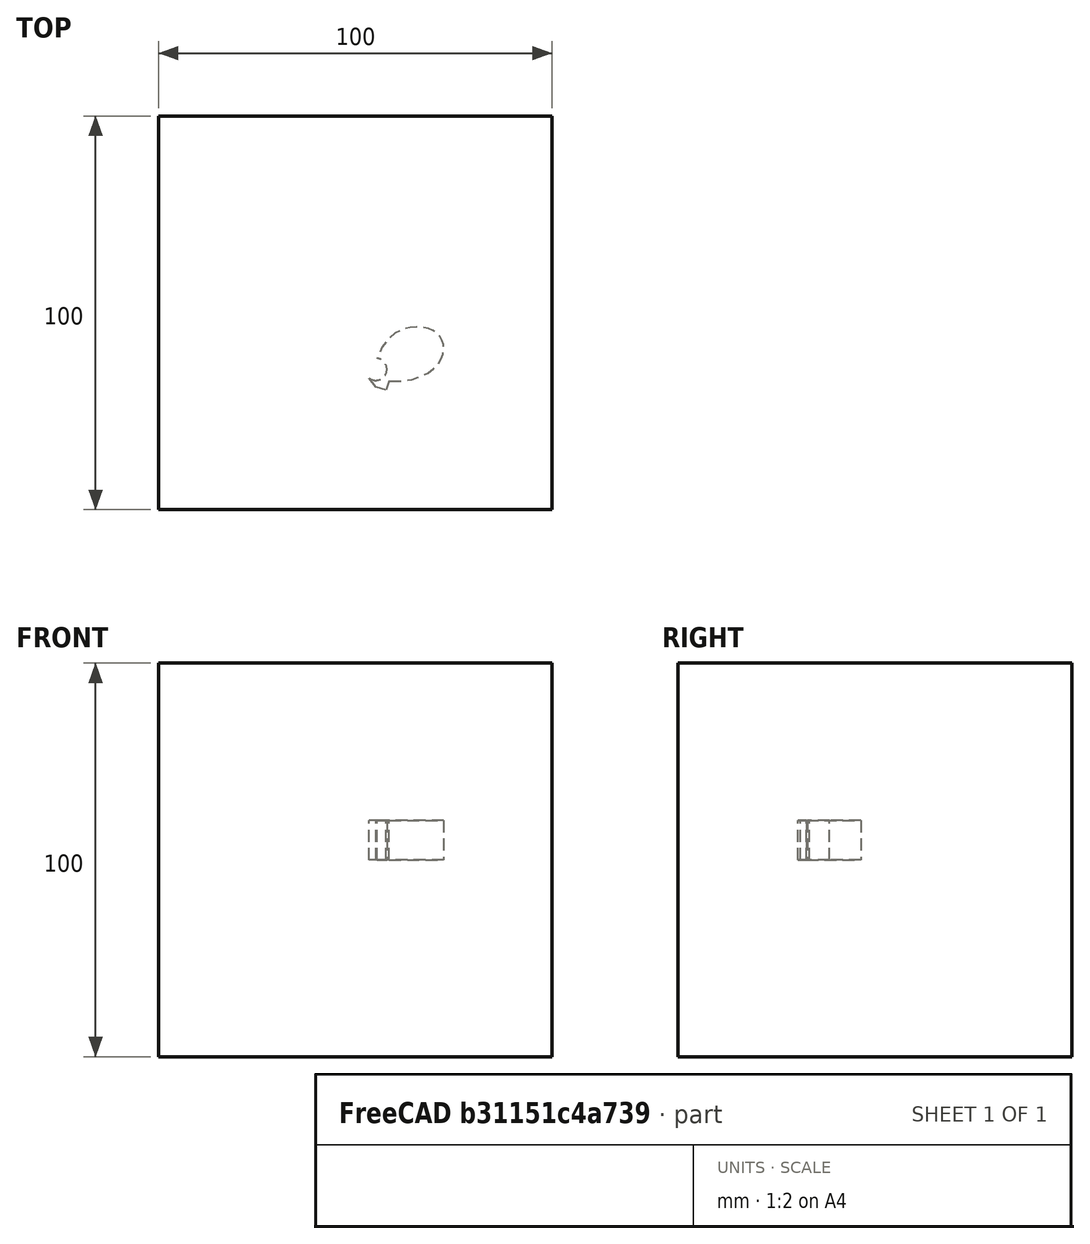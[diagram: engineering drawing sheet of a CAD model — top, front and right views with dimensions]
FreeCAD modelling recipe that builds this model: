
FCSTD DOCUMENT  (FreeCAD 1.0R39109 (Git))
Label: mirrorTest-1b
License: All rights reserved
LicenseURL: http://en.wikipedia.org/wiki/All_rights_reserved
objects: App::DocumentObjectGroupPython×1248, App::Part×2, Part::FeaturePython×1, Sketcher::SketchObject×1, Part::Extrusion×1, Part::Mirroring×1
note: 5 computed .brp shape members not serialized (recipe doc carries the construction recipe); baked Part::Feature solids carry a one-line shape summary decoded from their .brp

FEATURE [App::DocumentObjectGroupPython] HALFPI  # scripted group (container) (typed FeaturePython)
  name = HALFPI
  value = pi/2.
FEATURE [App::DocumentObjectGroupPython] PI  # scripted group (container) (typed FeaturePython)
  name = PI
  value = 1.*pi
FEATURE [App::DocumentObjectGroupPython] TWOPI  # scripted group (container) (typed FeaturePython)
  name = TWOPI
  value = 2.*pi
FEATURE [App::DocumentObjectGroupPython] Constants  # scripted group (container) (typed FeaturePython)
  Group = -> [HALFPI,PI,TWOPI]
FEATURE [App::DocumentObjectGroupPython] Variables  # scripted group (container) (typed FeaturePython)
FEATURE [App::DocumentObjectGroupPython] Quantities  # scripted group (container) (typed FeaturePython)
FEATURE [App::DocumentObjectGroupPython] Isotopes  # scripted group (container) (typed FeaturePython)
FEATURE [App::DocumentObjectGroupPython] Elements  # scripted group (container) (typed FeaturePython)
FEATURE [App::DocumentObjectGroupPython] G4Isotopes  # scripted group (container) (typed FeaturePython)
FEATURE [App::DocumentObjectGroupPython] H_element  # scripted group (container) (typed FeaturePython)
  Z = 1
  atom_value = 1.008
  formula = H
  name = H_element
FEATURE [App::DocumentObjectGroupPython] He_element  # scripted group (container) (typed FeaturePython)
  Z = 2
  atom_value = 4.0026
  formula = He
  name = He_element
FEATURE [App::DocumentObjectGroupPython] Li_element  # scripted group (container) (typed FeaturePython)
  Z = 3
  atom_value = 6.94
  formula = Li
  name = Li_element
FEATURE [App::DocumentObjectGroupPython] Be_element  # scripted group (container) (typed FeaturePython)
  Z = 4
  atom_value = 9.01218
  formula = Be
  name = Be_element
FEATURE [App::DocumentObjectGroupPython] B_element  # scripted group (container) (typed FeaturePython)
  Z = 5
  atom_value = 10.81
  formula = B
  name = B_element
FEATURE [App::DocumentObjectGroupPython] C_element  # scripted group (container) (typed FeaturePython)
  Z = 6
  atom_value = 12.011
  formula = C
  name = C_element
FEATURE [App::DocumentObjectGroupPython] N_element  # scripted group (container) (typed FeaturePython)
  Z = 7
  atom_value = 14.007
  formula = N
  name = N_element
FEATURE [App::DocumentObjectGroupPython] O_element  # scripted group (container) (typed FeaturePython)
  Z = 8
  atom_value = 15.999
  formula = O
  name = O_element
FEATURE [App::DocumentObjectGroupPython] F_element  # scripted group (container) (typed FeaturePython)
  Z = 9
  atom_value = 18.9984
  formula = F
  name = F_element
FEATURE [App::DocumentObjectGroupPython] Ne_element  # scripted group (container) (typed FeaturePython)
  Z = 10
  atom_value = 20.1797
  formula = Ne
  name = Ne_element
FEATURE [App::DocumentObjectGroupPython] Na_element  # scripted group (container) (typed FeaturePython)
  Z = 11
  atom_value = 22.9898
  formula = Na
  name = Na_element
FEATURE [App::DocumentObjectGroupPython] Mg_element  # scripted group (container) (typed FeaturePython)
  Z = 12
  atom_value = 24.305
  formula = Mg
  name = Mg_element
FEATURE [App::DocumentObjectGroupPython] Al_element  # scripted group (container) (typed FeaturePython)
  Z = 13
  atom_value = 26.9815
  formula = Al
  name = Al_element
FEATURE [App::DocumentObjectGroupPython] Si_element  # scripted group (container) (typed FeaturePython)
  Z = 14
  atom_value = 28.085
  formula = Si
  name = Si_element
FEATURE [App::DocumentObjectGroupPython] P_element  # scripted group (container) (typed FeaturePython)
  Z = 15
  atom_value = 30.9738
  formula = P
  name = P_element
FEATURE [App::DocumentObjectGroupPython] S_element  # scripted group (container) (typed FeaturePython)
  Z = 16
  atom_value = 32.06
  formula = S
  name = S_element
FEATURE [App::DocumentObjectGroupPython] Cl_element  # scripted group (container) (typed FeaturePython)
  Z = 17
  atom_value = 35.45
  formula = Cl
  name = Cl_element
FEATURE [App::DocumentObjectGroupPython] Ar_element  # scripted group (container) (typed FeaturePython)
  Z = 18
  atom_value = 39.95
  formula = Ar
  name = Ar_element
FEATURE [App::DocumentObjectGroupPython] K_element  # scripted group (container) (typed FeaturePython)
  Z = 19
  atom_value = 39.0983
  formula = K
  name = K_element
FEATURE [App::DocumentObjectGroupPython] Ca_element  # scripted group (container) (typed FeaturePython)
  Z = 20
  atom_value = 40.078
  formula = Ca
  name = Ca_element
FEATURE [App::DocumentObjectGroupPython] Sc_element  # scripted group (container) (typed FeaturePython)
  Z = 21
  atom_value = 44.9559
  formula = Sc
  name = Sc_element
FEATURE [App::DocumentObjectGroupPython] Ti_element  # scripted group (container) (typed FeaturePython)
  Z = 22
  atom_value = 47.867
  formula = Ti
  name = Ti_element
FEATURE [App::DocumentObjectGroupPython] V_element  # scripted group (container) (typed FeaturePython)
  Z = 23
  atom_value = 50.9415
  formula = V
  name = V_element
FEATURE [App::DocumentObjectGroupPython] Cr_element  # scripted group (container) (typed FeaturePython)
  Z = 24
  atom_value = 51.9961
  formula = Cr
  name = Cr_element
FEATURE [App::DocumentObjectGroupPython] Mn_element  # scripted group (container) (typed FeaturePython)
  Z = 25
  atom_value = 54.938
  formula = Mn
  name = Mn_element
FEATURE [App::DocumentObjectGroupPython] Fe_element  # scripted group (container) (typed FeaturePython)
  Z = 26
  atom_value = 55.845
  formula = Fe
  name = Fe_element
FEATURE [App::DocumentObjectGroupPython] Co_element  # scripted group (container) (typed FeaturePython)
  Z = 27
  atom_value = 58.9332
  formula = Co
  name = Co_element
FEATURE [App::DocumentObjectGroupPython] Ni_element  # scripted group (container) (typed FeaturePython)
  Z = 28
  atom_value = 58.6934
  formula = Ni
  name = Ni_element
FEATURE [App::DocumentObjectGroupPython] Cu_element  # scripted group (container) (typed FeaturePython)
  Z = 29
  atom_value = 63.546
  formula = Cu
  name = Cu_element
FEATURE [App::DocumentObjectGroupPython] Zn_element  # scripted group (container) (typed FeaturePython)
  Z = 30
  atom_value = 65.38
  formula = Zn
  name = Zn_element
FEATURE [App::DocumentObjectGroupPython] Ga_element  # scripted group (container) (typed FeaturePython)
  Z = 31
  atom_value = 69.723
  formula = Ga
  name = Ga_element
FEATURE [App::DocumentObjectGroupPython] Ge_element  # scripted group (container) (typed FeaturePython)
  Z = 32
  atom_value = 72.63
  formula = Ge
  name = Ge_element
FEATURE [App::DocumentObjectGroupPython] As_element  # scripted group (container) (typed FeaturePython)
  Z = 33
  atom_value = 74.9216
  formula = As
  name = As_element
FEATURE [App::DocumentObjectGroupPython] Se_element  # scripted group (container) (typed FeaturePython)
  Z = 34
  atom_value = 78.971
  formula = Se
  name = Se_element
FEATURE [App::DocumentObjectGroupPython] Br_element  # scripted group (container) (typed FeaturePython)
  Z = 35
  atom_value = 79.904
  formula = Br
  name = Br_element
FEATURE [App::DocumentObjectGroupPython] Kr_element  # scripted group (container) (typed FeaturePython)
  Z = 36
  atom_value = 83.798
  formula = Kr
  name = Kr_element
FEATURE [App::DocumentObjectGroupPython] Rb_element  # scripted group (container) (typed FeaturePython)
  Z = 37
  atom_value = 85.4678
  formula = Rb
  name = Rb_element
FEATURE [App::DocumentObjectGroupPython] Sr_element  # scripted group (container) (typed FeaturePython)
  Z = 38
  atom_value = 87.62
  formula = Sr
  name = Sr_element
FEATURE [App::DocumentObjectGroupPython] Y_element  # scripted group (container) (typed FeaturePython)
  Z = 39
  atom_value = 88.9058
  formula = Y
  name = Y_element
FEATURE [App::DocumentObjectGroupPython] Zr_element  # scripted group (container) (typed FeaturePython)
  Z = 40
  atom_value = 91.224
  formula = Zr
  name = Zr_element
FEATURE [App::DocumentObjectGroupPython] Nb_element  # scripted group (container) (typed FeaturePython)
  Z = 41
  atom_value = 92.9064
  formula = Nb
  name = Nb_element
FEATURE [App::DocumentObjectGroupPython] Mo_element  # scripted group (container) (typed FeaturePython)
  Z = 42
  atom_value = 95.95
  formula = Mo
  name = Mo_element
FEATURE [App::DocumentObjectGroupPython] Tc_element  # scripted group (container) (typed FeaturePython)
  Z = 43
  atom_value = 97
  formula = Tc
  name = Tc_element
FEATURE [App::DocumentObjectGroupPython] Ru_element  # scripted group (container) (typed FeaturePython)
  Z = 44
  atom_value = 101.07
  formula = Ru
  name = Ru_element
FEATURE [App::DocumentObjectGroupPython] Rh_element  # scripted group (container) (typed FeaturePython)
  Z = 45
  atom_value = 102.905
  formula = Rh
  name = Rh_element
FEATURE [App::DocumentObjectGroupPython] Pd_element  # scripted group (container) (typed FeaturePython)
  Z = 46
  atom_value = 106.42
  formula = Pd
  name = Pd_element
FEATURE [App::DocumentObjectGroupPython] Ag_element  # scripted group (container) (typed FeaturePython)
  Z = 47
  atom_value = 107.868
  formula = Ag
  name = Ag_element
FEATURE [App::DocumentObjectGroupPython] Cd_element  # scripted group (container) (typed FeaturePython)
  Z = 48
  atom_value = 112.414
  formula = Cd
  name = Cd_element
FEATURE [App::DocumentObjectGroupPython] In_element  # scripted group (container) (typed FeaturePython)
  Z = 49
  atom_value = 114.818
  formula = In
  name = In_element
FEATURE [App::DocumentObjectGroupPython] Sn_element  # scripted group (container) (typed FeaturePython)
  Z = 50
  atom_value = 118.71
  formula = Sn
  name = Sn_element
FEATURE [App::DocumentObjectGroupPython] Sb_element  # scripted group (container) (typed FeaturePython)
  Z = 51
  atom_value = 121.76
  formula = Sb
  name = Sb_element
FEATURE [App::DocumentObjectGroupPython] Te_element  # scripted group (container) (typed FeaturePython)
  Z = 52
  atom_value = 127.6
  formula = Te
  name = Te_element
FEATURE [App::DocumentObjectGroupPython] I_element  # scripted group (container) (typed FeaturePython)
  Z = 53
  atom_value = 126.904
  formula = I
  name = I_element
FEATURE [App::DocumentObjectGroupPython] Xe_element  # scripted group (container) (typed FeaturePython)
  Z = 54
  atom_value = 131.293
  formula = Xe
  name = Xe_element
FEATURE [App::DocumentObjectGroupPython] Cs_element  # scripted group (container) (typed FeaturePython)
  Z = 55
  atom_value = 132.905
  formula = Cs
  name = Cs_element
FEATURE [App::DocumentObjectGroupPython] Ba_element  # scripted group (container) (typed FeaturePython)
  Z = 56
  atom_value = 137.327
  formula = Ba
  name = Ba_element
FEATURE [App::DocumentObjectGroupPython] La_element  # scripted group (container) (typed FeaturePython)
  Z = 57
  atom_value = 138.905
  formula = La
  name = La_element
FEATURE [App::DocumentObjectGroupPython] Ce_element  # scripted group (container) (typed FeaturePython)
  Z = 58
  atom_value = 140.116
  formula = Ce
  name = Ce_element
FEATURE [App::DocumentObjectGroupPython] Pr_element  # scripted group (container) (typed FeaturePython)
  Z = 59
  atom_value = 140.908
  formula = Pr
  name = Pr_element
FEATURE [App::DocumentObjectGroupPython] Nd_element  # scripted group (container) (typed FeaturePython)
  Z = 60
  atom_value = 144.242
  formula = Nd
  name = Nd_element
FEATURE [App::DocumentObjectGroupPython] Pm_element  # scripted group (container) (typed FeaturePython)
  Z = 61
  atom_value = 145
  formula = Pm
  name = Pm_element
FEATURE [App::DocumentObjectGroupPython] Sm_element  # scripted group (container) (typed FeaturePython)
  Z = 62
  atom_value = 150.36
  formula = Sm
  name = Sm_element
FEATURE [App::DocumentObjectGroupPython] Eu_element  # scripted group (container) (typed FeaturePython)
  Z = 63
  atom_value = 151.964
  formula = Eu
  name = Eu_element
FEATURE [App::DocumentObjectGroupPython] Gd_element  # scripted group (container) (typed FeaturePython)
  Z = 64
  atom_value = 157.25
  formula = Gd
  name = Gd_element
FEATURE [App::DocumentObjectGroupPython] Tb_element  # scripted group (container) (typed FeaturePython)
  Z = 65
  atom_value = 158.925
  formula = Tb
  name = Tb_element
FEATURE [App::DocumentObjectGroupPython] Dy_element  # scripted group (container) (typed FeaturePython)
  Z = 66
  atom_value = 162.5
  formula = Dy
  name = Dy_element
FEATURE [App::DocumentObjectGroupPython] Ho_element  # scripted group (container) (typed FeaturePython)
  Z = 67
  atom_value = 164.93
  formula = Ho
  name = Ho_element
FEATURE [App::DocumentObjectGroupPython] Er_element  # scripted group (container) (typed FeaturePython)
  Z = 68
  atom_value = 167.259
  formula = Er
  name = Er_element
FEATURE [App::DocumentObjectGroupPython] Tm_element  # scripted group (container) (typed FeaturePython)
  Z = 69
  atom_value = 168.934
  formula = Tm
  name = Tm_element
FEATURE [App::DocumentObjectGroupPython] Yb_element  # scripted group (container) (typed FeaturePython)
  Z = 70
  atom_value = 173.045
  formula = Yb
  name = Yb_element
FEATURE [App::DocumentObjectGroupPython] Lu_element  # scripted group (container) (typed FeaturePython)
  Z = 71
  atom_value = 174.967
  formula = Lu
  name = Lu_element
FEATURE [App::DocumentObjectGroupPython] Hf_element  # scripted group (container) (typed FeaturePython)
  Z = 72
  atom_value = 178.49
  formula = Hf
  name = Hf_element
FEATURE [App::DocumentObjectGroupPython] Ta_element  # scripted group (container) (typed FeaturePython)
  Z = 73
  atom_value = 180.948
  formula = Ta
  name = Ta_element
FEATURE [App::DocumentObjectGroupPython] W_element  # scripted group (container) (typed FeaturePython)
  Z = 74
  atom_value = 183.84
  formula = W
  name = W_element
FEATURE [App::DocumentObjectGroupPython] Re_element  # scripted group (container) (typed FeaturePython)
  Z = 75
  atom_value = 186.207
  formula = Re
  name = Re_element
FEATURE [App::DocumentObjectGroupPython] Os_element  # scripted group (container) (typed FeaturePython)
  Z = 76
  atom_value = 190.23
  formula = Os
  name = Os_element
FEATURE [App::DocumentObjectGroupPython] Ir_element  # scripted group (container) (typed FeaturePython)
  Z = 77
  atom_value = 192.217
  formula = Ir
  name = Ir_element
FEATURE [App::DocumentObjectGroupPython] Pt_element  # scripted group (container) (typed FeaturePython)
  Z = 78
  atom_value = 195.084
  formula = Pt
  name = Pt_element
FEATURE [App::DocumentObjectGroupPython] Au_element  # scripted group (container) (typed FeaturePython)
  Z = 79
  atom_value = 196.967
  formula = Au
  name = Au_element
FEATURE [App::DocumentObjectGroupPython] Hg_element  # scripted group (container) (typed FeaturePython)
  Z = 80
  atom_value = 200.592
  formula = Hg
  name = Hg_element
FEATURE [App::DocumentObjectGroupPython] Tl_element  # scripted group (container) (typed FeaturePython)
  Z = 81
  atom_value = 204.38
  formula = Tl
  name = Tl_element
FEATURE [App::DocumentObjectGroupPython] Pb_element  # scripted group (container) (typed FeaturePython)
  Z = 82
  atom_value = 207.2
  formula = Pb
  name = Pb_element
FEATURE [App::DocumentObjectGroupPython] Bi_element  # scripted group (container) (typed FeaturePython)
  Z = 83
  atom_value = 208.98
  formula = Bi
  name = Bi_element
FEATURE [App::DocumentObjectGroupPython] Po_element  # scripted group (container) (typed FeaturePython)
  Z = 84
  atom_value = 209
  formula = Po
  name = Po_element
FEATURE [App::DocumentObjectGroupPython] At_element  # scripted group (container) (typed FeaturePython)
  Z = 85
  atom_value = 210
  formula = At
  name = At_element
FEATURE [App::DocumentObjectGroupPython] Rn_element  # scripted group (container) (typed FeaturePython)
  Z = 86
  atom_value = 222
  formula = Rn
  name = Rn_element
FEATURE [App::DocumentObjectGroupPython] Fr_element  # scripted group (container) (typed FeaturePython)
  Z = 87
  atom_value = 223
  formula = Fr
  name = Fr_element
FEATURE [App::DocumentObjectGroupPython] Ra_element  # scripted group (container) (typed FeaturePython)
  Z = 88
  atom_value = 226
  formula = Ra
  name = Ra_element
FEATURE [App::DocumentObjectGroupPython] Ac_element  # scripted group (container) (typed FeaturePython)
  Z = 89
  atom_value = 227
  formula = Ac
  name = Ac_element
FEATURE [App::DocumentObjectGroupPython] Th_element  # scripted group (container) (typed FeaturePython)
  Z = 90
  atom_value = 232.038
  formula = Th
  name = Th_element
FEATURE [App::DocumentObjectGroupPython] Pa_element  # scripted group (container) (typed FeaturePython)
  Z = 91
  atom_value = 231.036
  formula = Pa
  name = Pa_element
FEATURE [App::DocumentObjectGroupPython] U_element  # scripted group (container) (typed FeaturePython)
  Z = 92
  atom_value = 238.029
  formula = U
  name = U_element
FEATURE [App::DocumentObjectGroupPython] Np_element  # scripted group (container) (typed FeaturePython)
  Z = 93
  atom_value = 237
  formula = Np
  name = Np_element
FEATURE [App::DocumentObjectGroupPython] Pu_element  # scripted group (container) (typed FeaturePython)
  Z = 94
  atom_value = 244
  formula = Pu
  name = Pu_element
FEATURE [App::DocumentObjectGroupPython] Am_element  # scripted group (container) (typed FeaturePython)
  Z = 95
  atom_value = 243
  formula = Am
  name = Am_element
FEATURE [App::DocumentObjectGroupPython] Cm_element  # scripted group (container) (typed FeaturePython)
  Z = 96
  atom_value = 247
  formula = Cm
  name = Cm_element
FEATURE [App::DocumentObjectGroupPython] Bk_element  # scripted group (container) (typed FeaturePython)
  Z = 97
  atom_value = 247
  formula = Bk
  name = Bk_element
FEATURE [App::DocumentObjectGroupPython] Cf_element  # scripted group (container) (typed FeaturePython)
  Z = 98
  atom_value = 251
  formula = Cf
  name = Cf_element
FEATURE [App::DocumentObjectGroupPython] G4Elements  # scripted group (container) (typed FeaturePython)
  Group = -> [H_element,He_element,Li_element,Be_element,B_element,C_element,N_element,O_element,F_element,Ne_element,Na_element,Mg_element,Al_element,Si_element,P_element,S_element,Cl_element,Ar_element,K_element,Ca_element,Sc_element,Ti_element,V_element,Cr_element,Mn_element,Fe_element,Co_element,Ni_element,Cu_element,Zn_element,Ga_element,Ge_element,As_element,Se_element,Br_element,Kr_element,Rb_element,+61 more]
FEATURE [App::DocumentObjectGroupPython] H_element001  label="H_element : 0.101"  # scripted group (container) (typed FeaturePython)
  n = 0.101327
FEATURE [App::DocumentObjectGroupPython] C_element001  label="C_element : 0.775"  # scripted group (container) (typed FeaturePython)
  n = 0.7755
FEATURE [App::DocumentObjectGroupPython] N_element001  label="N_element : 0.035"  # scripted group (container) (typed FeaturePython)
  n = 0.035057
FEATURE [App::DocumentObjectGroupPython] O_element001  label="O_element : 0.052"  # scripted group (container) (typed FeaturePython)
  n = 0.0523159
FEATURE [App::DocumentObjectGroupPython] F_element001  label="F_element : 0.017"  # scripted group (container) (typed FeaturePython)
  n = 0.017422
FEATURE [App::DocumentObjectGroupPython] Ca_element001  label="Ca_element : 0.018"  # scripted group (container) (typed FeaturePython)
  n = 0.018378
FEATURE [App::DocumentObjectGroupPython] G4_A_150_TISSUE  label="G4_A-150_TISSUE"  # scripted group (container) (typed FeaturePython)
  Dunit = g/cm3
  Dvalue = 1.127
  Group = -> [H_element001,C_element001,N_element001,O_element001,F_element001,Ca_element001]
  conduct = 2
  density = 1
  expand = 3
  formula = G4_A-150_TISSUE
  name = G4_A-150_TISSUE
  specific = 4
FEATURE [App::DocumentObjectGroupPython] C_element002  label="C_element : 3"  # scripted group (container) (typed FeaturePython)
  n = 3
  ref = C_element
FEATURE [App::DocumentObjectGroupPython] H_element002  label="H_element : 6"  # scripted group (container) (typed FeaturePython)
  n = 6
  ref = H_element
FEATURE [App::DocumentObjectGroupPython] O_element002  label="O_element : 1"  # scripted group (container) (typed FeaturePython)
  n = 1
  ref = O_element
FEATURE [App::DocumentObjectGroupPython] G4_ACETONE  # scripted group (container) (typed FeaturePython)
  Dunit = g/cm3
  Dvalue = 0.7899
  Group = -> [C_element002,H_element002,O_element002]
  conduct = 2
  density = 1
  expand = 3
  formula = G4_ACETONE
  name = G4_ACETONE
  specific = 4
FEATURE [App::DocumentObjectGroupPython] C_element003  label="C_element : 2"  # scripted group (container) (typed FeaturePython)
  n = 2
  ref = C_element
FEATURE [App::DocumentObjectGroupPython] H_element003  label="H_element : 2"  # scripted group (container) (typed FeaturePython)
  n = 2
  ref = H_element
FEATURE [App::DocumentObjectGroupPython] G4_ACETYLENE  # scripted group (container) (typed FeaturePython)
  Dunit = g/cm3
  Dvalue = 0.0010967
  Group = -> [C_element003,H_element003]
  conduct = 2
  density = 1
  expand = 3
  formula = G4_ACETYLENE
  name = G4_ACETYLENE
  specific = 4
FEATURE [App::DocumentObjectGroupPython] C_element004  label="C_element : 5"  # scripted group (container) (typed FeaturePython)
  n = 5
  ref = C_element
FEATURE [App::DocumentObjectGroupPython] H_element004  label="H_element : 5"  # scripted group (container) (typed FeaturePython)
  n = 5
  ref = H_element
FEATURE [App::DocumentObjectGroupPython] N_element002  label="N_element : 5"  # scripted group (container) (typed FeaturePython)
  n = 5
  ref = N_element
FEATURE [App::DocumentObjectGroupPython] G4_ADENINE  # scripted group (container) (typed FeaturePython)
  Dunit = g/cm3
  Dvalue = 1.6
  Group = -> [C_element004,H_element004,N_element002]
  conduct = 2
  density = 1
  expand = 3
  formula = G4_ADENINE
  name = G4_ADENINE
  specific = 4
FEATURE [App::DocumentObjectGroupPython] H_element005  label="H_element : 0.114"  # scripted group (container) (typed FeaturePython)
  n = 0.114
FEATURE [App::DocumentObjectGroupPython] C_element005  label="C_element : 0.598"  # scripted group (container) (typed FeaturePython)
  n = 0.598
FEATURE [App::DocumentObjectGroupPython] N_element003  label="N_element : 0.007"  # scripted group (container) (typed FeaturePython)
  n = 0.007
FEATURE [App::DocumentObjectGroupPython] O_element003  label="O_element : 0.278"  # scripted group (container) (typed FeaturePython)
  n = 0.278
FEATURE [App::DocumentObjectGroupPython] Na_element001  label="Na_element : 0.001"  # scripted group (container) (typed FeaturePython)
  n = 0.001
FEATURE [App::DocumentObjectGroupPython] S_element001  label="S_element : 0.001"  # scripted group (container) (typed FeaturePython)
  n = 0.001
FEATURE [App::DocumentObjectGroupPython] Cl_element001  label="Cl_element : 0.001"  # scripted group (container) (typed FeaturePython)
  n = 0.001
FEATURE [App::DocumentObjectGroupPython] G4_ADIPOSE_TISSUE_ICRP  # scripted group (container) (typed FeaturePython)
  Dunit = g/cm3
  Dvalue = 0.95
  Group = -> [H_element005,C_element005,N_element003,O_element003,Na_element001,S_element001,Cl_element001]
  conduct = 2
  density = 1
  expand = 3
  formula = G4_ADIPOSE_TISSUE_ICRP
  name = G4_ADIPOSE_TISSUE_ICRP
  specific = 4
FEATURE [App::DocumentObjectGroupPython] C_element006  label="C_element : 0.000"  # scripted group (container) (typed FeaturePython)
  n = 0.000124
FEATURE [App::DocumentObjectGroupPython] N_element004  label="N_element : 0.755"  # scripted group (container) (typed FeaturePython)
  n = 0.755268
FEATURE [App::DocumentObjectGroupPython] O_element004  label="O_element : 0.232"  # scripted group (container) (typed FeaturePython)
  n = 0.231781
FEATURE [App::DocumentObjectGroupPython] Ar_element001  label="Ar_element : 0.013"  # scripted group (container) (typed FeaturePython)
  n = 0.012827
FEATURE [App::DocumentObjectGroupPython] G4_AIR  # scripted group (container) (typed FeaturePython)
  Dunit = g/cm3
  Dvalue = 0.00120479
  Group = -> [C_element006,N_element004,O_element004,Ar_element001]
  conduct = 2
  density = 1
  expand = 3
  formula = G4_AIR
  name = G4_AIR
  specific = 4
FEATURE [App::DocumentObjectGroupPython] C_element007  label="C_element : 006"  # scripted group (container) (typed FeaturePython)
  n = 3
  ref = C_element
FEATURE [App::DocumentObjectGroupPython] H_element006  label="H_element : 7"  # scripted group (container) (typed FeaturePython)
  n = 7
  ref = H_element
FEATURE [App::DocumentObjectGroupPython] N_element005  label="N_element : 1"  # scripted group (container) (typed FeaturePython)
  n = 1
  ref = N_element
FEATURE [App::DocumentObjectGroupPython] O_element005  label="O_element : 2"  # scripted group (container) (typed FeaturePython)
  n = 2
  ref = O_element
FEATURE [App::DocumentObjectGroupPython] G4_ALANINE  # scripted group (container) (typed FeaturePython)
  Dunit = g/cm3
  Dvalue = 1.42
  Group = -> [C_element007,H_element006,N_element005,O_element005]
  conduct = 2
  density = 1
  expand = 3
  formula = G4_ALANINE
  name = G4_ALANINE
  specific = 4
FEATURE [App::DocumentObjectGroupPython] Al_element001  label="Al_element : 2"  # scripted group (container) (typed FeaturePython)
  n = 2
  ref = Al_element
FEATURE [App::DocumentObjectGroupPython] O_element006  label="O_element : 3"  # scripted group (container) (typed FeaturePython)
  n = 3
  ref = O_element
FEATURE [App::DocumentObjectGroupPython] G4_ALUMINUM_OXIDE  # scripted group (container) (typed FeaturePython)
  Dunit = g/cm3
  Dvalue = 3.97
  Group = -> [Al_element001,O_element006]
  conduct = 2
  density = 1
  expand = 3
  formula = G4_ALUMINUM_OXIDE
  name = G4_ALUMINUM_OXIDE
  specific = 4
FEATURE [App::DocumentObjectGroupPython] H_element007  label="H_element : 0.106"  # scripted group (container) (typed FeaturePython)
  n = 0.10593
FEATURE [App::DocumentObjectGroupPython] C_element008  label="C_element : 0.789"  # scripted group (container) (typed FeaturePython)
  n = 0.788974
FEATURE [App::DocumentObjectGroupPython] O_element007  label="O_element : 0.105"  # scripted group (container) (typed FeaturePython)
  n = 0.105096
FEATURE [App::DocumentObjectGroupPython] G4_AMBER  # scripted group (container) (typed FeaturePython)
  Dunit = g/cm3
  Dvalue = 1.1
  Group = -> [H_element007,C_element008,O_element007]
  conduct = 2
  density = 1
  expand = 3
  formula = G4_AMBER
  name = G4_AMBER
  specific = 4
FEATURE [App::DocumentObjectGroupPython] N_element006  label="N_element : 006"  # scripted group (container) (typed FeaturePython)
  n = 1
  ref = N_element
FEATURE [App::DocumentObjectGroupPython] H_element008  label="H_element : 3"  # scripted group (container) (typed FeaturePython)
  n = 3
  ref = H_element
FEATURE [App::DocumentObjectGroupPython] G4_AMMONIA  # scripted group (container) (typed FeaturePython)
  Dunit = g/cm3
  Dvalue = 0.000826019
  Group = -> [N_element006,H_element008]
  conduct = 2
  density = 1
  expand = 3
  formula = G4_AMMONIA
  name = G4_AMMONIA
  specific = 4
FEATURE [App::DocumentObjectGroupPython] C_element009  label="C_element : 6"  # scripted group (container) (typed FeaturePython)
  n = 6
  ref = C_element
FEATURE [App::DocumentObjectGroupPython] H_element009  label="H_element : 008"  # scripted group (container) (typed FeaturePython)
  n = 7
  ref = H_element
FEATURE [App::DocumentObjectGroupPython] N_element007  label="N_element : 007"  # scripted group (container) (typed FeaturePython)
  n = 1
  ref = N_element
FEATURE [App::DocumentObjectGroupPython] G4_ANILINE  # scripted group (container) (typed FeaturePython)
  Dunit = g/cm3
  Dvalue = 1.0235
  Group = -> [C_element009,H_element009,N_element007]
  conduct = 2
  density = 1
  expand = 3
  formula = G4_ANILINE
  name = G4_ANILINE
  specific = 4
FEATURE [App::DocumentObjectGroupPython] C_element010  label="C_element : 14"  # scripted group (container) (typed FeaturePython)
  n = 14
  ref = C_element
FEATURE [App::DocumentObjectGroupPython] H_element010  label="H_element : 10"  # scripted group (container) (typed FeaturePython)
  n = 10
  ref = H_element
FEATURE [App::DocumentObjectGroupPython] G4_ANTHRACENE  # scripted group (container) (typed FeaturePython)
  Dunit = g/cm3
  Dvalue = 1.283
  Group = -> [C_element010,H_element010]
  conduct = 2
  density = 1
  expand = 3
  formula = G4_ANTHRACENE
  name = G4_ANTHRACENE
  specific = 4
FEATURE [App::DocumentObjectGroupPython] H_element011  label="H_element : 0.065"  # scripted group (container) (typed FeaturePython)
  n = 0.0654709
FEATURE [App::DocumentObjectGroupPython] C_element011  label="C_element : 0.537"  # scripted group (container) (typed FeaturePython)
  n = 0.536944
FEATURE [App::DocumentObjectGroupPython] N_element008  label="N_element : 0.021"  # scripted group (container) (typed FeaturePython)
  n = 0.0215
FEATURE [App::DocumentObjectGroupPython] O_element008  label="O_element : 0.032"  # scripted group (container) (typed FeaturePython)
  n = 0.032085
FEATURE [App::DocumentObjectGroupPython] F_element002  label="F_element : 0.167"  # scripted group (container) (typed FeaturePython)
  n = 0.167411
FEATURE [App::DocumentObjectGroupPython] Ca_element002  label="Ca_element : 0.177"  # scripted group (container) (typed FeaturePython)
  n = 0.176589
FEATURE [App::DocumentObjectGroupPython] G4_B_100_BONE  label="G4_B-100_BONE"  # scripted group (container) (typed FeaturePython)
  Dunit = g/cm3
  Dvalue = 1.45
  Group = -> [H_element011,C_element011,N_element008,O_element008,F_element002,Ca_element002]
  conduct = 2
  density = 1
  expand = 3
  formula = G4_B-100_BONE
  name = G4_B-100_BONE
  specific = 4
FEATURE [App::DocumentObjectGroupPython] H_element012  label="H_element : 0.057"  # scripted group (container) (typed FeaturePython)
  n = 0.057441
FEATURE [App::DocumentObjectGroupPython] C_element012  label="C_element : 0.790"  # scripted group (container) (typed FeaturePython)
  n = 0.774591
FEATURE [App::DocumentObjectGroupPython] O_element009  label="O_element : 0.168"  # scripted group (container) (typed FeaturePython)
  n = 0.167968
FEATURE [App::DocumentObjectGroupPython] G4_BAKELITE  # scripted group (container) (typed FeaturePython)
  Dunit = g/cm3
  Dvalue = 1.25
  Group = -> [H_element012,C_element012,O_element009]
  conduct = 2
  density = 1
  expand = 3
  formula = G4_BAKELITE
  name = G4_BAKELITE
  specific = 4
FEATURE [App::DocumentObjectGroupPython] Ba_element001  label="Ba_element : 1"  # scripted group (container) (typed FeaturePython)
  n = 1
  ref = Ba_element
FEATURE [App::DocumentObjectGroupPython] F_element003  label="F_element : 2"  # scripted group (container) (typed FeaturePython)
  n = 2
  ref = F_element
FEATURE [App::DocumentObjectGroupPython] G4_BARIUM_FLUORIDE  # scripted group (container) (typed FeaturePython)
  Dunit = g/cm3
  Dvalue = 4.89
  Group = -> [Ba_element001,F_element003]
  conduct = 2
  density = 1
  expand = 3
  formula = G4_BARIUM_FLUORIDE
  name = G4_BARIUM_FLUORIDE
  specific = 4
FEATURE [App::DocumentObjectGroupPython] Ba_element002  label="Ba_element : 002"  # scripted group (container) (typed FeaturePython)
  n = 1
  ref = Ba_element
FEATURE [App::DocumentObjectGroupPython] S_element002  label="S_element : 1"  # scripted group (container) (typed FeaturePython)
  n = 1
  ref = S_element
FEATURE [App::DocumentObjectGroupPython] O_element010  label="O_element : 4"  # scripted group (container) (typed FeaturePython)
  n = 4
  ref = O_element
FEATURE [App::DocumentObjectGroupPython] G4_BARIUM_SULFATE  # scripted group (container) (typed FeaturePython)
  Dunit = g/cm3
  Dvalue = 4.5
  Group = -> [Ba_element002,S_element002,O_element010]
  conduct = 2
  density = 1
  expand = 3
  formula = G4_BARIUM_SULFATE
  name = G4_BARIUM_SULFATE
  specific = 4
FEATURE [App::DocumentObjectGroupPython] C_element013  label="C_element : 007"  # scripted group (container) (typed FeaturePython)
  n = 6
  ref = C_element
FEATURE [App::DocumentObjectGroupPython] H_element013  label="H_element : 009"  # scripted group (container) (typed FeaturePython)
  n = 6
  ref = H_element
FEATURE [App::DocumentObjectGroupPython] G4_BENZENE  # scripted group (container) (typed FeaturePython)
  Dunit = g/cm3
  Dvalue = 0.87865
  Group = -> [C_element013,H_element013]
  conduct = 2
  density = 1
  expand = 3
  formula = G4_BENZENE
  name = G4_BENZENE
  specific = 4
FEATURE [App::DocumentObjectGroupPython] Be_element001  label="Be_element : 1"  # scripted group (container) (typed FeaturePython)
  n = 1
  ref = Be_element
FEATURE [App::DocumentObjectGroupPython] O_element011  label="O_element : 005"  # scripted group (container) (typed FeaturePython)
  n = 1
  ref = O_element
FEATURE [App::DocumentObjectGroupPython] G4_BERYLLIUM_OXIDE  # scripted group (container) (typed FeaturePython)
  Dunit = g/cm3
  Dvalue = 3.01
  Group = -> [Be_element001,O_element011]
  conduct = 2
  density = 1
  expand = 3
  formula = G4_BERYLLIUM_OXIDE
  name = G4_BERYLLIUM_OXIDE
  specific = 4
FEATURE [App::DocumentObjectGroupPython] Bi_element001  label="Bi_element : 4"  # scripted group (container) (typed FeaturePython)
  n = 4
  ref = Bi_element
FEATURE [App::DocumentObjectGroupPython] Ge_element001  label="Ge_element : 3"  # scripted group (container) (typed FeaturePython)
  n = 3
  ref = Ge_element
FEATURE [App::DocumentObjectGroupPython] O_element012  label="O_element : 12"  # scripted group (container) (typed FeaturePython)
  n = 12
  ref = O_element
FEATURE [App::DocumentObjectGroupPython] G4_BGO  # scripted group (container) (typed FeaturePython)
  Dunit = g/cm3
  Dvalue = 7.13
  Group = -> [Bi_element001,Ge_element001,O_element012]
  conduct = 2
  density = 1
  expand = 3
  formula = G4_BGO
  name = G4_BGO
  specific = 4
FEATURE [App::DocumentObjectGroupPython] H_element014  label="H_element : 0.102"  # scripted group (container) (typed FeaturePython)
  n = 0.102
FEATURE [App::DocumentObjectGroupPython] C_element014  label="C_element : 0.110"  # scripted group (container) (typed FeaturePython)
  n = 0.11
FEATURE [App::DocumentObjectGroupPython] N_element009  label="N_element : 0.033"  # scripted group (container) (typed FeaturePython)
  n = 0.033
FEATURE [App::DocumentObjectGroupPython] O_element013  label="O_element : 0.745"  # scripted group (container) (typed FeaturePython)
  n = 0.745
FEATURE [App::DocumentObjectGroupPython] Na_element002  label="Na_element : 0.002"  # scripted group (container) (typed FeaturePython)
  n = 0.001
FEATURE [App::DocumentObjectGroupPython] P_element001  label="P_element : 0.001"  # scripted group (container) (typed FeaturePython)
  n = 0.001
FEATURE [App::DocumentObjectGroupPython] S_element003  label="S_element : 0.002"  # scripted group (container) (typed FeaturePython)
  n = 0.002
FEATURE [App::DocumentObjectGroupPython] Cl_element002  label="Cl_element : 0.003"  # scripted group (container) (typed FeaturePython)
  n = 0.003
FEATURE [App::DocumentObjectGroupPython] K_element001  label="K_element : 0.002"  # scripted group (container) (typed FeaturePython)
  n = 0.002
FEATURE [App::DocumentObjectGroupPython] Fe_element001  label="Fe_element : 0.001"  # scripted group (container) (typed FeaturePython)
  n = 0.001
FEATURE [App::DocumentObjectGroupPython] G4_BLOOD_ICRP  # scripted group (container) (typed FeaturePython)
  Dunit = g/cm3
  Dvalue = 1.06
  Group = -> [H_element014,C_element014,N_element009,O_element013,Na_element002,P_element001,S_element003,Cl_element002,K_element001,Fe_element001]
  conduct = 2
  density = 1
  expand = 3
  formula = G4_BLOOD_ICRP
  name = G4_BLOOD_ICRP
  specific = 4
FEATURE [App::DocumentObjectGroupPython] H_element015  label="H_element : 0.064"  # scripted group (container) (typed FeaturePython)
  n = 0.064
FEATURE [App::DocumentObjectGroupPython] C_element015  label="C_element : 0.278"  # scripted group (container) (typed FeaturePython)
  n = 0.278
FEATURE [App::DocumentObjectGroupPython] N_element010  label="N_element : 0.027"  # scripted group (container) (typed FeaturePython)
  n = 0.027
FEATURE [App::DocumentObjectGroupPython] O_element014  label="O_element : 0.410"  # scripted group (container) (typed FeaturePython)
  n = 0.41
FEATURE [App::DocumentObjectGroupPython] Mg_element001  label="Mg_element : 0.002"  # scripted group (container) (typed FeaturePython)
  n = 0.002
FEATURE [App::DocumentObjectGroupPython] P_element002  label="P_element : 0.070"  # scripted group (container) (typed FeaturePython)
  n = 0.07
FEATURE [App::DocumentObjectGroupPython] S_element004  label="S_element : 0.003"  # scripted group (container) (typed FeaturePython)
  n = 0.002
FEATURE [App::DocumentObjectGroupPython] Ca_element003  label="Ca_element : 0.147"  # scripted group (container) (typed FeaturePython)
  n = 0.147
FEATURE [App::DocumentObjectGroupPython] G4_BONE_COMPACT_ICRU  # scripted group (container) (typed FeaturePython)
  Dunit = g/cm3
  Dvalue = 1.85
  Group = -> [H_element015,C_element015,N_element010,O_element014,Mg_element001,P_element002,S_element004,Ca_element003]
  conduct = 2
  density = 1
  expand = 3
  formula = G4_BONE_COMPACT_ICRU
  name = G4_BONE_COMPACT_ICRU
  specific = 4
FEATURE [App::DocumentObjectGroupPython] H_element016  label="H_element : 0.034"  # scripted group (container) (typed FeaturePython)
  n = 0.034
FEATURE [App::DocumentObjectGroupPython] C_element016  label="C_element : 0.155"  # scripted group (container) (typed FeaturePython)
  n = 0.155
FEATURE [App::DocumentObjectGroupPython] N_element011  label="N_element : 0.042"  # scripted group (container) (typed FeaturePython)
  n = 0.042
FEATURE [App::DocumentObjectGroupPython] O_element015  label="O_element : 0.435"  # scripted group (container) (typed FeaturePython)
  n = 0.435
FEATURE [App::DocumentObjectGroupPython] Na_element003  label="Na_element : 0.003"  # scripted group (container) (typed FeaturePython)
  n = 0.001
FEATURE [App::DocumentObjectGroupPython] Mg_element002  label="Mg_element : 0.003"  # scripted group (container) (typed FeaturePython)
  n = 0.002
FEATURE [App::DocumentObjectGroupPython] P_element003  label="P_element : 0.103"  # scripted group (container) (typed FeaturePython)
  n = 0.103
FEATURE [App::DocumentObjectGroupPython] S_element005  label="S_element : 0.004"  # scripted group (container) (typed FeaturePython)
  n = 0.003
FEATURE [App::DocumentObjectGroupPython] Ca_element004  label="Ca_element : 0.225"  # scripted group (container) (typed FeaturePython)
  n = 0.225
FEATURE [App::DocumentObjectGroupPython] G4_BONE_CORTICAL_ICRP  # scripted group (container) (typed FeaturePython)
  Dunit = g/cm3
  Dvalue = 1.92
  Group = -> [H_element016,C_element016,N_element011,O_element015,Na_element003,Mg_element002,P_element003,S_element005,Ca_element004]
  conduct = 2
  density = 1
  expand = 3
  formula = G4_BONE_CORTICAL_ICRP
  name = G4_BONE_CORTICAL_ICRP
  specific = 4
FEATURE [App::DocumentObjectGroupPython] B_element001  label="B_element : 4"  # scripted group (container) (typed FeaturePython)
  n = 4
  ref = B_element
FEATURE [App::DocumentObjectGroupPython] C_element017  label="C_element : 1"  # scripted group (container) (typed FeaturePython)
  n = 1
  ref = C_element
FEATURE [App::DocumentObjectGroupPython] G4_BORON_CARBIDE  # scripted group (container) (typed FeaturePython)
  Dunit = g/cm3
  Dvalue = 2.52
  Group = -> [B_element001,C_element017]
  conduct = 2
  density = 1
  expand = 3
  formula = G4_BORON_CARBIDE
  name = G4_BORON_CARBIDE
  specific = 4
FEATURE [App::DocumentObjectGroupPython] B_element002  label="B_element : 2"  # scripted group (container) (typed FeaturePython)
  n = 2
  ref = B_element
FEATURE [App::DocumentObjectGroupPython] O_element016  label="O_element : 006"  # scripted group (container) (typed FeaturePython)
  n = 3
  ref = O_element
FEATURE [App::DocumentObjectGroupPython] G4_BORON_OXIDE  # scripted group (container) (typed FeaturePython)
  Dunit = g/cm3
  Dvalue = 1.812
  Group = -> [B_element002,O_element016]
  conduct = 2
  density = 1
  expand = 3
  formula = G4_BORON_OXIDE
  name = G4_BORON_OXIDE
  specific = 4
FEATURE [App::DocumentObjectGroupPython] H_element017  label="H_element : 0.107"  # scripted group (container) (typed FeaturePython)
  n = 0.107
FEATURE [App::DocumentObjectGroupPython] C_element018  label="C_element : 0.145"  # scripted group (container) (typed FeaturePython)
  n = 0.145
FEATURE [App::DocumentObjectGroupPython] N_element012  label="N_element : 0.022"  # scripted group (container) (typed FeaturePython)
  n = 0.022
FEATURE [App::DocumentObjectGroupPython] O_element017  label="O_element : 0.712"  # scripted group (container) (typed FeaturePython)
  n = 0.712
FEATURE [App::DocumentObjectGroupPython] Na_element004  label="Na_element : 0.004"  # scripted group (container) (typed FeaturePython)
  n = 0.002
FEATURE [App::DocumentObjectGroupPython] P_element004  label="P_element : 0.004"  # scripted group (container) (typed FeaturePython)
  n = 0.004
FEATURE [App::DocumentObjectGroupPython] S_element006  label="S_element : 0.005"  # scripted group (container) (typed FeaturePython)
  n = 0.002
FEATURE [App::DocumentObjectGroupPython] Cl_element003  label="Cl_element : 0.004"  # scripted group (container) (typed FeaturePython)
  n = 0.003
FEATURE [App::DocumentObjectGroupPython] K_element002  label="K_element : 0.003"  # scripted group (container) (typed FeaturePython)
  n = 0.003
FEATURE [App::DocumentObjectGroupPython] G4_BRAIN_ICRP  # scripted group (container) (typed FeaturePython)
  Dunit = g/cm3
  Dvalue = 1.04
  Group = -> [H_element017,C_element018,N_element012,O_element017,Na_element004,P_element004,S_element006,Cl_element003,K_element002]
  conduct = 2
  density = 1
  expand = 3
  formula = G4_BRAIN_ICRP
  name = G4_BRAIN_ICRP
  specific = 4
FEATURE [App::DocumentObjectGroupPython] C_element019  label="C_element : 4"  # scripted group (container) (typed FeaturePython)
  n = 4
  ref = C_element
FEATURE [App::DocumentObjectGroupPython] H_element018  label="H_element : 010"  # scripted group (container) (typed FeaturePython)
  n = 10
  ref = H_element
FEATURE [App::DocumentObjectGroupPython] G4_BUTANE  # scripted group (container) (typed FeaturePython)
  Dunit = g/cm3
  Dvalue = 0.00249343
  Group = -> [C_element019,H_element018]
  conduct = 2
  density = 1
  expand = 3
  formula = G4_BUTANE
  name = G4_BUTANE
  specific = 4
FEATURE [App::DocumentObjectGroupPython] C_element020  label="C_element : 008"  # scripted group (container) (typed FeaturePython)
  n = 4
  ref = C_element
FEATURE [App::DocumentObjectGroupPython] H_element019  label="H_element : 011"  # scripted group (container) (typed FeaturePython)
  n = 10
  ref = H_element
FEATURE [App::DocumentObjectGroupPython] O_element018  label="O_element : 007"  # scripted group (container) (typed FeaturePython)
  n = 1
  ref = O_element
FEATURE [App::DocumentObjectGroupPython] G4_N_BUTYL_ALCOHOL  label="G4_N-BUTYL_ALCOHOL"  # scripted group (container) (typed FeaturePython)
  Dunit = g/cm3
  Dvalue = 0.8098
  Group = -> [C_element020,H_element019,O_element018]
  conduct = 2
  density = 1
  expand = 3
  formula = G4_N-BUTYL_ALCOHOL
  name = G4_N-BUTYL_ALCOHOL
  specific = 4
FEATURE [App::DocumentObjectGroupPython] H_element020  label="H_element : 0.025"  # scripted group (container) (typed FeaturePython)
  n = 0.02468
FEATURE [App::DocumentObjectGroupPython] C_element021  label="C_element : 0.502"  # scripted group (container) (typed FeaturePython)
  n = 0.501611
FEATURE [App::DocumentObjectGroupPython] O_element019  label="O_element : 0.005"  # scripted group (container) (typed FeaturePython)
  n = 0.004527
FEATURE [App::DocumentObjectGroupPython] F_element004  label="F_element : 0.465"  # scripted group (container) (typed FeaturePython)
  n = 0.465209
FEATURE [App::DocumentObjectGroupPython] Si_element001  label="Si_element : 0.004"  # scripted group (container) (typed FeaturePython)
  n = 0.003973
FEATURE [App::DocumentObjectGroupPython] G4_C_552  label="G4_C-552"  # scripted group (container) (typed FeaturePython)
  Dunit = g/cm3
  Dvalue = 1.76
  Group = -> [H_element020,C_element021,O_element019,F_element004,Si_element001]
  conduct = 2
  density = 1
  expand = 3
  formula = G4_C-552
  name = G4_C-552
  specific = 4
FEATURE [App::DocumentObjectGroupPython] Cd_element001  label="Cd_element : 1"  # scripted group (container) (typed FeaturePython)
  n = 1
  ref = Cd_element
FEATURE [App::DocumentObjectGroupPython] Te_element001  label="Te_element : 1"  # scripted group (container) (typed FeaturePython)
  n = 1
  ref = Te_element
FEATURE [App::DocumentObjectGroupPython] G4_CADMIUM_TELLURIDE  # scripted group (container) (typed FeaturePython)
  Dunit = g/cm3
  Dvalue = 6.2
  Group = -> [Cd_element001,Te_element001]
  conduct = 2
  density = 1
  expand = 3
  formula = G4_CADMIUM_TELLURIDE
  name = G4_CADMIUM_TELLURIDE
  specific = 4
FEATURE [App::DocumentObjectGroupPython] Cd_element002  label="Cd_element : 002"  # scripted group (container) (typed FeaturePython)
  n = 1
  ref = Cd_element
FEATURE [App::DocumentObjectGroupPython] W_element001  label="W_element : 1"  # scripted group (container) (typed FeaturePython)
  n = 1
  ref = W_element
FEATURE [App::DocumentObjectGroupPython] O_element020  label="O_element : 008"  # scripted group (container) (typed FeaturePython)
  n = 4
  ref = O_element
FEATURE [App::DocumentObjectGroupPython] G4_CADMIUM_TUNGSTATE  # scripted group (container) (typed FeaturePython)
  Dunit = g/cm3
  Dvalue = 7.9
  Group = -> [Cd_element002,W_element001,O_element020]
  conduct = 2
  density = 1
  expand = 3
  formula = G4_CADMIUM_TUNGSTATE
  name = G4_CADMIUM_TUNGSTATE
  specific = 4
FEATURE [App::DocumentObjectGroupPython] Ca_element005  label="Ca_element : 1"  # scripted group (container) (typed FeaturePython)
  n = 1
  ref = Ca_element
FEATURE [App::DocumentObjectGroupPython] C_element022  label="C_element : 009"  # scripted group (container) (typed FeaturePython)
  n = 1
  ref = C_element
FEATURE [App::DocumentObjectGroupPython] O_element021  label="O_element : 009"  # scripted group (container) (typed FeaturePython)
  n = 3
  ref = O_element
FEATURE [App::DocumentObjectGroupPython] G4_CALCIUM_CARBONATE  # scripted group (container) (typed FeaturePython)
  Dunit = g/cm3
  Dvalue = 2.8
  Group = -> [Ca_element005,C_element022,O_element021]
  conduct = 2
  density = 1
  expand = 3
  formula = G4_CALCIUM_CARBONATE
  name = G4_CALCIUM_CARBONATE
  specific = 4
FEATURE [App::DocumentObjectGroupPython] Ca_element006  label="Ca_element : 002"  # scripted group (container) (typed FeaturePython)
  n = 1
  ref = Ca_element
FEATURE [App::DocumentObjectGroupPython] F_element005  label="F_element : 003"  # scripted group (container) (typed FeaturePython)
  n = 2
  ref = F_element
FEATURE [App::DocumentObjectGroupPython] G4_CALCIUM_FLUORIDE  # scripted group (container) (typed FeaturePython)
  Dunit = g/cm3
  Dvalue = 3.18
  Group = -> [Ca_element006,F_element005]
  conduct = 2
  density = 1
  expand = 3
  formula = G4_CALCIUM_FLUORIDE
  name = G4_CALCIUM_FLUORIDE
  specific = 4
FEATURE [App::DocumentObjectGroupPython] Ca_element007  label="Ca_element : 003"  # scripted group (container) (typed FeaturePython)
  n = 1
  ref = Ca_element
FEATURE [App::DocumentObjectGroupPython] O_element022  label="O_element : 010"  # scripted group (container) (typed FeaturePython)
  n = 1
  ref = O_element
FEATURE [App::DocumentObjectGroupPython] G4_CALCIUM_OXIDE  # scripted group (container) (typed FeaturePython)
  Dunit = g/cm3
  Dvalue = 3.3
  Group = -> [Ca_element007,O_element022]
  conduct = 2
  density = 1
  expand = 3
  formula = G4_CALCIUM_OXIDE
  name = G4_CALCIUM_OXIDE
  specific = 4
FEATURE [App::DocumentObjectGroupPython] Ca_element008  label="Ca_element : 004"  # scripted group (container) (typed FeaturePython)
  n = 1
  ref = Ca_element
FEATURE [App::DocumentObjectGroupPython] S_element007  label="S_element : 002"  # scripted group (container) (typed FeaturePython)
  n = 1
  ref = S_element
FEATURE [App::DocumentObjectGroupPython] O_element023  label="O_element : 011"  # scripted group (container) (typed FeaturePython)
  n = 4
  ref = O_element
FEATURE [App::DocumentObjectGroupPython] G4_CALCIUM_SULFATE  # scripted group (container) (typed FeaturePython)
  Dunit = g/cm3
  Dvalue = 2.96
  Group = -> [Ca_element008,S_element007,O_element023]
  conduct = 2
  density = 1
  expand = 3
  formula = G4_CALCIUM_SULFATE
  name = G4_CALCIUM_SULFATE
  specific = 4
FEATURE [App::DocumentObjectGroupPython] Ca_element009  label="Ca_element : 005"  # scripted group (container) (typed FeaturePython)
  n = 1
  ref = Ca_element
FEATURE [App::DocumentObjectGroupPython] W_element002  label="W_element : 002"  # scripted group (container) (typed FeaturePython)
  n = 1
  ref = W_element
FEATURE [App::DocumentObjectGroupPython] O_element024  label="O_element : 012"  # scripted group (container) (typed FeaturePython)
  n = 4
  ref = O_element
FEATURE [App::DocumentObjectGroupPython] G4_CALCIUM_TUNGSTATE  # scripted group (container) (typed FeaturePython)
  Dunit = g/cm3
  Dvalue = 6.062
  Group = -> [Ca_element009,W_element002,O_element024]
  conduct = 2
  density = 1
  expand = 3
  formula = G4_CALCIUM_TUNGSTATE
  name = G4_CALCIUM_TUNGSTATE
  specific = 4
FEATURE [App::DocumentObjectGroupPython] C_element023  label="C_element : 010"  # scripted group (container) (typed FeaturePython)
  n = 1
  ref = C_element
FEATURE [App::DocumentObjectGroupPython] O_element025  label="O_element : 013"  # scripted group (container) (typed FeaturePython)
  n = 2
  ref = O_element
FEATURE [App::DocumentObjectGroupPython] G4_CARBON_DIOXIDE  # scripted group (container) (typed FeaturePython)
  Dunit = g/cm3
  Dvalue = 0.00184212
  Group = -> [C_element023,O_element025]
  conduct = 2
  density = 1
  expand = 3
  formula = G4_CARBON_DIOXIDE
  name = G4_CARBON_DIOXIDE
  specific = 4
FEATURE [App::DocumentObjectGroupPython] C_element024  label="C_element : 011"  # scripted group (container) (typed FeaturePython)
  n = 1
  ref = C_element
FEATURE [App::DocumentObjectGroupPython] Cl_element004  label="Cl_element : 4"  # scripted group (container) (typed FeaturePython)
  n = 4
  ref = Cl_element
FEATURE [App::DocumentObjectGroupPython] G4_CARBON_TETRACHLORIDE  # scripted group (container) (typed FeaturePython)
  Dunit = g/cm3
  Dvalue = 1.594
  Group = -> [C_element024,Cl_element004]
  conduct = 2
  density = 1
  expand = 3
  formula = G4_CARBON_TETRACHLORIDE
  name = G4_CARBON_TETRACHLORIDE
  specific = 4
FEATURE [App::DocumentObjectGroupPython] C_element025  label="C_element : 012"  # scripted group (container) (typed FeaturePython)
  n = 6
  ref = C_element
FEATURE [App::DocumentObjectGroupPython] H_element021  label="H_element : 012"  # scripted group (container) (typed FeaturePython)
  n = 10
  ref = H_element
FEATURE [App::DocumentObjectGroupPython] O_element026  label="O_element : 5"  # scripted group (container) (typed FeaturePython)
  n = 5
  ref = O_element
FEATURE [App::DocumentObjectGroupPython] G4_CELLULOSE_CELLOPHANE  # scripted group (container) (typed FeaturePython)
  Dunit = g/cm3
  Dvalue = 1.42
  Group = -> [C_element025,H_element021,O_element026]
  conduct = 2
  density = 1
  expand = 3
  formula = G4_CELLULOSE_CELLOPHANE
  name = G4_CELLULOSE_CELLOPHANE
  specific = 4
FEATURE [App::DocumentObjectGroupPython] H_element022  label="H_element : 0.067"  # scripted group (container) (typed FeaturePython)
  n = 0.067125
FEATURE [App::DocumentObjectGroupPython] C_element026  label="C_element : 0.545"  # scripted group (container) (typed FeaturePython)
  n = 0.545403
FEATURE [App::DocumentObjectGroupPython] O_element027  label="O_element : 0.387"  # scripted group (container) (typed FeaturePython)
  n = 0.387472
FEATURE [App::DocumentObjectGroupPython] G4_CELLULOSE_BUTYRATE  # scripted group (container) (typed FeaturePython)
  Dunit = g/cm3
  Dvalue = 1.2
  Group = -> [H_element022,C_element026,O_element027]
  conduct = 2
  density = 1
  expand = 3
  formula = G4_CELLULOSE_BUTYRATE
  name = G4_CELLULOSE_BUTYRATE
  specific = 4
FEATURE [App::DocumentObjectGroupPython] H_element023  label="H_element : 0.029"  # scripted group (container) (typed FeaturePython)
  n = 0.029216
FEATURE [App::DocumentObjectGroupPython] C_element027  label="C_element : 0.271"  # scripted group (container) (typed FeaturePython)
  n = 0.271296
FEATURE [App::DocumentObjectGroupPython] N_element013  label="N_element : 0.121"  # scripted group (container) (typed FeaturePython)
  n = 0.121276
FEATURE [App::DocumentObjectGroupPython] O_element028  label="O_element : 0.578"  # scripted group (container) (typed FeaturePython)
  n = 0.578212
FEATURE [App::DocumentObjectGroupPython] G4_CELLULOSE_NITRATE  # scripted group (container) (typed FeaturePython)
  Dunit = g/cm3
  Dvalue = 1.49
  Group = -> [H_element023,C_element027,N_element013,O_element028]
  conduct = 2
  density = 1
  expand = 3
  formula = G4_CELLULOSE_NITRATE
  name = G4_CELLULOSE_NITRATE
  specific = 4
FEATURE [App::DocumentObjectGroupPython] H_element024  label="H_element : 0.108"  # scripted group (container) (typed FeaturePython)
  n = 0.107596
FEATURE [App::DocumentObjectGroupPython] N_element014  label="N_element : 0.001"  # scripted group (container) (typed FeaturePython)
  n = 0.0008
FEATURE [App::DocumentObjectGroupPython] O_element029  label="O_element : 0.875"  # scripted group (container) (typed FeaturePython)
  n = 0.874976
FEATURE [App::DocumentObjectGroupPython] S_element008  label="S_element : 0.015"  # scripted group (container) (typed FeaturePython)
  n = 0.014627
FEATURE [App::DocumentObjectGroupPython] Ce_element001  label="Ce_element : 0.002"  # scripted group (container) (typed FeaturePython)
  n = 0.002001
FEATURE [App::DocumentObjectGroupPython] G4_CERIC_SULFATE  # scripted group (container) (typed FeaturePython)
  Dunit = g/cm3
  Dvalue = 1.03
  Group = -> [H_element024,N_element014,O_element029,S_element008,Ce_element001]
  conduct = 2
  density = 1
  expand = 3
  formula = G4_CERIC_SULFATE
  name = G4_CERIC_SULFATE
  specific = 4
FEATURE [App::DocumentObjectGroupPython] Cs_element001  label="Cs_element : 1"  # scripted group (container) (typed FeaturePython)
  n = 1
  ref = Cs_element
FEATURE [App::DocumentObjectGroupPython] F_element006  label="F_element : 1"  # scripted group (container) (typed FeaturePython)
  n = 1
  ref = F_element
FEATURE [App::DocumentObjectGroupPython] G4_CESIUM_FLUORIDE  # scripted group (container) (typed FeaturePython)
  Dunit = g/cm3
  Dvalue = 4.115
  Group = -> [Cs_element001,F_element006]
  conduct = 2
  density = 1
  expand = 3
  formula = G4_CESIUM_FLUORIDE
  name = G4_CESIUM_FLUORIDE
  specific = 4
FEATURE [App::DocumentObjectGroupPython] Cs_element002  label="Cs_element : 002"  # scripted group (container) (typed FeaturePython)
  n = 1
  ref = Cs_element
FEATURE [App::DocumentObjectGroupPython] I_element001  label="I_element : 1"  # scripted group (container) (typed FeaturePython)
  n = 1
  ref = I_element
FEATURE [App::DocumentObjectGroupPython] G4_CESIUM_IODIDE  # scripted group (container) (typed FeaturePython)
  Dunit = g/cm3
  Dvalue = 4.51
  Group = -> [Cs_element002,I_element001]
  conduct = 2
  density = 1
  expand = 3
  formula = G4_CESIUM_IODIDE
  name = G4_CESIUM_IODIDE
  specific = 4
FEATURE [App::DocumentObjectGroupPython] C_element028  label="C_element : 013"  # scripted group (container) (typed FeaturePython)
  n = 6
  ref = C_element
FEATURE [App::DocumentObjectGroupPython] H_element025  label="H_element : 013"  # scripted group (container) (typed FeaturePython)
  n = 5
  ref = H_element
FEATURE [App::DocumentObjectGroupPython] Cl_element005  label="Cl_element : 1"  # scripted group (container) (typed FeaturePython)
  n = 1
  ref = Cl_element
FEATURE [App::DocumentObjectGroupPython] G4_CHLOROBENZENE  # scripted group (container) (typed FeaturePython)
  Dunit = g/cm3
  Dvalue = 1.1058
  Group = -> [C_element028,H_element025,Cl_element005]
  conduct = 2
  density = 1
  expand = 3
  formula = G4_CHLOROBENZENE
  name = G4_CHLOROBENZENE
  specific = 4
FEATURE [App::DocumentObjectGroupPython] C_element029  label="C_element : 014"  # scripted group (container) (typed FeaturePython)
  n = 1
  ref = C_element
FEATURE [App::DocumentObjectGroupPython] H_element026  label="H_element : 1"  # scripted group (container) (typed FeaturePython)
  n = 1
  ref = H_element
FEATURE [App::DocumentObjectGroupPython] Cl_element006  label="Cl_element : 3"  # scripted group (container) (typed FeaturePython)
  n = 3
  ref = Cl_element
FEATURE [App::DocumentObjectGroupPython] G4_CHLOROFORM  # scripted group (container) (typed FeaturePython)
  Dunit = g/cm3
  Dvalue = 1.4832
  Group = -> [C_element029,H_element026,Cl_element006]
  conduct = 2
  density = 1
  expand = 3
  formula = G4_CHLOROFORM
  name = G4_CHLOROFORM
  specific = 4
FEATURE [App::DocumentObjectGroupPython] H_element027  label="H_element : 0.010"  # scripted group (container) (typed FeaturePython)
  n = 0.01
FEATURE [App::DocumentObjectGroupPython] C_element030  label="C_element : 0.001"  # scripted group (container) (typed FeaturePython)
  n = 0.001
FEATURE [App::DocumentObjectGroupPython] O_element030  label="O_element : 0.529"  # scripted group (container) (typed FeaturePython)
  n = 0.529107
FEATURE [App::DocumentObjectGroupPython] Na_element005  label="Na_element : 0.016"  # scripted group (container) (typed FeaturePython)
  n = 0.016
FEATURE [App::DocumentObjectGroupPython] Mg_element003  label="Mg_element : 0.004"  # scripted group (container) (typed FeaturePython)
  n = 0.002
FEATURE [App::DocumentObjectGroupPython] Al_element002  label="Al_element : 0.034"  # scripted group (container) (typed FeaturePython)
  n = 0.033872
FEATURE [App::DocumentObjectGroupPython] Si_element002  label="Si_element : 0.337"  # scripted group (container) (typed FeaturePython)
  n = 0.337021
FEATURE [App::DocumentObjectGroupPython] K_element003  label="K_element : 0.013"  # scripted group (container) (typed FeaturePython)
  n = 0.013
FEATURE [App::DocumentObjectGroupPython] Ca_element010  label="Ca_element : 0.044"  # scripted group (container) (typed FeaturePython)
  n = 0.044
FEATURE [App::DocumentObjectGroupPython] Fe_element002  label="Fe_element : 0.014"  # scripted group (container) (typed FeaturePython)
  n = 0.014
FEATURE [App::DocumentObjectGroupPython] G4_CONCRETE  # scripted group (container) (typed FeaturePython)
  Dunit = g/cm3
  Dvalue = 2.3
  Group = -> [H_element027,C_element030,O_element030,Na_element005,Mg_element003,Al_element002,Si_element002,K_element003,Ca_element010,Fe_element002]
  conduct = 2
  density = 1
  expand = 3
  formula = G4_CONCRETE
  name = G4_CONCRETE
  specific = 4
FEATURE [App::DocumentObjectGroupPython] C_element031  label="C_element : 015"  # scripted group (container) (typed FeaturePython)
  n = 6
  ref = C_element
FEATURE [App::DocumentObjectGroupPython] H_element028  label="H_element : 12"  # scripted group (container) (typed FeaturePython)
  n = 12
  ref = H_element
FEATURE [App::DocumentObjectGroupPython] G4_CYCLOHEXANE  # scripted group (container) (typed FeaturePython)
  Dunit = g/cm3
  Dvalue = 0.779
  Group = -> [C_element031,H_element028]
  conduct = 2
  density = 1
  expand = 3
  formula = G4_CYCLOHEXANE
  name = G4_CYCLOHEXANE
  specific = 4
FEATURE [App::DocumentObjectGroupPython] C_element032  label="C_element : 016"  # scripted group (container) (typed FeaturePython)
  n = 6
  ref = C_element
FEATURE [App::DocumentObjectGroupPython] H_element029  label="H_element : 4"  # scripted group (container) (typed FeaturePython)
  n = 4
  ref = H_element
FEATURE [App::DocumentObjectGroupPython] Cl_element007  label="Cl_element : 2"  # scripted group (container) (typed FeaturePython)
  n = 2
  ref = Cl_element
FEATURE [App::DocumentObjectGroupPython] G4_1_2_DICHLOROBENZENE  label="G4_1.2-DICHLOROBENZENE"  # scripted group (container) (typed FeaturePython)
  Dunit = g/cm3
  Dvalue = 1.3048
  Group = -> [C_element032,H_element029,Cl_element007]
  conduct = 2
  density = 1
  expand = 3
  formula = G4_1.2-DICHLOROBENZENE
  name = G4_1.2-DICHLOROBENZENE
  specific = 4
FEATURE [App::DocumentObjectGroupPython] C_element033  label="C_element : 017"  # scripted group (container) (typed FeaturePython)
  n = 4
  ref = C_element
FEATURE [App::DocumentObjectGroupPython] H_element030  label="H_element : 8"  # scripted group (container) (typed FeaturePython)
  n = 8
  ref = H_element
FEATURE [App::DocumentObjectGroupPython] O_element031  label="O_element : 014"  # scripted group (container) (typed FeaturePython)
  n = 1
  ref = O_element
FEATURE [App::DocumentObjectGroupPython] Cl_element008  label="Cl_element : 005"  # scripted group (container) (typed FeaturePython)
  n = 2
  ref = Cl_element
FEATURE [App::DocumentObjectGroupPython] G4_DICHLORODIETHYL_ETHER  # scripted group (container) (typed FeaturePython)
  Dunit = g/cm3
  Dvalue = 1.2199
  Group = -> [C_element033,H_element030,O_element031,Cl_element008]
  conduct = 2
  density = 1
  expand = 3
  formula = G4_DICHLORODIETHYL_ETHER
  name = G4_DICHLORODIETHYL_ETHER
  specific = 4
FEATURE [App::DocumentObjectGroupPython] C_element034  label="C_element : 018"  # scripted group (container) (typed FeaturePython)
  n = 2
  ref = C_element
FEATURE [App::DocumentObjectGroupPython] H_element031  label="H_element : 014"  # scripted group (container) (typed FeaturePython)
  n = 4
  ref = H_element
FEATURE [App::DocumentObjectGroupPython] Cl_element009  label="Cl_element : 006"  # scripted group (container) (typed FeaturePython)
  n = 2
  ref = Cl_element
FEATURE [App::DocumentObjectGroupPython] G4_1_2_DICHLOROETHANE  label="G4_1.2-DICHLOROETHANE"  # scripted group (container) (typed FeaturePython)
  Dunit = g/cm3
  Dvalue = 1.2351
  Group = -> [C_element034,H_element031,Cl_element009]
  conduct = 2
  density = 1
  expand = 3
  formula = G4_1.2-DICHLOROETHANE
  name = G4_1.2-DICHLOROETHANE
  specific = 4
FEATURE [App::DocumentObjectGroupPython] C_element035  label="C_element : 019"  # scripted group (container) (typed FeaturePython)
  n = 4
  ref = C_element
FEATURE [App::DocumentObjectGroupPython] H_element032  label="H_element : 015"  # scripted group (container) (typed FeaturePython)
  n = 10
  ref = H_element
FEATURE [App::DocumentObjectGroupPython] O_element032  label="O_element : 015"  # scripted group (container) (typed FeaturePython)
  n = 1
  ref = O_element
FEATURE [App::DocumentObjectGroupPython] G4_DIETHYL_ETHER  # scripted group (container) (typed FeaturePython)
  Dunit = g/cm3
  Dvalue = 0.71378
  Group = -> [C_element035,H_element032,O_element032]
  conduct = 2
  density = 1
  expand = 3
  formula = G4_DIETHYL_ETHER
  name = G4_DIETHYL_ETHER
  specific = 4
FEATURE [App::DocumentObjectGroupPython] C_element036  label="C_element : 020"  # scripted group (container) (typed FeaturePython)
  n = 3
  ref = C_element
FEATURE [App::DocumentObjectGroupPython] H_element033  label="H_element : 016"  # scripted group (container) (typed FeaturePython)
  n = 7
  ref = H_element
FEATURE [App::DocumentObjectGroupPython] N_element015  label="N_element : 008"  # scripted group (container) (typed FeaturePython)
  n = 1
  ref = N_element
FEATURE [App::DocumentObjectGroupPython] O_element033  label="O_element : 016"  # scripted group (container) (typed FeaturePython)
  n = 1
  ref = O_element
FEATURE [App::DocumentObjectGroupPython] G4_N_N_DIMETHYL_FORMAMIDE  label="G4_N.N-DIMETHYL_FORMAMIDE"  # scripted group (container) (typed FeaturePython)
  Dunit = g/cm3
  Dvalue = 0.9487
  Group = -> [C_element036,H_element033,N_element015,O_element033]
  conduct = 2
  density = 1
  expand = 3
  formula = G4_N.N-DIMETHYL_FORMAMIDE
  name = G4_N.N-DIMETHYL_FORMAMIDE
  specific = 4
FEATURE [App::DocumentObjectGroupPython] C_element037  label="C_element : 021"  # scripted group (container) (typed FeaturePython)
  n = 2
  ref = C_element
FEATURE [App::DocumentObjectGroupPython] H_element034  label="H_element : 017"  # scripted group (container) (typed FeaturePython)
  n = 6
  ref = H_element
FEATURE [App::DocumentObjectGroupPython] O_element034  label="O_element : 017"  # scripted group (container) (typed FeaturePython)
  n = 1
  ref = O_element
FEATURE [App::DocumentObjectGroupPython] S_element009  label="S_element : 003"  # scripted group (container) (typed FeaturePython)
  n = 1
  ref = S_element
FEATURE [App::DocumentObjectGroupPython] G4_DIMETHYL_SULFOXIDE  # scripted group (container) (typed FeaturePython)
  Dunit = g/cm3
  Dvalue = 1.1014
  Group = -> [C_element037,H_element034,O_element034,S_element009]
  conduct = 2
  density = 1
  expand = 3
  formula = G4_DIMETHYL_SULFOXIDE
  name = G4_DIMETHYL_SULFOXIDE
  specific = 4
FEATURE [App::DocumentObjectGroupPython] C_element038  label="C_element : 022"  # scripted group (container) (typed FeaturePython)
  n = 2
  ref = C_element
FEATURE [App::DocumentObjectGroupPython] H_element035  label="H_element : 018"  # scripted group (container) (typed FeaturePython)
  n = 6
  ref = H_element
FEATURE [App::DocumentObjectGroupPython] G4_ETHANE  # scripted group (container) (typed FeaturePython)
  Dunit = g/cm3
  Dvalue = 0.00125324
  Group = -> [C_element038,H_element035]
  conduct = 2
  density = 1
  expand = 3
  formula = G4_ETHANE
  name = G4_ETHANE
  specific = 4
FEATURE [App::DocumentObjectGroupPython] C_element039  label="C_element : 023"  # scripted group (container) (typed FeaturePython)
  n = 2
  ref = C_element
FEATURE [App::DocumentObjectGroupPython] H_element036  label="H_element : 019"  # scripted group (container) (typed FeaturePython)
  n = 6
  ref = H_element
FEATURE [App::DocumentObjectGroupPython] O_element035  label="O_element : 018"  # scripted group (container) (typed FeaturePython)
  n = 1
  ref = O_element
FEATURE [App::DocumentObjectGroupPython] G4_ETHYL_ALCOHOL  # scripted group (container) (typed FeaturePython)
  Dunit = g/cm3
  Dvalue = 0.7893
  Group = -> [C_element039,H_element036,O_element035]
  conduct = 2
  density = 1
  expand = 3
  formula = G4_ETHYL_ALCOHOL
  name = G4_ETHYL_ALCOHOL
  specific = 4
FEATURE [App::DocumentObjectGroupPython] H_element037  label="H_element : 0.090"  # scripted group (container) (typed FeaturePython)
  n = 0.090027
FEATURE [App::DocumentObjectGroupPython] C_element040  label="C_element : 0.585"  # scripted group (container) (typed FeaturePython)
  n = 0.585182
FEATURE [App::DocumentObjectGroupPython] O_element036  label="O_element : 0.325"  # scripted group (container) (typed FeaturePython)
  n = 0.324791
FEATURE [App::DocumentObjectGroupPython] G4_ETHYL_CELLULOSE  # scripted group (container) (typed FeaturePython)
  Dunit = g/cm3
  Dvalue = 1.13
  Group = -> [H_element037,C_element040,O_element036]
  conduct = 2
  density = 1
  expand = 3
  formula = G4_ETHYL_CELLULOSE
  name = G4_ETHYL_CELLULOSE
  specific = 4
FEATURE [App::DocumentObjectGroupPython] C_element041  label="C_element : 024"  # scripted group (container) (typed FeaturePython)
  n = 2
  ref = C_element
FEATURE [App::DocumentObjectGroupPython] H_element038  label="H_element : 020"  # scripted group (container) (typed FeaturePython)
  n = 4
  ref = H_element
FEATURE [App::DocumentObjectGroupPython] G4_ETHYLENE  # scripted group (container) (typed FeaturePython)
  Dunit = g/cm3
  Dvalue = 0.00117497
  Group = -> [C_element041,H_element038]
  conduct = 2
  density = 1
  expand = 3
  formula = G4_ETHYLENE
  name = G4_ETHYLENE
  specific = 4
FEATURE [App::DocumentObjectGroupPython] H_element039  label="H_element : 0.096"  # scripted group (container) (typed FeaturePython)
  n = 0.096
FEATURE [App::DocumentObjectGroupPython] C_element042  label="C_element : 0.195"  # scripted group (container) (typed FeaturePython)
  n = 0.195
FEATURE [App::DocumentObjectGroupPython] N_element016  label="N_element : 0.057"  # scripted group (container) (typed FeaturePython)
  n = 0.057
FEATURE [App::DocumentObjectGroupPython] O_element037  label="O_element : 0.646"  # scripted group (container) (typed FeaturePython)
  n = 0.646
FEATURE [App::DocumentObjectGroupPython] Na_element006  label="Na_element : 0.017"  # scripted group (container) (typed FeaturePython)
  n = 0.001
FEATURE [App::DocumentObjectGroupPython] P_element005  label="P_element : 0.104"  # scripted group (container) (typed FeaturePython)
  n = 0.001
FEATURE [App::DocumentObjectGroupPython] S_element010  label="S_element : 0.016"  # scripted group (container) (typed FeaturePython)
  n = 0.003
FEATURE [App::DocumentObjectGroupPython] Cl_element010  label="Cl_element : 0.005"  # scripted group (container) (typed FeaturePython)
  n = 0.001
FEATURE [App::DocumentObjectGroupPython] G4_EYE_LENS_ICRP  # scripted group (container) (typed FeaturePython)
  Dunit = g/cm3
  Dvalue = 1.07
  Group = -> [H_element039,C_element042,N_element016,O_element037,Na_element006,P_element005,S_element010,Cl_element010]
  conduct = 2
  density = 1
  expand = 3
  formula = G4_EYE_LENS_ICRP
  name = G4_EYE_LENS_ICRP
  specific = 4
FEATURE [App::DocumentObjectGroupPython] Fe_element003  label="Fe_element : 2"  # scripted group (container) (typed FeaturePython)
  n = 2
  ref = Fe_element
FEATURE [App::DocumentObjectGroupPython] O_element038  label="O_element : 019"  # scripted group (container) (typed FeaturePython)
  n = 3
  ref = O_element
FEATURE [App::DocumentObjectGroupPython] G4_FERRIC_OXIDE  # scripted group (container) (typed FeaturePython)
  Dunit = g/cm3
  Dvalue = 5.2
  Group = -> [Fe_element003,O_element038]
  conduct = 2
  density = 1
  expand = 3
  formula = G4_FERRIC_OXIDE
  name = G4_FERRIC_OXIDE
  specific = 4
FEATURE [App::DocumentObjectGroupPython] Fe_element004  label="Fe_element : 1"  # scripted group (container) (typed FeaturePython)
  n = 1
  ref = Fe_element
FEATURE [App::DocumentObjectGroupPython] B_element003  label="B_element : 1"  # scripted group (container) (typed FeaturePython)
  n = 1
  ref = B_element
FEATURE [App::DocumentObjectGroupPython] G4_FERROBORIDE  # scripted group (container) (typed FeaturePython)
  Dunit = g/cm3
  Dvalue = 7.15
  Group = -> [Fe_element004,B_element003]
  conduct = 2
  density = 1
  expand = 3
  formula = G4_FERROBORIDE
  name = G4_FERROBORIDE
  specific = 4
FEATURE [App::DocumentObjectGroupPython] Fe_element005  label="Fe_element : 003"  # scripted group (container) (typed FeaturePython)
  n = 1
  ref = Fe_element
FEATURE [App::DocumentObjectGroupPython] O_element039  label="O_element : 020"  # scripted group (container) (typed FeaturePython)
  n = 1
  ref = O_element
FEATURE [App::DocumentObjectGroupPython] G4_FERROUS_OXIDE  # scripted group (container) (typed FeaturePython)
  Dunit = g/cm3
  Dvalue = 5.7
  Group = -> [Fe_element005,O_element039]
  conduct = 2
  density = 1
  expand = 3
  formula = G4_FERROUS_OXIDE
  name = G4_FERROUS_OXIDE
  specific = 4
FEATURE [App::DocumentObjectGroupPython] H_element040  label="H_element : 0.115"  # scripted group (container) (typed FeaturePython)
  n = 0.108259
FEATURE [App::DocumentObjectGroupPython] N_element017  label="N_element : 0.000"  # scripted group (container) (typed FeaturePython)
  n = 2.7e-05
FEATURE [App::DocumentObjectGroupPython] O_element040  label="O_element : 0.879"  # scripted group (container) (typed FeaturePython)
  n = 0.878636
FEATURE [App::DocumentObjectGroupPython] Na_element007  label="Na_element : 0.000"  # scripted group (container) (typed FeaturePython)
  n = 2.2e-05
FEATURE [App::DocumentObjectGroupPython] S_element011  label="S_element : 0.013"  # scripted group (container) (typed FeaturePython)
  n = 0.012968
FEATURE [App::DocumentObjectGroupPython] Cl_element011  label="Cl_element : 0.000"  # scripted group (container) (typed FeaturePython)
  n = 3.4e-05
FEATURE [App::DocumentObjectGroupPython] Fe_element006  label="Fe_element : 0.000"  # scripted group (container) (typed FeaturePython)
  n = 5.4e-05
FEATURE [App::DocumentObjectGroupPython] G4_FERROUS_SULFATE  # scripted group (container) (typed FeaturePython)
  Dunit = g/cm3
  Dvalue = 1.024
  Group = -> [H_element040,N_element017,O_element040,Na_element007,S_element011,Cl_element011,Fe_element006]
  conduct = 2
  density = 1
  expand = 3
  formula = G4_FERROUS_SULFATE
  name = G4_FERROUS_SULFATE
  specific = 4
FEATURE [App::DocumentObjectGroupPython] C_element043  label="C_element : 0.099"  # scripted group (container) (typed FeaturePython)
  n = 0.099335
FEATURE [App::DocumentObjectGroupPython] F_element007  label="F_element : 0.314"  # scripted group (container) (typed FeaturePython)
  n = 0.314247
FEATURE [App::DocumentObjectGroupPython] Cl_element012  label="Cl_element : 0.586"  # scripted group (container) (typed FeaturePython)
  n = 0.586418
FEATURE [App::DocumentObjectGroupPython] G4_FREON_12  label="G4_FREON-12"  # scripted group (container) (typed FeaturePython)
  Dunit = g/cm3
  Dvalue = 1.12
  Group = -> [C_element043,F_element007,Cl_element012]
  conduct = 2
  density = 1
  expand = 3
  formula = G4_FREON-12
  name = G4_FREON-12
  specific = 4
FEATURE [App::DocumentObjectGroupPython] C_element044  label="C_element : 0.057"  # scripted group (container) (typed FeaturePython)
  n = 0.057245
FEATURE [App::DocumentObjectGroupPython] F_element008  label="F_element : 0.181"  # scripted group (container) (typed FeaturePython)
  n = 0.181096
FEATURE [App::DocumentObjectGroupPython] Br_element001  label="Br_element : 0.762"  # scripted group (container) (typed FeaturePython)
  n = 0.761659
FEATURE [App::DocumentObjectGroupPython] G4_FREON_12B2  label="G4_FREON-12B2"  # scripted group (container) (typed FeaturePython)
  Dunit = g/cm3
  Dvalue = 1.8
  Group = -> [C_element044,F_element008,Br_element001]
  conduct = 2
  density = 1
  expand = 3
  formula = G4_FREON-12B2
  name = G4_FREON-12B2
  specific = 4
FEATURE [App::DocumentObjectGroupPython] C_element045  label="C_element : 0.115"  # scripted group (container) (typed FeaturePython)
  n = 0.114983
FEATURE [App::DocumentObjectGroupPython] F_element009  label="F_element : 0.546"  # scripted group (container) (typed FeaturePython)
  n = 0.545621
FEATURE [App::DocumentObjectGroupPython] Cl_element013  label="Cl_element : 0.339"  # scripted group (container) (typed FeaturePython)
  n = 0.339396
FEATURE [App::DocumentObjectGroupPython] G4_FREON_13  label="G4_FREON-13"  # scripted group (container) (typed FeaturePython)
  Dunit = g/cm3
  Dvalue = 0.95
  Group = -> [C_element045,F_element009,Cl_element013]
  conduct = 2
  density = 1
  expand = 3
  formula = G4_FREON-13
  name = G4_FREON-13
  specific = 4
FEATURE [App::DocumentObjectGroupPython] C_element046  label="C_element : 025"  # scripted group (container) (typed FeaturePython)
  n = 1
  ref = C_element
FEATURE [App::DocumentObjectGroupPython] F_element010  label="F_element : 3"  # scripted group (container) (typed FeaturePython)
  n = 3
  ref = F_element
FEATURE [App::DocumentObjectGroupPython] Br_element002  label="Br_element : 1"  # scripted group (container) (typed FeaturePython)
  n = 1
  ref = Br_element
FEATURE [App::DocumentObjectGroupPython] G4_FREON_13B1  label="G4_FREON-13B1"  # scripted group (container) (typed FeaturePython)
  Dunit = g/cm3
  Dvalue = 1.5
  Group = -> [C_element046,F_element010,Br_element002]
  conduct = 2
  density = 1
  expand = 3
  formula = G4_FREON-13B1
  name = G4_FREON-13B1
  specific = 4
FEATURE [App::DocumentObjectGroupPython] C_element047  label="C_element : 0.061"  # scripted group (container) (typed FeaturePython)
  n = 0.061309
FEATURE [App::DocumentObjectGroupPython] F_element011  label="F_element : 0.291"  # scripted group (container) (typed FeaturePython)
  n = 0.290924
FEATURE [App::DocumentObjectGroupPython] I_element002  label="I_element : 0.648"  # scripted group (container) (typed FeaturePython)
  n = 0.647767
FEATURE [App::DocumentObjectGroupPython] G4_FREON_13I1  label="G4_FREON-13I1"  # scripted group (container) (typed FeaturePython)
  Dunit = g/cm3
  Dvalue = 1.8
  Group = -> [C_element047,F_element011,I_element002]
  conduct = 2
  density = 1
  expand = 3
  formula = G4_FREON-13I1
  name = G4_FREON-13I1
  specific = 4
FEATURE [App::DocumentObjectGroupPython] Gd_element001  label="Gd_element : 2"  # scripted group (container) (typed FeaturePython)
  n = 2
  ref = Gd_element
FEATURE [App::DocumentObjectGroupPython] O_element041  label="O_element : 021"  # scripted group (container) (typed FeaturePython)
  n = 2
  ref = O_element
FEATURE [App::DocumentObjectGroupPython] S_element012  label="S_element : 004"  # scripted group (container) (typed FeaturePython)
  n = 1
  ref = S_element
FEATURE [App::DocumentObjectGroupPython] G4_GADOLINIUM_OXYSULFIDE  # scripted group (container) (typed FeaturePython)
  Dunit = g/cm3
  Dvalue = 7.44
  Group = -> [Gd_element001,O_element041,S_element012]
  conduct = 2
  density = 1
  expand = 3
  formula = G4_GADOLINIUM_OXYSULFIDE
  name = G4_GADOLINIUM_OXYSULFIDE
  specific = 4
FEATURE [App::DocumentObjectGroupPython] Ga_element001  label="Ga_element : 1"  # scripted group (container) (typed FeaturePython)
  n = 1
  ref = Ga_element
FEATURE [App::DocumentObjectGroupPython] As_element001  label="As_element : 1"  # scripted group (container) (typed FeaturePython)
  n = 1
  ref = As_element
FEATURE [App::DocumentObjectGroupPython] G4_GALLIUM_ARSENIDE  # scripted group (container) (typed FeaturePython)
  Dunit = g/cm3
  Dvalue = 5.31
  Group = -> [Ga_element001,As_element001]
  conduct = 2
  density = 1
  expand = 3
  formula = G4_GALLIUM_ARSENIDE
  name = G4_GALLIUM_ARSENIDE
  specific = 4
FEATURE [App::DocumentObjectGroupPython] H_element041  label="H_element : 0.081"  # scripted group (container) (typed FeaturePython)
  n = 0.08118
FEATURE [App::DocumentObjectGroupPython] C_element048  label="C_element : 0.416"  # scripted group (container) (typed FeaturePython)
  n = 0.41606
FEATURE [App::DocumentObjectGroupPython] N_element018  label="N_element : 0.111"  # scripted group (container) (typed FeaturePython)
  n = 0.11124
FEATURE [App::DocumentObjectGroupPython] O_element042  label="O_element : 0.381"  # scripted group (container) (typed FeaturePython)
  n = 0.38064
FEATURE [App::DocumentObjectGroupPython] S_element013  label="S_element : 0.011"  # scripted group (container) (typed FeaturePython)
  n = 0.01088
FEATURE [App::DocumentObjectGroupPython] G4_GEL_PHOTO_EMULSION  # scripted group (container) (typed FeaturePython)
  Dunit = g/cm3
  Dvalue = 1.2914
  Group = -> [H_element041,C_element048,N_element018,O_element042,S_element013]
  conduct = 2
  density = 1
  expand = 3
  formula = G4_GEL_PHOTO_EMULSION
  name = G4_GEL_PHOTO_EMULSION
  specific = 4
FEATURE [App::DocumentObjectGroupPython] B_element004  label="B_element : 0.040"  # scripted group (container) (typed FeaturePython)
  n = 0.0400639
FEATURE [App::DocumentObjectGroupPython] O_element043  label="O_element : 0.540"  # scripted group (container) (typed FeaturePython)
  n = 0.539561
FEATURE [App::DocumentObjectGroupPython] Na_element008  label="Na_element : 0.028"  # scripted group (container) (typed FeaturePython)
  n = 0.0281909
FEATURE [App::DocumentObjectGroupPython] Al_element003  label="Al_element : 0.012"  # scripted group (container) (typed FeaturePython)
  n = 0.011644
FEATURE [App::DocumentObjectGroupPython] Si_element003  label="Si_element : 0.377"  # scripted group (container) (typed FeaturePython)
  n = 0.377219
FEATURE [App::DocumentObjectGroupPython] K_element004  label="K_element : 0.014"  # scripted group (container) (typed FeaturePython)
  n = 0.00332099
FEATURE [App::DocumentObjectGroupPython] G4_Pyrex_Glass  # scripted group (container) (typed FeaturePython)
  Dunit = g/cm3
  Dvalue = 2.23
  Group = -> [B_element004,O_element043,Na_element008,Al_element003,Si_element003,K_element004]
  conduct = 2
  density = 1
  expand = 3
  formula = G4_Pyrex_Glass
  name = G4_Pyrex_Glass
  specific = 4
FEATURE [App::DocumentObjectGroupPython] O_element044  label="O_element : 0.156"  # scripted group (container) (typed FeaturePython)
  n = 0.156453
FEATURE [App::DocumentObjectGroupPython] Si_element004  label="Si_element : 0.081"  # scripted group (container) (typed FeaturePython)
  n = 0.080866
FEATURE [App::DocumentObjectGroupPython] Ti_element001  label="Ti_element : 0.008"  # scripted group (container) (typed FeaturePython)
  n = 0.008092
FEATURE [App::DocumentObjectGroupPython] As_element002  label="As_element : 0.003"  # scripted group (container) (typed FeaturePython)
  n = 0.002651
FEATURE [App::DocumentObjectGroupPython] Pb_element001  label="Pb_element : 0.752"  # scripted group (container) (typed FeaturePython)
  n = 0.751938
FEATURE [App::DocumentObjectGroupPython] G4_GLASS_LEAD  # scripted group (container) (typed FeaturePython)
  Dunit = g/cm3
  Dvalue = 6.22
  Group = -> [O_element044,Si_element004,Ti_element001,As_element002,Pb_element001]
  conduct = 2
  density = 1
  expand = 3
  formula = G4_GLASS_LEAD
  name = G4_GLASS_LEAD
  specific = 4
FEATURE [App::DocumentObjectGroupPython] O_element045  label="O_element : 0.460"  # scripted group (container) (typed FeaturePython)
  n = 0.4598
FEATURE [App::DocumentObjectGroupPython] Na_element009  label="Na_element : 0.096"  # scripted group (container) (typed FeaturePython)
  n = 0.0964411
FEATURE [App::DocumentObjectGroupPython] Si_element005  label="Si_element : 0.378"  # scripted group (container) (typed FeaturePython)
  n = 0.336553
FEATURE [App::DocumentObjectGroupPython] Ca_element011  label="Ca_element : 0.107"  # scripted group (container) (typed FeaturePython)
  n = 0.107205
FEATURE [App::DocumentObjectGroupPython] G4_GLASS_PLATE  # scripted group (container) (typed FeaturePython)
  Dunit = g/cm3
  Dvalue = 2.4
  Group = -> [O_element045,Na_element009,Si_element005,Ca_element011]
  conduct = 2
  density = 1
  expand = 3
  formula = G4_GLASS_PLATE
  name = G4_GLASS_PLATE
  specific = 4
FEATURE [App::DocumentObjectGroupPython] C_element049  label="C_element : 026"  # scripted group (container) (typed FeaturePython)
  n = 5
  ref = C_element
FEATURE [App::DocumentObjectGroupPython] H_element042  label="H_element : 021"  # scripted group (container) (typed FeaturePython)
  n = 10
  ref = H_element
FEATURE [App::DocumentObjectGroupPython] N_element019  label="N_element : 2"  # scripted group (container) (typed FeaturePython)
  n = 2
  ref = N_element
FEATURE [App::DocumentObjectGroupPython] O_element046  label="O_element : 022"  # scripted group (container) (typed FeaturePython)
  n = 3
  ref = O_element
FEATURE [App::DocumentObjectGroupPython] G4_GLUTAMINE  # scripted group (container) (typed FeaturePython)
  Dunit = g/cm3
  Dvalue = 1.46
  Group = -> [C_element049,H_element042,N_element019,O_element046]
  conduct = 2
  density = 1
  expand = 3
  formula = G4_GLUTAMINE
  name = G4_GLUTAMINE
  specific = 4
FEATURE [App::DocumentObjectGroupPython] C_element050  label="C_element : 027"  # scripted group (container) (typed FeaturePython)
  n = 3
  ref = C_element
FEATURE [App::DocumentObjectGroupPython] H_element043  label="H_element : 022"  # scripted group (container) (typed FeaturePython)
  n = 8
  ref = H_element
FEATURE [App::DocumentObjectGroupPython] O_element047  label="O_element : 023"  # scripted group (container) (typed FeaturePython)
  n = 3
  ref = O_element
FEATURE [App::DocumentObjectGroupPython] G4_GLYCEROL  # scripted group (container) (typed FeaturePython)
  Dunit = g/cm3
  Dvalue = 1.2613
  Group = -> [C_element050,H_element043,O_element047]
  conduct = 2
  density = 1
  expand = 3
  formula = G4_GLYCEROL
  name = G4_GLYCEROL
  specific = 4
FEATURE [App::DocumentObjectGroupPython] C_element051  label="C_element : 028"  # scripted group (container) (typed FeaturePython)
  n = 5
  ref = C_element
FEATURE [App::DocumentObjectGroupPython] H_element044  label="H_element : 023"  # scripted group (container) (typed FeaturePython)
  n = 5
  ref = H_element
FEATURE [App::DocumentObjectGroupPython] N_element020  label="N_element : 009"  # scripted group (container) (typed FeaturePython)
  n = 5
  ref = N_element
FEATURE [App::DocumentObjectGroupPython] O_element048  label="O_element : 024"  # scripted group (container) (typed FeaturePython)
  n = 1
  ref = O_element
FEATURE [App::DocumentObjectGroupPython] G4_GUANINE  # scripted group (container) (typed FeaturePython)
  Dunit = g/cm3
  Dvalue = 2.2
  Group = -> [C_element051,H_element044,N_element020,O_element048]
  conduct = 2
  density = 1
  expand = 3
  formula = G4_GUANINE
  name = G4_GUANINE
  specific = 4
FEATURE [App::DocumentObjectGroupPython] Ca_element012  label="Ca_element : 006"  # scripted group (container) (typed FeaturePython)
  n = 1
  ref = Ca_element
FEATURE [App::DocumentObjectGroupPython] S_element014  label="S_element : 005"  # scripted group (container) (typed FeaturePython)
  n = 1
  ref = S_element
FEATURE [App::DocumentObjectGroupPython] O_element049  label="O_element : 6"  # scripted group (container) (typed FeaturePython)
  n = 6
  ref = O_element
FEATURE [App::DocumentObjectGroupPython] H_element045  label="H_element : 024"  # scripted group (container) (typed FeaturePython)
  n = 4
  ref = H_element
FEATURE [App::DocumentObjectGroupPython] G4_GYPSUM  # scripted group (container) (typed FeaturePython)
  Dunit = g/cm3
  Dvalue = 2.32
  Group = -> [Ca_element012,S_element014,O_element049,H_element045]
  conduct = 2
  density = 1
  expand = 3
  formula = G4_GYPSUM
  name = G4_GYPSUM
  specific = 4
FEATURE [App::DocumentObjectGroupPython] C_element052  label="C_element : 7"  # scripted group (container) (typed FeaturePython)
  n = 7
  ref = C_element
FEATURE [App::DocumentObjectGroupPython] H_element046  label="H_element : 16"  # scripted group (container) (typed FeaturePython)
  n = 16
  ref = H_element
FEATURE [App::DocumentObjectGroupPython] G4_N_HEPTANE  label="G4_N-HEPTANE"  # scripted group (container) (typed FeaturePython)
  Dunit = g/cm3
  Dvalue = 0.68376
  Group = -> [C_element052,H_element046]
  conduct = 2
  density = 1
  expand = 3
  formula = G4_N-HEPTANE
  name = G4_N-HEPTANE
  specific = 4
FEATURE [App::DocumentObjectGroupPython] C_element053  label="C_element : 029"  # scripted group (container) (typed FeaturePython)
  n = 6
  ref = C_element
FEATURE [App::DocumentObjectGroupPython] H_element047  label="H_element : 14"  # scripted group (container) (typed FeaturePython)
  n = 14
  ref = H_element
FEATURE [App::DocumentObjectGroupPython] G4_N_HEXANE  label="G4_N-HEXANE"  # scripted group (container) (typed FeaturePython)
  Dunit = g/cm3
  Dvalue = 0.6603
  Group = -> [C_element053,H_element047]
  conduct = 2
  density = 1
  expand = 3
  formula = G4_N-HEXANE
  name = G4_N-HEXANE
  specific = 4
FEATURE [App::DocumentObjectGroupPython] C_element054  label="C_element : 22"  # scripted group (container) (typed FeaturePython)
  n = 22
  ref = C_element
FEATURE [App::DocumentObjectGroupPython] H_element048  label="H_element : 025"  # scripted group (container) (typed FeaturePython)
  n = 10
  ref = H_element
FEATURE [App::DocumentObjectGroupPython] N_element021  label="N_element : 010"  # scripted group (container) (typed FeaturePython)
  n = 2
  ref = N_element
FEATURE [App::DocumentObjectGroupPython] O_element050  label="O_element : 025"  # scripted group (container) (typed FeaturePython)
  n = 5
  ref = O_element
FEATURE [App::DocumentObjectGroupPython] G4_KAPTON  # scripted group (container) (typed FeaturePython)
  Dunit = g/cm3
  Dvalue = 1.42
  Group = -> [C_element054,H_element048,N_element021,O_element050]
  conduct = 2
  density = 1
  expand = 3
  formula = G4_KAPTON
  name = G4_KAPTON
  specific = 4
FEATURE [App::DocumentObjectGroupPython] La_element001  label="La_element : 1"  # scripted group (container) (typed FeaturePython)
  n = 1
  ref = La_element
FEATURE [App::DocumentObjectGroupPython] Br_element003  label="Br_element : 002"  # scripted group (container) (typed FeaturePython)
  n = 1
  ref = Br_element
FEATURE [App::DocumentObjectGroupPython] O_element051  label="O_element : 026"  # scripted group (container) (typed FeaturePython)
  n = 1
  ref = O_element
FEATURE [App::DocumentObjectGroupPython] G4_LANTHANUM_OXYBROMIDE  # scripted group (container) (typed FeaturePython)
  Dunit = g/cm3
  Dvalue = 6.28
  Group = -> [La_element001,Br_element003,O_element051]
  conduct = 2
  density = 1
  expand = 3
  formula = G4_LANTHANUM_OXYBROMIDE
  name = G4_LANTHANUM_OXYBROMIDE
  specific = 4
FEATURE [App::DocumentObjectGroupPython] La_element002  label="La_element : 2"  # scripted group (container) (typed FeaturePython)
  n = 2
  ref = La_element
FEATURE [App::DocumentObjectGroupPython] O_element052  label="O_element : 027"  # scripted group (container) (typed FeaturePython)
  n = 2
  ref = O_element
FEATURE [App::DocumentObjectGroupPython] S_element015  label="S_element : 006"  # scripted group (container) (typed FeaturePython)
  n = 1
  ref = S_element
FEATURE [App::DocumentObjectGroupPython] G4_LANTHANUM_OXYSULFIDE  # scripted group (container) (typed FeaturePython)
  Dunit = g/cm3
  Dvalue = 5.86
  Group = -> [La_element002,O_element052,S_element015]
  conduct = 2
  density = 1
  expand = 3
  formula = G4_LANTHANUM_OXYSULFIDE
  name = G4_LANTHANUM_OXYSULFIDE
  specific = 4
FEATURE [App::DocumentObjectGroupPython] O_element053  label="O_element : 0.072"  # scripted group (container) (typed FeaturePython)
  n = 0.071682
FEATURE [App::DocumentObjectGroupPython] Pb_element002  label="Pb_element : 0.928"  # scripted group (container) (typed FeaturePython)
  n = 0.928318
FEATURE [App::DocumentObjectGroupPython] G4_LEAD_OXIDE  # scripted group (container) (typed FeaturePython)
  Dunit = g/cm3
  Dvalue = 9.53
  Group = -> [O_element053,Pb_element002]
  conduct = 2
  density = 1
  expand = 3
  formula = G4_LEAD_OXIDE
  name = G4_LEAD_OXIDE
  specific = 4
FEATURE [App::DocumentObjectGroupPython] Li_element001  label="Li_element : 1"  # scripted group (container) (typed FeaturePython)
  n = 1
  ref = Li_element
FEATURE [App::DocumentObjectGroupPython] N_element022  label="N_element : 011"  # scripted group (container) (typed FeaturePython)
  n = 1
  ref = N_element
FEATURE [App::DocumentObjectGroupPython] H_element049  label="H_element : 026"  # scripted group (container) (typed FeaturePython)
  n = 2
  ref = H_element
FEATURE [App::DocumentObjectGroupPython] G4_LITHIUM_AMIDE  # scripted group (container) (typed FeaturePython)
  Dunit = g/cm3
  Dvalue = 1.178
  Group = -> [Li_element001,N_element022,H_element049]
  conduct = 2
  density = 1
  expand = 3
  formula = G4_LITHIUM_AMIDE
  name = G4_LITHIUM_AMIDE
  specific = 4
FEATURE [App::DocumentObjectGroupPython] Li_element002  label="Li_element : 2"  # scripted group (container) (typed FeaturePython)
  n = 2
  ref = Li_element
FEATURE [App::DocumentObjectGroupPython] C_element055  label="C_element : 030"  # scripted group (container) (typed FeaturePython)
  n = 1
  ref = C_element
FEATURE [App::DocumentObjectGroupPython] O_element054  label="O_element : 028"  # scripted group (container) (typed FeaturePython)
  n = 3
  ref = O_element
FEATURE [App::DocumentObjectGroupPython] G4_LITHIUM_CARBONATE  # scripted group (container) (typed FeaturePython)
  Dunit = g/cm3
  Dvalue = 2.11
  Group = -> [Li_element002,C_element055,O_element054]
  conduct = 2
  density = 1
  expand = 3
  formula = G4_LITHIUM_CARBONATE
  name = G4_LITHIUM_CARBONATE
  specific = 4
FEATURE [App::DocumentObjectGroupPython] Li_element003  label="Li_element : 003"  # scripted group (container) (typed FeaturePython)
  n = 1
  ref = Li_element
FEATURE [App::DocumentObjectGroupPython] F_element012  label="F_element : 004"  # scripted group (container) (typed FeaturePython)
  n = 1
  ref = F_element
FEATURE [App::DocumentObjectGroupPython] G4_LITHIUM_FLUORIDE  # scripted group (container) (typed FeaturePython)
  Dunit = g/cm3
  Dvalue = 2.635
  Group = -> [Li_element003,F_element012]
  conduct = 2
  density = 1
  expand = 3
  formula = G4_LITHIUM_FLUORIDE
  name = G4_LITHIUM_FLUORIDE
  specific = 4
FEATURE [App::DocumentObjectGroupPython] Li_element004  label="Li_element : 004"  # scripted group (container) (typed FeaturePython)
  n = 1
  ref = Li_element
FEATURE [App::DocumentObjectGroupPython] H_element050  label="H_element : 027"  # scripted group (container) (typed FeaturePython)
  n = 1
  ref = H_element
FEATURE [App::DocumentObjectGroupPython] G4_LITHIUM_HYDRIDE  # scripted group (container) (typed FeaturePython)
  Dunit = g/cm3
  Dvalue = 0.82
  Group = -> [Li_element004,H_element050]
  conduct = 2
  density = 1
  expand = 3
  formula = G4_LITHIUM_HYDRIDE
  name = G4_LITHIUM_HYDRIDE
  specific = 4
FEATURE [App::DocumentObjectGroupPython] Li_element005  label="Li_element : 005"  # scripted group (container) (typed FeaturePython)
  n = 1
  ref = Li_element
FEATURE [App::DocumentObjectGroupPython] I_element003  label="I_element : 002"  # scripted group (container) (typed FeaturePython)
  n = 1
  ref = I_element
FEATURE [App::DocumentObjectGroupPython] G4_LITHIUM_IODIDE  # scripted group (container) (typed FeaturePython)
  Dunit = g/cm3
  Dvalue = 3.494
  Group = -> [Li_element005,I_element003]
  conduct = 2
  density = 1
  expand = 3
  formula = G4_LITHIUM_IODIDE
  name = G4_LITHIUM_IODIDE
  specific = 4
FEATURE [App::DocumentObjectGroupPython] Li_element006  label="Li_element : 006"  # scripted group (container) (typed FeaturePython)
  n = 2
  ref = Li_element
FEATURE [App::DocumentObjectGroupPython] O_element055  label="O_element : 029"  # scripted group (container) (typed FeaturePython)
  n = 1
  ref = O_element
FEATURE [App::DocumentObjectGroupPython] G4_LITHIUM_OXIDE  # scripted group (container) (typed FeaturePython)
  Dunit = g/cm3
  Dvalue = 2.013
  Group = -> [Li_element006,O_element055]
  conduct = 2
  density = 1
  expand = 3
  formula = G4_LITHIUM_OXIDE
  name = G4_LITHIUM_OXIDE
  specific = 4
FEATURE [App::DocumentObjectGroupPython] Li_element007  label="Li_element : 007"  # scripted group (container) (typed FeaturePython)
  n = 2
  ref = Li_element
FEATURE [App::DocumentObjectGroupPython] B_element005  label="B_element : 005"  # scripted group (container) (typed FeaturePython)
  n = 4
  ref = B_element
FEATURE [App::DocumentObjectGroupPython] O_element056  label="O_element : 7"  # scripted group (container) (typed FeaturePython)
  n = 7
  ref = O_element
FEATURE [App::DocumentObjectGroupPython] G4_LITHIUM_TETRABORATE  # scripted group (container) (typed FeaturePython)
  Dunit = g/cm3
  Dvalue = 2.44
  Group = -> [Li_element007,B_element005,O_element056]
  conduct = 2
  density = 1
  expand = 3
  formula = G4_LITHIUM_TETRABORATE
  name = G4_LITHIUM_TETRABORATE
  specific = 4
FEATURE [App::DocumentObjectGroupPython] H_element051  label="H_element : 0.105"  # scripted group (container) (typed FeaturePython)
  n = 0.105
FEATURE [App::DocumentObjectGroupPython] C_element056  label="C_element : 0.083"  # scripted group (container) (typed FeaturePython)
  n = 0.083
FEATURE [App::DocumentObjectGroupPython] N_element023  label="N_element : 0.023"  # scripted group (container) (typed FeaturePython)
  n = 0.023
FEATURE [App::DocumentObjectGroupPython] O_element057  label="O_element : 0.779"  # scripted group (container) (typed FeaturePython)
  n = 0.779
FEATURE [App::DocumentObjectGroupPython] Na_element010  label="Na_element : 0.097"  # scripted group (container) (typed FeaturePython)
  n = 0.002
FEATURE [App::DocumentObjectGroupPython] P_element006  label="P_element : 0.105"  # scripted group (container) (typed FeaturePython)
  n = 0.001
FEATURE [App::DocumentObjectGroupPython] S_element016  label="S_element : 0.017"  # scripted group (container) (typed FeaturePython)
  n = 0.002
FEATURE [App::DocumentObjectGroupPython] Cl_element014  label="Cl_element : 0.587"  # scripted group (container) (typed FeaturePython)
  n = 0.003
FEATURE [App::DocumentObjectGroupPython] K_element005  label="K_element : 0.015"  # scripted group (container) (typed FeaturePython)
  n = 0.002
FEATURE [App::DocumentObjectGroupPython] G4_LUNG_ICRP  # scripted group (container) (typed FeaturePython)
  Dunit = g/cm3
  Dvalue = 1.04
  Group = -> [H_element051,C_element056,N_element023,O_element057,Na_element010,P_element006,S_element016,Cl_element014,K_element005]
  conduct = 2
  density = 1
  expand = 3
  formula = G4_LUNG_ICRP
  name = G4_LUNG_ICRP
  specific = 4
FEATURE [App::DocumentObjectGroupPython] H_element052  label="H_element : 0.116"  # scripted group (container) (typed FeaturePython)
  n = 0.114318
FEATURE [App::DocumentObjectGroupPython] C_element057  label="C_element : 0.656"  # scripted group (container) (typed FeaturePython)
  n = 0.655824
FEATURE [App::DocumentObjectGroupPython] O_element058  label="O_element : 0.092"  # scripted group (container) (typed FeaturePython)
  n = 0.0921831
FEATURE [App::DocumentObjectGroupPython] Mg_element004  label="Mg_element : 0.135"  # scripted group (container) (typed FeaturePython)
  n = 0.134792
FEATURE [App::DocumentObjectGroupPython] Ca_element013  label="Ca_element : 0.003"  # scripted group (container) (typed FeaturePython)
  n = 0.002883
FEATURE [App::DocumentObjectGroupPython] G4_M3_WAX  # scripted group (container) (typed FeaturePython)
  Dunit = g/cm3
  Dvalue = 1.05
  Group = -> [H_element052,C_element057,O_element058,Mg_element004,Ca_element013]
  conduct = 2
  density = 1
  expand = 3
  formula = G4_M3_WAX
  name = G4_M3_WAX
  specific = 4
FEATURE [App::DocumentObjectGroupPython] Mg_element005  label="Mg_element : 1"  # scripted group (container) (typed FeaturePython)
  n = 1
  ref = Mg_element
FEATURE [App::DocumentObjectGroupPython] C_element058  label="C_element : 031"  # scripted group (container) (typed FeaturePython)
  n = 1
  ref = C_element
FEATURE [App::DocumentObjectGroupPython] O_element059  label="O_element : 030"  # scripted group (container) (typed FeaturePython)
  n = 3
  ref = O_element
FEATURE [App::DocumentObjectGroupPython] G4_MAGNESIUM_CARBONATE  # scripted group (container) (typed FeaturePython)
  Dunit = g/cm3
  Dvalue = 2.958
  Group = -> [Mg_element005,C_element058,O_element059]
  conduct = 2
  density = 1
  expand = 3
  formula = G4_MAGNESIUM_CARBONATE
  name = G4_MAGNESIUM_CARBONATE
  specific = 4
FEATURE [App::DocumentObjectGroupPython] Mg_element006  label="Mg_element : 002"  # scripted group (container) (typed FeaturePython)
  n = 1
  ref = Mg_element
FEATURE [App::DocumentObjectGroupPython] F_element013  label="F_element : 005"  # scripted group (container) (typed FeaturePython)
  n = 2
  ref = F_element
FEATURE [App::DocumentObjectGroupPython] G4_MAGNESIUM_FLUORIDE  # scripted group (container) (typed FeaturePython)
  Dunit = g/cm3
  Dvalue = 3
  Group = -> [Mg_element006,F_element013]
  conduct = 2
  density = 1
  expand = 3
  formula = G4_MAGNESIUM_FLUORIDE
  name = G4_MAGNESIUM_FLUORIDE
  specific = 4
FEATURE [App::DocumentObjectGroupPython] Mg_element007  label="Mg_element : 003"  # scripted group (container) (typed FeaturePython)
  n = 1
  ref = Mg_element
FEATURE [App::DocumentObjectGroupPython] O_element060  label="O_element : 031"  # scripted group (container) (typed FeaturePython)
  n = 1
  ref = O_element
FEATURE [App::DocumentObjectGroupPython] G4_MAGNESIUM_OXIDE  # scripted group (container) (typed FeaturePython)
  Dunit = g/cm3
  Dvalue = 3.58
  Group = -> [Mg_element007,O_element060]
  conduct = 2
  density = 1
  expand = 3
  formula = G4_MAGNESIUM_OXIDE
  name = G4_MAGNESIUM_OXIDE
  specific = 4
FEATURE [App::DocumentObjectGroupPython] Mg_element008  label="Mg_element : 004"  # scripted group (container) (typed FeaturePython)
  n = 1
  ref = Mg_element
FEATURE [App::DocumentObjectGroupPython] B_element006  label="B_element : 006"  # scripted group (container) (typed FeaturePython)
  n = 4
  ref = B_element
FEATURE [App::DocumentObjectGroupPython] O_element061  label="O_element : 032"  # scripted group (container) (typed FeaturePython)
  n = 7
  ref = O_element
FEATURE [App::DocumentObjectGroupPython] G4_MAGNESIUM_TETRABORATE  # scripted group (container) (typed FeaturePython)
  Dunit = g/cm3
  Dvalue = 2.53
  Group = -> [Mg_element008,B_element006,O_element061]
  conduct = 2
  density = 1
  expand = 3
  formula = G4_MAGNESIUM_TETRABORATE
  name = G4_MAGNESIUM_TETRABORATE
  specific = 4
FEATURE [App::DocumentObjectGroupPython] Hg_element001  label="Hg_element : 1"  # scripted group (container) (typed FeaturePython)
  n = 1
  ref = Hg_element
FEATURE [App::DocumentObjectGroupPython] I_element004  label="I_element : 2"  # scripted group (container) (typed FeaturePython)
  n = 2
  ref = I_element
FEATURE [App::DocumentObjectGroupPython] G4_MERCURIC_IODIDE  # scripted group (container) (typed FeaturePython)
  Dunit = g/cm3
  Dvalue = 6.36
  Group = -> [Hg_element001,I_element004]
  conduct = 2
  density = 1
  expand = 3
  formula = G4_MERCURIC_IODIDE
  name = G4_MERCURIC_IODIDE
  specific = 4
FEATURE [App::DocumentObjectGroupPython] C_element059  label="C_element : 032"  # scripted group (container) (typed FeaturePython)
  n = 1
  ref = C_element
FEATURE [App::DocumentObjectGroupPython] H_element053  label="H_element : 028"  # scripted group (container) (typed FeaturePython)
  n = 4
  ref = H_element
FEATURE [App::DocumentObjectGroupPython] G4_METHANE  # scripted group (container) (typed FeaturePython)
  Dunit = g/cm3
  Dvalue = 0.000667151
  Group = -> [C_element059,H_element053]
  conduct = 2
  density = 1
  expand = 3
  formula = G4_METHANE
  name = G4_METHANE
  specific = 4
FEATURE [App::DocumentObjectGroupPython] C_element060  label="C_element : 033"  # scripted group (container) (typed FeaturePython)
  n = 1
  ref = C_element
FEATURE [App::DocumentObjectGroupPython] H_element054  label="H_element : 029"  # scripted group (container) (typed FeaturePython)
  n = 4
  ref = H_element
FEATURE [App::DocumentObjectGroupPython] O_element062  label="O_element : 033"  # scripted group (container) (typed FeaturePython)
  n = 1
  ref = O_element
FEATURE [App::DocumentObjectGroupPython] G4_METHANOL  # scripted group (container) (typed FeaturePython)
  Dunit = g/cm3
  Dvalue = 0.7914
  Group = -> [C_element060,H_element054,O_element062]
  conduct = 2
  density = 1
  expand = 3
  formula = G4_METHANOL
  name = G4_METHANOL
  specific = 4
FEATURE [App::DocumentObjectGroupPython] H_element055  label="H_element : 0.134"  # scripted group (container) (typed FeaturePython)
  n = 0.13404
FEATURE [App::DocumentObjectGroupPython] C_element061  label="C_element : 0.778"  # scripted group (container) (typed FeaturePython)
  n = 0.77796
FEATURE [App::DocumentObjectGroupPython] O_element063  label="O_element : 0.035"  # scripted group (container) (typed FeaturePython)
  n = 0.03502
FEATURE [App::DocumentObjectGroupPython] Mg_element009  label="Mg_element : 0.039"  # scripted group (container) (typed FeaturePython)
  n = 0.038594
FEATURE [App::DocumentObjectGroupPython] Ti_element002  label="Ti_element : 0.014"  # scripted group (container) (typed FeaturePython)
  n = 0.014386
FEATURE [App::DocumentObjectGroupPython] G4_MIX_D_WAX  # scripted group (container) (typed FeaturePython)
  Dunit = g/cm3
  Dvalue = 0.99
  Group = -> [H_element055,C_element061,O_element063,Mg_element009,Ti_element002]
  conduct = 2
  density = 1
  expand = 3
  formula = G4_MIX_D_WAX
  name = G4_MIX_D_WAX
  specific = 4
FEATURE [App::DocumentObjectGroupPython] H_element056  label="H_element : 0.135"  # scripted group (container) (typed FeaturePython)
  n = 0.081192
FEATURE [App::DocumentObjectGroupPython] C_element062  label="C_element : 0.583"  # scripted group (container) (typed FeaturePython)
  n = 0.583442
FEATURE [App::DocumentObjectGroupPython] N_element024  label="N_element : 0.018"  # scripted group (container) (typed FeaturePython)
  n = 0.017798
FEATURE [App::DocumentObjectGroupPython] O_element064  label="O_element : 0.186"  # scripted group (container) (typed FeaturePython)
  n = 0.186381
FEATURE [App::DocumentObjectGroupPython] Mg_element010  label="Mg_element : 0.130"  # scripted group (container) (typed FeaturePython)
  n = 0.130287
FEATURE [App::DocumentObjectGroupPython] Cl_element015  label="Cl_element : 0.588"  # scripted group (container) (typed FeaturePython)
  n = 0.0009
FEATURE [App::DocumentObjectGroupPython] G4_MS20_TISSUE  # scripted group (container) (typed FeaturePython)
  Dunit = g/cm3
  Dvalue = 1
  Group = -> [H_element056,C_element062,N_element024,O_element064,Mg_element010,Cl_element015]
  conduct = 2
  density = 1
  expand = 3
  formula = G4_MS20_TISSUE
  name = G4_MS20_TISSUE
  specific = 4
FEATURE [App::DocumentObjectGroupPython] H_element057  label="H_element : 0.136"  # scripted group (container) (typed FeaturePython)
  n = 0.102
FEATURE [App::DocumentObjectGroupPython] C_element063  label="C_element : 0.143"  # scripted group (container) (typed FeaturePython)
  n = 0.143
FEATURE [App::DocumentObjectGroupPython] N_element025  label="N_element : 0.034"  # scripted group (container) (typed FeaturePython)
  n = 0.034
FEATURE [App::DocumentObjectGroupPython] O_element065  label="O_element : 0.710"  # scripted group (container) (typed FeaturePython)
  n = 0.71
FEATURE [App::DocumentObjectGroupPython] Na_element011  label="Na_element : 0.098"  # scripted group (container) (typed FeaturePython)
  n = 0.001
FEATURE [App::DocumentObjectGroupPython] P_element007  label="P_element : 0.002"  # scripted group (container) (typed FeaturePython)
  n = 0.002
FEATURE [App::DocumentObjectGroupPython] S_element017  label="S_element : 0.018"  # scripted group (container) (typed FeaturePython)
  n = 0.003
FEATURE [App::DocumentObjectGroupPython] Cl_element016  label="Cl_element : 0.589"  # scripted group (container) (typed FeaturePython)
  n = 0.001
FEATURE [App::DocumentObjectGroupPython] K_element006  label="K_element : 0.004"  # scripted group (container) (typed FeaturePython)
  n = 0.004
FEATURE [App::DocumentObjectGroupPython] G4_MUSCLE_SKELETAL_ICRP  # scripted group (container) (typed FeaturePython)
  Dunit = g/cm3
  Dvalue = 1.05
  Group = -> [H_element057,C_element063,N_element025,O_element065,Na_element011,P_element007,S_element017,Cl_element016,K_element006]
  conduct = 2
  density = 1
  expand = 3
  formula = G4_MUSCLE_SKELETAL_ICRP
  name = G4_MUSCLE_SKELETAL_ICRP
  specific = 4
FEATURE [App::DocumentObjectGroupPython] H_element058  label="H_element : 0.137"  # scripted group (container) (typed FeaturePython)
  n = 0.102102
FEATURE [App::DocumentObjectGroupPython] C_element064  label="C_element : 0.123"  # scripted group (container) (typed FeaturePython)
  n = 0.123123
FEATURE [App::DocumentObjectGroupPython] N_element026  label="N_element : 0.756"  # scripted group (container) (typed FeaturePython)
  n = 0.035035
FEATURE [App::DocumentObjectGroupPython] O_element066  label="O_element : 0.730"  # scripted group (container) (typed FeaturePython)
  n = 0.72973
FEATURE [App::DocumentObjectGroupPython] Na_element012  label="Na_element : 0.099"  # scripted group (container) (typed FeaturePython)
  n = 0.001001
FEATURE [App::DocumentObjectGroupPython] P_element008  label="P_element : 0.106"  # scripted group (container) (typed FeaturePython)
  n = 0.002002
FEATURE [App::DocumentObjectGroupPython] S_element018  label="S_element : 0.019"  # scripted group (container) (typed FeaturePython)
  n = 0.004004
FEATURE [App::DocumentObjectGroupPython] K_element007  label="K_element : 0.016"  # scripted group (container) (typed FeaturePython)
  n = 0.003003
FEATURE [App::DocumentObjectGroupPython] G4_MUSCLE_STRIATED_ICRU  # scripted group (container) (typed FeaturePython)
  Dunit = g/cm3
  Dvalue = 1.04
  Group = -> [H_element058,C_element064,N_element026,O_element066,Na_element012,P_element008,S_element018,K_element007]
  conduct = 2
  density = 1
  expand = 3
  formula = G4_MUSCLE_STRIATED_ICRU
  name = G4_MUSCLE_STRIATED_ICRU
  specific = 4
FEATURE [App::DocumentObjectGroupPython] H_element059  label="H_element : 0.098"  # scripted group (container) (typed FeaturePython)
  n = 0.0982341
FEATURE [App::DocumentObjectGroupPython] C_element065  label="C_element : 0.156"  # scripted group (container) (typed FeaturePython)
  n = 0.156214
FEATURE [App::DocumentObjectGroupPython] N_element027  label="N_element : 0.757"  # scripted group (container) (typed FeaturePython)
  n = 0.035451
FEATURE [App::DocumentObjectGroupPython] O_element067  label="O_element : 0.880"  # scripted group (container) (typed FeaturePython)
  n = 0.710101
FEATURE [App::DocumentObjectGroupPython] G4_MUSCLE_WITH_SUCROSE  # scripted group (container) (typed FeaturePython)
  Dunit = g/cm3
  Dvalue = 1.11
  Group = -> [H_element059,C_element065,N_element027,O_element067]
  conduct = 2
  density = 1
  expand = 3
  formula = G4_MUSCLE_WITH_SUCROSE
  name = G4_MUSCLE_WITH_SUCROSE
  specific = 4
FEATURE [App::DocumentObjectGroupPython] H_element060  label="H_element : 0.138"  # scripted group (container) (typed FeaturePython)
  n = 0.101969
FEATURE [App::DocumentObjectGroupPython] C_element066  label="C_element : 0.120"  # scripted group (container) (typed FeaturePython)
  n = 0.120058
FEATURE [App::DocumentObjectGroupPython] N_element028  label="N_element : 0.758"  # scripted group (container) (typed FeaturePython)
  n = 0.035451
FEATURE [App::DocumentObjectGroupPython] O_element068  label="O_element : 0.743"  # scripted group (container) (typed FeaturePython)
  n = 0.742522
FEATURE [App::DocumentObjectGroupPython] G4_MUSCLE_WITHOUT_SUCROSE  # scripted group (container) (typed FeaturePython)
  Dunit = g/cm3
  Dvalue = 1.07
  Group = -> [H_element060,C_element066,N_element028,O_element068]
  conduct = 2
  density = 1
  expand = 3
  formula = G4_MUSCLE_WITHOUT_SUCROSE
  name = G4_MUSCLE_WITHOUT_SUCROSE
  specific = 4
FEATURE [App::DocumentObjectGroupPython] C_element067  label="C_element : 10"  # scripted group (container) (typed FeaturePython)
  n = 10
  ref = C_element
FEATURE [App::DocumentObjectGroupPython] H_element061  label="H_element : 030"  # scripted group (container) (typed FeaturePython)
  n = 8
  ref = H_element
FEATURE [App::DocumentObjectGroupPython] G4_NAPHTHALENE  # scripted group (container) (typed FeaturePython)
  Dunit = g/cm3
  Dvalue = 1.145
  Group = -> [C_element067,H_element061]
  conduct = 2
  density = 1
  expand = 3
  formula = G4_NAPHTHALENE
  name = G4_NAPHTHALENE
  specific = 4
FEATURE [App::DocumentObjectGroupPython] C_element068  label="C_element : 034"  # scripted group (container) (typed FeaturePython)
  n = 6
  ref = C_element
FEATURE [App::DocumentObjectGroupPython] H_element062  label="H_element : 031"  # scripted group (container) (typed FeaturePython)
  n = 5
  ref = H_element
FEATURE [App::DocumentObjectGroupPython] N_element029  label="N_element : 012"  # scripted group (container) (typed FeaturePython)
  n = 1
  ref = N_element
FEATURE [App::DocumentObjectGroupPython] O_element069  label="O_element : 034"  # scripted group (container) (typed FeaturePython)
  n = 2
  ref = O_element
FEATURE [App::DocumentObjectGroupPython] G4_NITROBENZENE  # scripted group (container) (typed FeaturePython)
  Dunit = g/cm3
  Dvalue = 1.19867
  Group = -> [C_element068,H_element062,N_element029,O_element069]
  conduct = 2
  density = 1
  expand = 3
  formula = G4_NITROBENZENE
  name = G4_NITROBENZENE
  specific = 4
FEATURE [App::DocumentObjectGroupPython] N_element030  label="N_element : 013"  # scripted group (container) (typed FeaturePython)
  n = 2
  ref = N_element
FEATURE [App::DocumentObjectGroupPython] O_element070  label="O_element : 035"  # scripted group (container) (typed FeaturePython)
  n = 1
  ref = O_element
FEATURE [App::DocumentObjectGroupPython] G4_NITROUS_OXIDE  # scripted group (container) (typed FeaturePython)
  Dunit = g/cm3
  Dvalue = 0.00183094
  Group = -> [N_element030,O_element070]
  conduct = 2
  density = 1
  expand = 3
  formula = G4_NITROUS_OXIDE
  name = G4_NITROUS_OXIDE
  specific = 4
FEATURE [App::DocumentObjectGroupPython] H_element063  label="H_element : 0.104"  # scripted group (container) (typed FeaturePython)
  n = 0.103509
FEATURE [App::DocumentObjectGroupPython] C_element069  label="C_element : 0.648"  # scripted group (container) (typed FeaturePython)
  n = 0.648416
FEATURE [App::DocumentObjectGroupPython] N_element031  label="N_element : 0.100"  # scripted group (container) (typed FeaturePython)
  n = 0.0995361
FEATURE [App::DocumentObjectGroupPython] O_element071  label="O_element : 0.149"  # scripted group (container) (typed FeaturePython)
  n = 0.148539
FEATURE [App::DocumentObjectGroupPython] G4_NYLON_8062  label="G4_NYLON-8062"  # scripted group (container) (typed FeaturePython)
  Dunit = g/cm3
  Dvalue = 1.08
  Group = -> [H_element063,C_element069,N_element031,O_element071]
  conduct = 2
  density = 1
  expand = 3
  formula = G4_NYLON-8062
  name = G4_NYLON-8062
  specific = 4
FEATURE [App::DocumentObjectGroupPython] C_element070  label="C_element : 035"  # scripted group (container) (typed FeaturePython)
  n = 6
  ref = C_element
FEATURE [App::DocumentObjectGroupPython] H_element064  label="H_element : 11"  # scripted group (container) (typed FeaturePython)
  n = 11
  ref = H_element
FEATURE [App::DocumentObjectGroupPython] N_element032  label="N_element : 014"  # scripted group (container) (typed FeaturePython)
  n = 1
  ref = N_element
FEATURE [App::DocumentObjectGroupPython] O_element072  label="O_element : 036"  # scripted group (container) (typed FeaturePython)
  n = 1
  ref = O_element
FEATURE [App::DocumentObjectGroupPython] G4_NYLON_6_6  label="G4_NYLON-6-6"  # scripted group (container) (typed FeaturePython)
  Dunit = g/cm3
  Dvalue = 1.14
  Group = -> [C_element070,H_element064,N_element032,O_element072]
  conduct = 2
  density = 1
  expand = 3
  formula = G4_NYLON-6-6
  name = G4_NYLON-6-6
  specific = 4
FEATURE [App::DocumentObjectGroupPython] H_element065  label="H_element : 0.139"  # scripted group (container) (typed FeaturePython)
  n = 0.107062
FEATURE [App::DocumentObjectGroupPython] C_element071  label="C_element : 0.680"  # scripted group (container) (typed FeaturePython)
  n = 0.680449
FEATURE [App::DocumentObjectGroupPython] N_element033  label="N_element : 0.099"  # scripted group (container) (typed FeaturePython)
  n = 0.099189
FEATURE [App::DocumentObjectGroupPython] O_element073  label="O_element : 0.113"  # scripted group (container) (typed FeaturePython)
  n = 0.1133
FEATURE [App::DocumentObjectGroupPython] G4_NYLON_6_10  label="G4_NYLON-6-10"  # scripted group (container) (typed FeaturePython)
  Dunit = g/cm3
  Dvalue = 1.14
  Group = -> [H_element065,C_element071,N_element033,O_element073]
  conduct = 2
  density = 1
  expand = 3
  formula = G4_NYLON-6-10
  name = G4_NYLON-6-10
  specific = 4
FEATURE [App::DocumentObjectGroupPython] H_element066  label="H_element : 0.140"  # scripted group (container) (typed FeaturePython)
  n = 0.115476
FEATURE [App::DocumentObjectGroupPython] C_element072  label="C_element : 0.721"  # scripted group (container) (typed FeaturePython)
  n = 0.720818
FEATURE [App::DocumentObjectGroupPython] N_element034  label="N_element : 0.076"  # scripted group (container) (typed FeaturePython)
  n = 0.0764169
FEATURE [App::DocumentObjectGroupPython] O_element074  label="O_element : 0.087"  # scripted group (container) (typed FeaturePython)
  n = 0.0872889
FEATURE [App::DocumentObjectGroupPython] G4_NYLON_11_RILSAN  label="G4_NYLON-11_RILSAN"  # scripted group (container) (typed FeaturePython)
  Dunit = g/cm3
  Dvalue = 1.425
  Group = -> [H_element066,C_element072,N_element034,O_element074]
  conduct = 2
  density = 1
  expand = 3
  formula = G4_NYLON-11_RILSAN
  name = G4_NYLON-11_RILSAN
  specific = 4
FEATURE [App::DocumentObjectGroupPython] C_element073  label="C_element : 8"  # scripted group (container) (typed FeaturePython)
  n = 8
  ref = C_element
FEATURE [App::DocumentObjectGroupPython] H_element067  label="H_element : 18"  # scripted group (container) (typed FeaturePython)
  n = 18
  ref = H_element
FEATURE [App::DocumentObjectGroupPython] G4_OCTANE  # scripted group (container) (typed FeaturePython)
  Dunit = g/cm3
  Dvalue = 0.7026
  Group = -> [C_element073,H_element067]
  conduct = 2
  density = 1
  expand = 3
  formula = G4_OCTANE
  name = G4_OCTANE
  specific = 4
FEATURE [App::DocumentObjectGroupPython] C_element074  label="C_element : 25"  # scripted group (container) (typed FeaturePython)
  n = 25
  ref = C_element
FEATURE [App::DocumentObjectGroupPython] H_element068  label="H_element : 52"  # scripted group (container) (typed FeaturePython)
  n = 52
  ref = H_element
FEATURE [App::DocumentObjectGroupPython] G4_PARAFFIN  # scripted group (container) (typed FeaturePython)
  Dunit = g/cm3
  Dvalue = 0.93
  Group = -> [C_element074,H_element068]
  conduct = 2
  density = 1
  expand = 3
  formula = G4_PARAFFIN
  name = G4_PARAFFIN
  specific = 4
FEATURE [App::DocumentObjectGroupPython] C_element075  label="C_element : 036"  # scripted group (container) (typed FeaturePython)
  n = 5
  ref = C_element
FEATURE [App::DocumentObjectGroupPython] H_element069  label="H_element : 032"  # scripted group (container) (typed FeaturePython)
  n = 12
  ref = H_element
FEATURE [App::DocumentObjectGroupPython] G4_N_PENTANE  label="G4_N-PENTANE"  # scripted group (container) (typed FeaturePython)
  Dunit = g/cm3
  Dvalue = 0.6262
  Group = -> [C_element075,H_element069]
  conduct = 2
  density = 1
  expand = 3
  formula = G4_N-PENTANE
  name = G4_N-PENTANE
  specific = 4
FEATURE [App::DocumentObjectGroupPython] H_element070  label="H_element : 0.014"  # scripted group (container) (typed FeaturePython)
  n = 0.0141
FEATURE [App::DocumentObjectGroupPython] C_element076  label="C_element : 0.072"  # scripted group (container) (typed FeaturePython)
  n = 0.072261
FEATURE [App::DocumentObjectGroupPython] N_element035  label="N_element : 0.019"  # scripted group (container) (typed FeaturePython)
  n = 0.01932
FEATURE [App::DocumentObjectGroupPython] O_element075  label="O_element : 0.066"  # scripted group (container) (typed FeaturePython)
  n = 0.066101
FEATURE [App::DocumentObjectGroupPython] S_element019  label="S_element : 0.020"  # scripted group (container) (typed FeaturePython)
  n = 0.00189
FEATURE [App::DocumentObjectGroupPython] Br_element004  label="Br_element : 0.349"  # scripted group (container) (typed FeaturePython)
  n = 0.349103
FEATURE [App::DocumentObjectGroupPython] Ag_element001  label="Ag_element : 0.474"  # scripted group (container) (typed FeaturePython)
  n = 0.474105
FEATURE [App::DocumentObjectGroupPython] I_element005  label="I_element : 0.003"  # scripted group (container) (typed FeaturePython)
  n = 0.00312
FEATURE [App::DocumentObjectGroupPython] G4_PHOTO_EMULSION  # scripted group (container) (typed FeaturePython)
  Dunit = g/cm3
  Dvalue = 3.815
  Group = -> [H_element070,C_element076,N_element035,O_element075,S_element019,Br_element004,Ag_element001,I_element005]
  conduct = 2
  density = 1
  expand = 3
  formula = G4_PHOTO_EMULSION
  name = G4_PHOTO_EMULSION
  specific = 4
FEATURE [App::DocumentObjectGroupPython] C_element077  label="C_element : 9"  # scripted group (container) (typed FeaturePython)
  n = 9
  ref = C_element
FEATURE [App::DocumentObjectGroupPython] H_element071  label="H_element : 033"  # scripted group (container) (typed FeaturePython)
  n = 10
  ref = H_element
FEATURE [App::DocumentObjectGroupPython] G4_PLASTIC_SC_VINYLTOLUENE  # scripted group (container) (typed FeaturePython)
  Dunit = g/cm3
  Dvalue = 1.032
  Group = -> [C_element077,H_element071]
  conduct = 2
  density = 1
  expand = 3
  formula = G4_PLASTIC_SC_VINYLTOLUENE
  name = G4_PLASTIC_SC_VINYLTOLUENE
  specific = 4
FEATURE [App::DocumentObjectGroupPython] Pu_element001  label="Pu_element : 1"  # scripted group (container) (typed FeaturePython)
  n = 1
  ref = Pu_element
FEATURE [App::DocumentObjectGroupPython] O_element076  label="O_element : 037"  # scripted group (container) (typed FeaturePython)
  n = 2
  ref = O_element
FEATURE [App::DocumentObjectGroupPython] G4_PLUTONIUM_DIOXIDE  # scripted group (container) (typed FeaturePython)
  Dunit = g/cm3
  Dvalue = 11.46
  Group = -> [Pu_element001,O_element076]
  conduct = 2
  density = 1
  expand = 3
  formula = G4_PLUTONIUM_DIOXIDE
  name = G4_PLUTONIUM_DIOXIDE
  specific = 4
FEATURE [App::DocumentObjectGroupPython] C_element078  label="C_element : 037"  # scripted group (container) (typed FeaturePython)
  n = 3
  ref = C_element
FEATURE [App::DocumentObjectGroupPython] H_element072  label="H_element : 034"  # scripted group (container) (typed FeaturePython)
  n = 3
  ref = H_element
FEATURE [App::DocumentObjectGroupPython] N_element036  label="N_element : 015"  # scripted group (container) (typed FeaturePython)
  n = 1
  ref = N_element
FEATURE [App::DocumentObjectGroupPython] G4_POLYACRYLONITRILE  # scripted group (container) (typed FeaturePython)
  Dunit = g/cm3
  Dvalue = 1.17
  Group = -> [C_element078,H_element072,N_element036]
  conduct = 2
  density = 1
  expand = 3
  formula = G4_POLYACRYLONITRILE
  name = G4_POLYACRYLONITRILE
  specific = 4
FEATURE [App::DocumentObjectGroupPython] C_element079  label="C_element : 16"  # scripted group (container) (typed FeaturePython)
  n = 16
  ref = C_element
FEATURE [App::DocumentObjectGroupPython] H_element073  label="H_element : 035"  # scripted group (container) (typed FeaturePython)
  n = 14
  ref = H_element
FEATURE [App::DocumentObjectGroupPython] O_element077  label="O_element : 038"  # scripted group (container) (typed FeaturePython)
  n = 3
  ref = O_element
FEATURE [App::DocumentObjectGroupPython] G4_POLYCARBONATE  # scripted group (container) (typed FeaturePython)
  Dunit = g/cm3
  Dvalue = 1.2
  Group = -> [C_element079,H_element073,O_element077]
  conduct = 2
  density = 1
  expand = 3
  formula = G4_POLYCARBONATE
  name = G4_POLYCARBONATE
  specific = 4
FEATURE [App::DocumentObjectGroupPython] C_element080  label="C_element : 038"  # scripted group (container) (typed FeaturePython)
  n = 8
  ref = C_element
FEATURE [App::DocumentObjectGroupPython] H_element074  label="H_element : 036"  # scripted group (container) (typed FeaturePython)
  n = 7
  ref = H_element
FEATURE [App::DocumentObjectGroupPython] Cl_element017  label="Cl_element : 007"  # scripted group (container) (typed FeaturePython)
  n = 1
  ref = Cl_element
FEATURE [App::DocumentObjectGroupPython] G4_POLYCHLOROSTYRENE  # scripted group (container) (typed FeaturePython)
  Dunit = g/cm3
  Dvalue = 1.3
  Group = -> [C_element080,H_element074,Cl_element017]
  conduct = 2
  density = 1
  expand = 3
  formula = G4_POLYCHLOROSTYRENE
  name = G4_POLYCHLOROSTYRENE
  specific = 4
FEATURE [App::DocumentObjectGroupPython] C_element081  label="C_element : 039"  # scripted group (container) (typed FeaturePython)
  n = 1
  ref = C_element
FEATURE [App::DocumentObjectGroupPython] H_element075  label="H_element : 037"  # scripted group (container) (typed FeaturePython)
  n = 2
  ref = H_element
FEATURE [App::DocumentObjectGroupPython] G4_POLYETHYLENE  # scripted group (container) (typed FeaturePython)
  Dunit = g/cm3
  Dvalue = 0.94
  Group = -> [C_element081,H_element075]
  conduct = 2
  density = 1
  expand = 3
  formula = G4_POLYETHYLENE
  name = G4_POLYETHYLENE
  specific = 4
FEATURE [App::DocumentObjectGroupPython] C_element082  label="C_element : 040"  # scripted group (container) (typed FeaturePython)
  n = 10
  ref = C_element
FEATURE [App::DocumentObjectGroupPython] H_element076  label="H_element : 038"  # scripted group (container) (typed FeaturePython)
  n = 8
  ref = H_element
FEATURE [App::DocumentObjectGroupPython] O_element078  label="O_element : 039"  # scripted group (container) (typed FeaturePython)
  n = 4
  ref = O_element
FEATURE [App::DocumentObjectGroupPython] G4_MYLAR  # scripted group (container) (typed FeaturePython)
  Dunit = g/cm3
  Dvalue = 1.4
  Group = -> [C_element082,H_element076,O_element078]
  conduct = 2
  density = 1
  expand = 3
  formula = G4_MYLAR
  name = G4_MYLAR
  specific = 4
FEATURE [App::DocumentObjectGroupPython] C_element083  label="C_element : 041"  # scripted group (container) (typed FeaturePython)
  n = 5
  ref = C_element
FEATURE [App::DocumentObjectGroupPython] H_element077  label="H_element : 039"  # scripted group (container) (typed FeaturePython)
  n = 8
  ref = H_element
FEATURE [App::DocumentObjectGroupPython] O_element079  label="O_element : 040"  # scripted group (container) (typed FeaturePython)
  n = 2
  ref = O_element
FEATURE [App::DocumentObjectGroupPython] G4_PLEXIGLASS  # scripted group (container) (typed FeaturePython)
  Dunit = g/cm3
  Dvalue = 1.19
  Group = -> [C_element083,H_element077,O_element079]
  conduct = 2
  density = 1
  expand = 3
  formula = G4_PLEXIGLASS
  name = G4_PLEXIGLASS
  specific = 4
FEATURE [App::DocumentObjectGroupPython] C_element084  label="C_element : 042"  # scripted group (container) (typed FeaturePython)
  n = 1
  ref = C_element
FEATURE [App::DocumentObjectGroupPython] H_element078  label="H_element : 040"  # scripted group (container) (typed FeaturePython)
  n = 2
  ref = H_element
FEATURE [App::DocumentObjectGroupPython] O_element080  label="O_element : 041"  # scripted group (container) (typed FeaturePython)
  n = 1
  ref = O_element
FEATURE [App::DocumentObjectGroupPython] G4_POLYOXYMETHYLENE  # scripted group (container) (typed FeaturePython)
  Dunit = g/cm3
  Dvalue = 1.425
  Group = -> [C_element084,H_element078,O_element080]
  conduct = 2
  density = 1
  expand = 3
  formula = G4_POLYOXYMETHYLENE
  name = G4_POLYOXYMETHYLENE
  specific = 4
FEATURE [App::DocumentObjectGroupPython] C_element085  label="C_element : 043"  # scripted group (container) (typed FeaturePython)
  n = 2
  ref = C_element
FEATURE [App::DocumentObjectGroupPython] H_element079  label="H_element : 041"  # scripted group (container) (typed FeaturePython)
  n = 4
  ref = H_element
FEATURE [App::DocumentObjectGroupPython] G4_POLYPROPYLENE  # scripted group (container) (typed FeaturePython)
  Dunit = g/cm3
  Dvalue = 0.9
  Group = -> [C_element085,H_element079]
  conduct = 2
  density = 1
  expand = 3
  formula = G4_POLYPROPYLENE
  name = G4_POLYPROPYLENE
  specific = 4
FEATURE [App::DocumentObjectGroupPython] C_element086  label="C_element : 044"  # scripted group (container) (typed FeaturePython)
  n = 8
  ref = C_element
FEATURE [App::DocumentObjectGroupPython] H_element080  label="H_element : 042"  # scripted group (container) (typed FeaturePython)
  n = 8
  ref = H_element
FEATURE [App::DocumentObjectGroupPython] G4_POLYSTYRENE  # scripted group (container) (typed FeaturePython)
  Dunit = g/cm3
  Dvalue = 1.06
  Group = -> [C_element086,H_element080]
  conduct = 2
  density = 1
  expand = 3
  formula = G4_POLYSTYRENE
  name = G4_POLYSTYRENE
  specific = 4
FEATURE [App::DocumentObjectGroupPython] C_element087  label="C_element : 045"  # scripted group (container) (typed FeaturePython)
  n = 2
  ref = C_element
FEATURE [App::DocumentObjectGroupPython] F_element014  label="F_element : 4"  # scripted group (container) (typed FeaturePython)
  n = 4
  ref = F_element
FEATURE [App::DocumentObjectGroupPython] G4_TEFLON  # scripted group (container) (typed FeaturePython)
  Dunit = g/cm3
  Dvalue = 2.2
  Group = -> [C_element087,F_element014]
  conduct = 2
  density = 1
  expand = 3
  formula = G4_TEFLON
  name = G4_TEFLON
  specific = 4
FEATURE [App::DocumentObjectGroupPython] C_element088  label="C_element : 046"  # scripted group (container) (typed FeaturePython)
  n = 2
  ref = C_element
FEATURE [App::DocumentObjectGroupPython] F_element015  label="F_element : 006"  # scripted group (container) (typed FeaturePython)
  n = 3
  ref = F_element
FEATURE [App::DocumentObjectGroupPython] Cl_element018  label="Cl_element : 008"  # scripted group (container) (typed FeaturePython)
  n = 1
  ref = Cl_element
FEATURE [App::DocumentObjectGroupPython] G4_POLYTRIFLUOROCHLOROETHYLENE  # scripted group (container) (typed FeaturePython)
  Dunit = g/cm3
  Dvalue = 2.1
  Group = -> [C_element088,F_element015,Cl_element018]
  conduct = 2
  density = 1
  expand = 3
  formula = G4_POLYTRIFLUOROCHLOROETHYLENE
  name = G4_POLYTRIFLUOROCHLOROETHYLENE
  specific = 4
FEATURE [App::DocumentObjectGroupPython] C_element089  label="C_element : 047"  # scripted group (container) (typed FeaturePython)
  n = 4
  ref = C_element
FEATURE [App::DocumentObjectGroupPython] H_element081  label="H_element : 043"  # scripted group (container) (typed FeaturePython)
  n = 6
  ref = H_element
FEATURE [App::DocumentObjectGroupPython] O_element081  label="O_element : 042"  # scripted group (container) (typed FeaturePython)
  n = 2
  ref = O_element
FEATURE [App::DocumentObjectGroupPython] G4_POLYVINYL_ACETATE  # scripted group (container) (typed FeaturePython)
  Dunit = g/cm3
  Dvalue = 1.19
  Group = -> [C_element089,H_element081,O_element081]
  conduct = 2
  density = 1
  expand = 3
  formula = G4_POLYVINYL_ACETATE
  name = G4_POLYVINYL_ACETATE
  specific = 4
FEATURE [App::DocumentObjectGroupPython] C_element090  label="C_element : 048"  # scripted group (container) (typed FeaturePython)
  n = 2
  ref = C_element
FEATURE [App::DocumentObjectGroupPython] H_element082  label="H_element : 044"  # scripted group (container) (typed FeaturePython)
  n = 4
  ref = H_element
FEATURE [App::DocumentObjectGroupPython] O_element082  label="O_element : 043"  # scripted group (container) (typed FeaturePython)
  n = 1
  ref = O_element
FEATURE [App::DocumentObjectGroupPython] G4_POLYVINYL_ALCOHOL  # scripted group (container) (typed FeaturePython)
  Dunit = g/cm3
  Dvalue = 1.3
  Group = -> [C_element090,H_element082,O_element082]
  conduct = 2
  density = 1
  expand = 3
  formula = G4_POLYVINYL_ALCOHOL
  name = G4_POLYVINYL_ALCOHOL
  specific = 4
FEATURE [App::DocumentObjectGroupPython] C_element091  label="C_element : 049"  # scripted group (container) (typed FeaturePython)
  n = 8
  ref = C_element
FEATURE [App::DocumentObjectGroupPython] H_element083  label="H_element : 045"  # scripted group (container) (typed FeaturePython)
  n = 14
  ref = H_element
FEATURE [App::DocumentObjectGroupPython] O_element083  label="O_element : 044"  # scripted group (container) (typed FeaturePython)
  n = 2
  ref = O_element
FEATURE [App::DocumentObjectGroupPython] G4_POLYVINYL_BUTYRAL  # scripted group (container) (typed FeaturePython)
  Dunit = g/cm3
  Dvalue = 1.12
  Group = -> [C_element091,H_element083,O_element083]
  conduct = 2
  density = 1
  expand = 3
  formula = G4_POLYVINYL_BUTYRAL
  name = G4_POLYVINYL_BUTYRAL
  specific = 4
FEATURE [App::DocumentObjectGroupPython] C_element092  label="C_element : 050"  # scripted group (container) (typed FeaturePython)
  n = 2
  ref = C_element
FEATURE [App::DocumentObjectGroupPython] H_element084  label="H_element : 046"  # scripted group (container) (typed FeaturePython)
  n = 3
  ref = H_element
FEATURE [App::DocumentObjectGroupPython] Cl_element019  label="Cl_element : 009"  # scripted group (container) (typed FeaturePython)
  n = 1
  ref = Cl_element
FEATURE [App::DocumentObjectGroupPython] G4_POLYVINYL_CHLORIDE  # scripted group (container) (typed FeaturePython)
  Dunit = g/cm3
  Dvalue = 1.3
  Group = -> [C_element092,H_element084,Cl_element019]
  conduct = 2
  density = 1
  expand = 3
  formula = G4_POLYVINYL_CHLORIDE
  name = G4_POLYVINYL_CHLORIDE
  specific = 4
FEATURE [App::DocumentObjectGroupPython] C_element093  label="C_element : 051"  # scripted group (container) (typed FeaturePython)
  n = 2
  ref = C_element
FEATURE [App::DocumentObjectGroupPython] H_element085  label="H_element : 047"  # scripted group (container) (typed FeaturePython)
  n = 2
  ref = H_element
FEATURE [App::DocumentObjectGroupPython] Cl_element020  label="Cl_element : 010"  # scripted group (container) (typed FeaturePython)
  n = 2
  ref = Cl_element
FEATURE [App::DocumentObjectGroupPython] G4_POLYVINYLIDENE_CHLORIDE  # scripted group (container) (typed FeaturePython)
  Dunit = g/cm3
  Dvalue = 1.7
  Group = -> [C_element093,H_element085,Cl_element020]
  conduct = 2
  density = 1
  expand = 3
  formula = G4_POLYVINYLIDENE_CHLORIDE
  name = G4_POLYVINYLIDENE_CHLORIDE
  specific = 4
FEATURE [App::DocumentObjectGroupPython] C_element094  label="C_element : 052"  # scripted group (container) (typed FeaturePython)
  n = 2
  ref = C_element
FEATURE [App::DocumentObjectGroupPython] H_element086  label="H_element : 048"  # scripted group (container) (typed FeaturePython)
  n = 2
  ref = H_element
FEATURE [App::DocumentObjectGroupPython] F_element016  label="F_element : 007"  # scripted group (container) (typed FeaturePython)
  n = 2
  ref = F_element
FEATURE [App::DocumentObjectGroupPython] G4_POLYVINYLIDENE_FLUORIDE  # scripted group (container) (typed FeaturePython)
  Dunit = g/cm3
  Dvalue = 1.76
  Group = -> [C_element094,H_element086,F_element016]
  conduct = 2
  density = 1
  expand = 3
  formula = G4_POLYVINYLIDENE_FLUORIDE
  name = G4_POLYVINYLIDENE_FLUORIDE
  specific = 4
FEATURE [App::DocumentObjectGroupPython] C_element095  label="C_element : 053"  # scripted group (container) (typed FeaturePython)
  n = 6
  ref = C_element
FEATURE [App::DocumentObjectGroupPython] H_element087  label="H_element : 9"  # scripted group (container) (typed FeaturePython)
  n = 9
  ref = H_element
FEATURE [App::DocumentObjectGroupPython] N_element037  label="N_element : 016"  # scripted group (container) (typed FeaturePython)
  n = 1
  ref = N_element
FEATURE [App::DocumentObjectGroupPython] O_element084  label="O_element : 045"  # scripted group (container) (typed FeaturePython)
  n = 1
  ref = O_element
FEATURE [App::DocumentObjectGroupPython] G4_POLYVINYL_PYRROLIDONE  # scripted group (container) (typed FeaturePython)
  Dunit = g/cm3
  Dvalue = 1.25
  Group = -> [C_element095,H_element087,N_element037,O_element084]
  conduct = 2
  density = 1
  expand = 3
  formula = G4_POLYVINYL_PYRROLIDONE
  name = G4_POLYVINYL_PYRROLIDONE
  specific = 4
FEATURE [App::DocumentObjectGroupPython] K_element008  label="K_element : 1"  # scripted group (container) (typed FeaturePython)
  n = 1
  ref = K_element
FEATURE [App::DocumentObjectGroupPython] I_element006  label="I_element : 003"  # scripted group (container) (typed FeaturePython)
  n = 1
  ref = I_element
FEATURE [App::DocumentObjectGroupPython] G4_POTASSIUM_IODIDE  # scripted group (container) (typed FeaturePython)
  Dunit = g/cm3
  Dvalue = 3.13
  Group = -> [K_element008,I_element006]
  conduct = 2
  density = 1
  expand = 3
  formula = G4_POTASSIUM_IODIDE
  name = G4_POTASSIUM_IODIDE
  specific = 4
FEATURE [App::DocumentObjectGroupPython] K_element009  label="K_element : 2"  # scripted group (container) (typed FeaturePython)
  n = 2
  ref = K_element
FEATURE [App::DocumentObjectGroupPython] O_element085  label="O_element : 046"  # scripted group (container) (typed FeaturePython)
  n = 1
  ref = O_element
FEATURE [App::DocumentObjectGroupPython] G4_POTASSIUM_OXIDE  # scripted group (container) (typed FeaturePython)
  Dunit = g/cm3
  Dvalue = 2.32
  Group = -> [K_element009,O_element085]
  conduct = 2
  density = 1
  expand = 3
  formula = G4_POTASSIUM_OXIDE
  name = G4_POTASSIUM_OXIDE
  specific = 4
FEATURE [App::DocumentObjectGroupPython] C_element096  label="C_element : 054"  # scripted group (container) (typed FeaturePython)
  n = 3
  ref = C_element
FEATURE [App::DocumentObjectGroupPython] H_element088  label="H_element : 049"  # scripted group (container) (typed FeaturePython)
  n = 8
  ref = H_element
FEATURE [App::DocumentObjectGroupPython] G4_PROPANE  # scripted group (container) (typed FeaturePython)
  Dunit = g/cm3
  Dvalue = 0.00187939
  Group = -> [C_element096,H_element088]
  conduct = 2
  density = 1
  expand = 3
  formula = G4_PROPANE
  name = G4_PROPANE
  specific = 4
FEATURE [App::DocumentObjectGroupPython] C_element097  label="C_element : 055"  # scripted group (container) (typed FeaturePython)
  n = 3
  ref = C_element
FEATURE [App::DocumentObjectGroupPython] H_element089  label="H_element : 050"  # scripted group (container) (typed FeaturePython)
  n = 8
  ref = H_element
FEATURE [App::DocumentObjectGroupPython] G4_lPROPANE  # scripted group (container) (typed FeaturePython)
  Dunit = g/cm3
  Dvalue = 0.43
  Group = -> [C_element097,H_element089]
  conduct = 2
  density = 1
  expand = 3
  formula = G4_lPROPANE
  name = G4_lPROPANE
  specific = 4
FEATURE [App::DocumentObjectGroupPython] C_element098  label="C_element : 056"  # scripted group (container) (typed FeaturePython)
  n = 3
  ref = C_element
FEATURE [App::DocumentObjectGroupPython] H_element090  label="H_element : 051"  # scripted group (container) (typed FeaturePython)
  n = 8
  ref = H_element
FEATURE [App::DocumentObjectGroupPython] O_element086  label="O_element : 047"  # scripted group (container) (typed FeaturePython)
  n = 1
  ref = O_element
FEATURE [App::DocumentObjectGroupPython] G4_N_PROPYL_ALCOHOL  label="G4_N-PROPYL_ALCOHOL"  # scripted group (container) (typed FeaturePython)
  Dunit = g/cm3
  Dvalue = 0.8035
  Group = -> [C_element098,H_element090,O_element086]
  conduct = 2
  density = 1
  expand = 3
  formula = G4_N-PROPYL_ALCOHOL
  name = G4_N-PROPYL_ALCOHOL
  specific = 4
FEATURE [App::DocumentObjectGroupPython] C_element099  label="C_element : 057"  # scripted group (container) (typed FeaturePython)
  n = 5
  ref = C_element
FEATURE [App::DocumentObjectGroupPython] H_element091  label="H_element : 052"  # scripted group (container) (typed FeaturePython)
  n = 5
  ref = H_element
FEATURE [App::DocumentObjectGroupPython] N_element038  label="N_element : 017"  # scripted group (container) (typed FeaturePython)
  n = 1
  ref = N_element
FEATURE [App::DocumentObjectGroupPython] G4_PYRIDINE  # scripted group (container) (typed FeaturePython)
  Dunit = g/cm3
  Dvalue = 0.9819
  Group = -> [C_element099,H_element091,N_element038]
  conduct = 2
  density = 1
  expand = 3
  formula = G4_PYRIDINE
  name = G4_PYRIDINE
  specific = 4
FEATURE [App::DocumentObjectGroupPython] H_element092  label="H_element : 0.144"  # scripted group (container) (typed FeaturePython)
  n = 0.143711
FEATURE [App::DocumentObjectGroupPython] C_element100  label="C_element : 0.856"  # scripted group (container) (typed FeaturePython)
  n = 0.856289
FEATURE [App::DocumentObjectGroupPython] G4_RUBBER_BUTYL  # scripted group (container) (typed FeaturePython)
  Dunit = g/cm3
  Dvalue = 0.92
  Group = -> [H_element092,C_element100]
  conduct = 2
  density = 1
  expand = 3
  formula = G4_RUBBER_BUTYL
  name = G4_RUBBER_BUTYL
  specific = 4
FEATURE [App::DocumentObjectGroupPython] H_element093  label="H_element : 0.118"  # scripted group (container) (typed FeaturePython)
  n = 0.118371
FEATURE [App::DocumentObjectGroupPython] C_element101  label="C_element : 0.882"  # scripted group (container) (typed FeaturePython)
  n = 0.881629
FEATURE [App::DocumentObjectGroupPython] G4_RUBBER_NATURAL  # scripted group (container) (typed FeaturePython)
  Dunit = g/cm3
  Dvalue = 0.92
  Group = -> [H_element093,C_element101]
  conduct = 2
  density = 1
  expand = 3
  formula = G4_RUBBER_NATURAL
  name = G4_RUBBER_NATURAL
  specific = 4
FEATURE [App::DocumentObjectGroupPython] H_element094  label="H_element : 0.145"  # scripted group (container) (typed FeaturePython)
  n = 0.05692
FEATURE [App::DocumentObjectGroupPython] C_element102  label="C_element : 0.543"  # scripted group (container) (typed FeaturePython)
  n = 0.542646
FEATURE [App::DocumentObjectGroupPython] Cl_element021  label="Cl_element : 0.400"  # scripted group (container) (typed FeaturePython)
  n = 0.400434
FEATURE [App::DocumentObjectGroupPython] G4_RUBBER_NEOPRENE  # scripted group (container) (typed FeaturePython)
  Dunit = g/cm3
  Dvalue = 1.23
  Group = -> [H_element094,C_element102,Cl_element021]
  conduct = 2
  density = 1
  expand = 3
  formula = G4_RUBBER_NEOPRENE
  name = G4_RUBBER_NEOPRENE
  specific = 4
FEATURE [App::DocumentObjectGroupPython] Si_element006  label="Si_element : 1"  # scripted group (container) (typed FeaturePython)
  n = 1
  ref = Si_element
FEATURE [App::DocumentObjectGroupPython] O_element087  label="O_element : 048"  # scripted group (container) (typed FeaturePython)
  n = 2
  ref = O_element
FEATURE [App::DocumentObjectGroupPython] G4_SILICON_DIOXIDE  # scripted group (container) (typed FeaturePython)
  Dunit = g/cm3
  Dvalue = 2.32
  Group = -> [Si_element006,O_element087]
  conduct = 2
  density = 1
  expand = 3
  formula = G4_SILICON_DIOXIDE
  name = G4_SILICON_DIOXIDE
  specific = 4
FEATURE [App::DocumentObjectGroupPython] Ag_element002  label="Ag_element : 1"  # scripted group (container) (typed FeaturePython)
  n = 1
  ref = Ag_element
FEATURE [App::DocumentObjectGroupPython] Br_element005  label="Br_element : 003"  # scripted group (container) (typed FeaturePython)
  n = 1
  ref = Br_element
FEATURE [App::DocumentObjectGroupPython] G4_SILVER_BROMIDE  # scripted group (container) (typed FeaturePython)
  Dunit = g/cm3
  Dvalue = 6.473
  Group = -> [Ag_element002,Br_element005]
  conduct = 2
  density = 1
  expand = 3
  formula = G4_SILVER_BROMIDE
  name = G4_SILVER_BROMIDE
  specific = 4
FEATURE [App::DocumentObjectGroupPython] Ag_element003  label="Ag_element : 002"  # scripted group (container) (typed FeaturePython)
  n = 1
  ref = Ag_element
FEATURE [App::DocumentObjectGroupPython] Cl_element022  label="Cl_element : 011"  # scripted group (container) (typed FeaturePython)
  n = 1
  ref = Cl_element
FEATURE [App::DocumentObjectGroupPython] G4_SILVER_CHLORIDE  # scripted group (container) (typed FeaturePython)
  Dunit = g/cm3
  Dvalue = 5.56
  Group = -> [Ag_element003,Cl_element022]
  conduct = 2
  density = 1
  expand = 3
  formula = G4_SILVER_CHLORIDE
  name = G4_SILVER_CHLORIDE
  specific = 4
FEATURE [App::DocumentObjectGroupPython] Br_element006  label="Br_element : 0.423"  # scripted group (container) (typed FeaturePython)
  n = 0.422895
FEATURE [App::DocumentObjectGroupPython] Ag_element004  label="Ag_element : 0.574"  # scripted group (container) (typed FeaturePython)
  n = 0.573748
FEATURE [App::DocumentObjectGroupPython] I_element007  label="I_element : 0.649"  # scripted group (container) (typed FeaturePython)
  n = 0.003357
FEATURE [App::DocumentObjectGroupPython] G4_SILVER_HALIDES  # scripted group (container) (typed FeaturePython)
  Dunit = g/cm3
  Dvalue = 6.47
  Group = -> [Br_element006,Ag_element004,I_element007]
  conduct = 2
  density = 1
  expand = 3
  formula = G4_SILVER_HALIDES
  name = G4_SILVER_HALIDES
  specific = 4
FEATURE [App::DocumentObjectGroupPython] Ag_element005  label="Ag_element : 003"  # scripted group (container) (typed FeaturePython)
  n = 1
  ref = Ag_element
FEATURE [App::DocumentObjectGroupPython] I_element008  label="I_element : 004"  # scripted group (container) (typed FeaturePython)
  n = 1
  ref = I_element
FEATURE [App::DocumentObjectGroupPython] G4_SILVER_IODIDE  # scripted group (container) (typed FeaturePython)
  Dunit = g/cm3
  Dvalue = 6.01
  Group = -> [Ag_element005,I_element008]
  conduct = 2
  density = 1
  expand = 3
  formula = G4_SILVER_IODIDE
  name = G4_SILVER_IODIDE
  specific = 4
FEATURE [App::DocumentObjectGroupPython] H_element095  label="H_element : 0.100"  # scripted group (container) (typed FeaturePython)
  n = 0.1
FEATURE [App::DocumentObjectGroupPython] C_element103  label="C_element : 0.204"  # scripted group (container) (typed FeaturePython)
  n = 0.204
FEATURE [App::DocumentObjectGroupPython] N_element039  label="N_element : 0.759"  # scripted group (container) (typed FeaturePython)
  n = 0.042
FEATURE [App::DocumentObjectGroupPython] O_element088  label="O_element : 0.645"  # scripted group (container) (typed FeaturePython)
  n = 0.645
FEATURE [App::DocumentObjectGroupPython] Na_element013  label="Na_element : 0.100"  # scripted group (container) (typed FeaturePython)
  n = 0.002
FEATURE [App::DocumentObjectGroupPython] P_element009  label="P_element : 0.107"  # scripted group (container) (typed FeaturePython)
  n = 0.001
FEATURE [App::DocumentObjectGroupPython] S_element020  label="S_element : 0.021"  # scripted group (container) (typed FeaturePython)
  n = 0.002
FEATURE [App::DocumentObjectGroupPython] Cl_element023  label="Cl_element : 0.590"  # scripted group (container) (typed FeaturePython)
  n = 0.003
FEATURE [App::DocumentObjectGroupPython] K_element010  label="K_element : 0.001"  # scripted group (container) (typed FeaturePython)
  n = 0.001
FEATURE [App::DocumentObjectGroupPython] G4_SKIN_ICRP  # scripted group (container) (typed FeaturePython)
  Dunit = g/cm3
  Dvalue = 1.09
  Group = -> [H_element095,C_element103,N_element039,O_element088,Na_element013,P_element009,S_element020,Cl_element023,K_element010]
  conduct = 2
  density = 1
  expand = 3
  formula = G4_SKIN_ICRP
  name = G4_SKIN_ICRP
  specific = 4
FEATURE [App::DocumentObjectGroupPython] Na_element014  label="Na_element : 2"  # scripted group (container) (typed FeaturePython)
  n = 2
  ref = Na_element
FEATURE [App::DocumentObjectGroupPython] C_element104  label="C_element : 058"  # scripted group (container) (typed FeaturePython)
  n = 1
  ref = C_element
FEATURE [App::DocumentObjectGroupPython] O_element089  label="O_element : 049"  # scripted group (container) (typed FeaturePython)
  n = 3
  ref = O_element
FEATURE [App::DocumentObjectGroupPython] G4_SODIUM_CARBONATE  # scripted group (container) (typed FeaturePython)
  Dunit = g/cm3
  Dvalue = 2.532
  Group = -> [Na_element014,C_element104,O_element089]
  conduct = 2
  density = 1
  expand = 3
  formula = G4_SODIUM_CARBONATE
  name = G4_SODIUM_CARBONATE
  specific = 4
FEATURE [App::DocumentObjectGroupPython] Na_element015  label="Na_element : 1"  # scripted group (container) (typed FeaturePython)
  n = 1
  ref = Na_element
FEATURE [App::DocumentObjectGroupPython] I_element009  label="I_element : 005"  # scripted group (container) (typed FeaturePython)
  n = 1
  ref = I_element
FEATURE [App::DocumentObjectGroupPython] G4_SODIUM_IODIDE  # scripted group (container) (typed FeaturePython)
  Dunit = g/cm3
  Dvalue = 3.667
  Group = -> [Na_element015,I_element009]
  conduct = 2
  density = 1
  expand = 3
  formula = G4_SODIUM_IODIDE
  name = G4_SODIUM_IODIDE
  specific = 4
FEATURE [App::DocumentObjectGroupPython] Na_element016  label="Na_element : 003"  # scripted group (container) (typed FeaturePython)
  n = 2
  ref = Na_element
FEATURE [App::DocumentObjectGroupPython] O_element090  label="O_element : 050"  # scripted group (container) (typed FeaturePython)
  n = 1
  ref = O_element
FEATURE [App::DocumentObjectGroupPython] G4_SODIUM_MONOXIDE  # scripted group (container) (typed FeaturePython)
  Dunit = g/cm3
  Dvalue = 2.27
  Group = -> [Na_element016,O_element090]
  conduct = 2
  density = 1
  expand = 3
  formula = G4_SODIUM_MONOXIDE
  name = G4_SODIUM_MONOXIDE
  specific = 4
FEATURE [App::DocumentObjectGroupPython] Na_element017  label="Na_element : 004"  # scripted group (container) (typed FeaturePython)
  n = 1
  ref = Na_element
FEATURE [App::DocumentObjectGroupPython] N_element040  label="N_element : 018"  # scripted group (container) (typed FeaturePython)
  n = 1
  ref = N_element
FEATURE [App::DocumentObjectGroupPython] O_element091  label="O_element : 051"  # scripted group (container) (typed FeaturePython)
  n = 3
  ref = O_element
FEATURE [App::DocumentObjectGroupPython] G4_SODIUM_NITRATE  # scripted group (container) (typed FeaturePython)
  Dunit = g/cm3
  Dvalue = 2.261
  Group = -> [Na_element017,N_element040,O_element091]
  conduct = 2
  density = 1
  expand = 3
  formula = G4_SODIUM_NITRATE
  name = G4_SODIUM_NITRATE
  specific = 4
FEATURE [App::DocumentObjectGroupPython] C_element105  label="C_element : 059"  # scripted group (container) (typed FeaturePython)
  n = 14
  ref = C_element
FEATURE [App::DocumentObjectGroupPython] H_element096  label="H_element : 053"  # scripted group (container) (typed FeaturePython)
  n = 12
  ref = H_element
FEATURE [App::DocumentObjectGroupPython] G4_STILBENE  # scripted group (container) (typed FeaturePython)
  Dunit = g/cm3
  Dvalue = 0.9707
  Group = -> [C_element105,H_element096]
  conduct = 2
  density = 1
  expand = 3
  formula = G4_STILBENE
  name = G4_STILBENE
  specific = 4
FEATURE [App::DocumentObjectGroupPython] C_element106  label="C_element : 12"  # scripted group (container) (typed FeaturePython)
  n = 12
  ref = C_element
FEATURE [App::DocumentObjectGroupPython] H_element097  label="H_element : 22"  # scripted group (container) (typed FeaturePython)
  n = 22
  ref = H_element
FEATURE [App::DocumentObjectGroupPython] O_element092  label="O_element : 11"  # scripted group (container) (typed FeaturePython)
  n = 11
  ref = O_element
FEATURE [App::DocumentObjectGroupPython] G4_SUCROSE  # scripted group (container) (typed FeaturePython)
  Dunit = g/cm3
  Dvalue = 1.5805
  Group = -> [C_element106,H_element097,O_element092]
  conduct = 2
  density = 1
  expand = 3
  formula = G4_SUCROSE
  name = G4_SUCROSE
  specific = 4
FEATURE [App::DocumentObjectGroupPython] C_element107  label="C_element : 18"  # scripted group (container) (typed FeaturePython)
  n = 18
  ref = C_element
FEATURE [App::DocumentObjectGroupPython] H_element098  label="H_element : 054"  # scripted group (container) (typed FeaturePython)
  n = 14
  ref = H_element
FEATURE [App::DocumentObjectGroupPython] G4_TERPHENYL  # scripted group (container) (typed FeaturePython)
  Dunit = g/cm3
  Dvalue = 1.24
  Group = -> [C_element107,H_element098]
  conduct = 2
  density = 1
  expand = 3
  formula = G4_TERPHENYL
  name = G4_TERPHENYL
  specific = 4
FEATURE [App::DocumentObjectGroupPython] H_element099  label="H_element : 0.146"  # scripted group (container) (typed FeaturePython)
  n = 0.106
FEATURE [App::DocumentObjectGroupPython] C_element108  label="C_element : 0.883"  # scripted group (container) (typed FeaturePython)
  n = 0.099
FEATURE [App::DocumentObjectGroupPython] N_element041  label="N_element : 0.020"  # scripted group (container) (typed FeaturePython)
  n = 0.02
FEATURE [App::DocumentObjectGroupPython] O_element093  label="O_element : 0.766"  # scripted group (container) (typed FeaturePython)
  n = 0.766
FEATURE [App::DocumentObjectGroupPython] Na_element018  label="Na_element : 0.101"  # scripted group (container) (typed FeaturePython)
  n = 0.002
FEATURE [App::DocumentObjectGroupPython] P_element010  label="P_element : 0.108"  # scripted group (container) (typed FeaturePython)
  n = 0.001
FEATURE [App::DocumentObjectGroupPython] S_element021  label="S_element : 0.022"  # scripted group (container) (typed FeaturePython)
  n = 0.002
FEATURE [App::DocumentObjectGroupPython] Cl_element024  label="Cl_element : 0.002"  # scripted group (container) (typed FeaturePython)
  n = 0.002
FEATURE [App::DocumentObjectGroupPython] K_element011  label="K_element : 0.017"  # scripted group (container) (typed FeaturePython)
  n = 0.002
FEATURE [App::DocumentObjectGroupPython] G4_TESTIS_ICRP  # scripted group (container) (typed FeaturePython)
  Dunit = g/cm3
  Dvalue = 1.04
  Group = -> [H_element099,C_element108,N_element041,O_element093,Na_element018,P_element010,S_element021,Cl_element024,K_element011]
  conduct = 2
  density = 1
  expand = 3
  formula = G4_TESTIS_ICRP
  name = G4_TESTIS_ICRP
  specific = 4
FEATURE [App::DocumentObjectGroupPython] C_element109  label="C_element : 060"  # scripted group (container) (typed FeaturePython)
  n = 2
  ref = C_element
FEATURE [App::DocumentObjectGroupPython] Cl_element025  label="Cl_element : 012"  # scripted group (container) (typed FeaturePython)
  n = 4
  ref = Cl_element
FEATURE [App::DocumentObjectGroupPython] G4_TETRACHLOROETHYLENE  # scripted group (container) (typed FeaturePython)
  Dunit = g/cm3
  Dvalue = 1.625
  Group = -> [C_element109,Cl_element025]
  conduct = 2
  density = 1
  expand = 3
  formula = G4_TETRACHLOROETHYLENE
  name = G4_TETRACHLOROETHYLENE
  specific = 4
FEATURE [App::DocumentObjectGroupPython] Tl_element001  label="Tl_element : 1"  # scripted group (container) (typed FeaturePython)
  n = 1
  ref = Tl_element
FEATURE [App::DocumentObjectGroupPython] Cl_element026  label="Cl_element : 013"  # scripted group (container) (typed FeaturePython)
  n = 1
  ref = Cl_element
FEATURE [App::DocumentObjectGroupPython] G4_THALLIUM_CHLORIDE  # scripted group (container) (typed FeaturePython)
  Dunit = g/cm3
  Dvalue = 7.004
  Group = -> [Tl_element001,Cl_element026]
  conduct = 2
  density = 1
  expand = 3
  formula = G4_THALLIUM_CHLORIDE
  name = G4_THALLIUM_CHLORIDE
  specific = 4
FEATURE [App::DocumentObjectGroupPython] H_element100  label="H_element : 0.147"  # scripted group (container) (typed FeaturePython)
  n = 0.105
FEATURE [App::DocumentObjectGroupPython] C_element110  label="C_element : 0.256"  # scripted group (container) (typed FeaturePython)
  n = 0.256
FEATURE [App::DocumentObjectGroupPython] N_element042  label="N_element : 0.760"  # scripted group (container) (typed FeaturePython)
  n = 0.027
FEATURE [App::DocumentObjectGroupPython] O_element094  label="O_element : 0.602"  # scripted group (container) (typed FeaturePython)
  n = 0.602
FEATURE [App::DocumentObjectGroupPython] Na_element019  label="Na_element : 0.102"  # scripted group (container) (typed FeaturePython)
  n = 0.001
FEATURE [App::DocumentObjectGroupPython] P_element011  label="P_element : 0.109"  # scripted group (container) (typed FeaturePython)
  n = 0.002
FEATURE [App::DocumentObjectGroupPython] S_element022  label="S_element : 0.023"  # scripted group (container) (typed FeaturePython)
  n = 0.003
FEATURE [App::DocumentObjectGroupPython] Cl_element027  label="Cl_element : 0.591"  # scripted group (container) (typed FeaturePython)
  n = 0.002
FEATURE [App::DocumentObjectGroupPython] K_element012  label="K_element : 0.018"  # scripted group (container) (typed FeaturePython)
  n = 0.002
FEATURE [App::DocumentObjectGroupPython] G4_TISSUE_SOFT_ICRP  # scripted group (container) (typed FeaturePython)
  Dunit = g/cm3
  Dvalue = 1.03
  Group = -> [H_element100,C_element110,N_element042,O_element094,Na_element019,P_element011,S_element022,Cl_element027,K_element012]
  conduct = 2
  density = 1
  expand = 3
  formula = G4_TISSUE_SOFT_ICRP
  name = G4_TISSUE_SOFT_ICRP
  specific = 4
FEATURE [App::DocumentObjectGroupPython] H_element101  label="H_element : 0.148"  # scripted group (container) (typed FeaturePython)
  n = 0.101
FEATURE [App::DocumentObjectGroupPython] C_element111  label="C_element : 0.111"  # scripted group (container) (typed FeaturePython)
  n = 0.111
FEATURE [App::DocumentObjectGroupPython] N_element043  label="N_element : 0.026"  # scripted group (container) (typed FeaturePython)
  n = 0.026
FEATURE [App::DocumentObjectGroupPython] O_element095  label="O_element : 0.762"  # scripted group (container) (typed FeaturePython)
  n = 0.762
FEATURE [App::DocumentObjectGroupPython] G4_TISSUE_SOFT_ICRU_4  label="G4_TISSUE_SOFT_ICRU-4"  # scripted group (container) (typed FeaturePython)
  Dunit = g/cm3
  Dvalue = 1
  Group = -> [H_element101,C_element111,N_element043,O_element095]
  conduct = 2
  density = 1
  expand = 3
  formula = G4_TISSUE_SOFT_ICRU-4
  name = G4_TISSUE_SOFT_ICRU-4
  specific = 4
FEATURE [App::DocumentObjectGroupPython] H_element102  label="H_element : 0.149"  # scripted group (container) (typed FeaturePython)
  n = 0.101869
FEATURE [App::DocumentObjectGroupPython] C_element112  label="C_element : 0.456"  # scripted group (container) (typed FeaturePython)
  n = 0.456179
FEATURE [App::DocumentObjectGroupPython] N_element044  label="N_element : 0.761"  # scripted group (container) (typed FeaturePython)
  n = 0.035172
FEATURE [App::DocumentObjectGroupPython] O_element096  label="O_element : 0.407"  # scripted group (container) (typed FeaturePython)
  n = 0.40678
FEATURE [App::DocumentObjectGroupPython] G4_TISSUE_METHANE  label="G4_TISSUE-METHANE"  # scripted group (container) (typed FeaturePython)
  Dunit = g/cm3
  Dvalue = 0.00106409
  Group = -> [H_element102,C_element112,N_element044,O_element096]
  conduct = 2
  density = 1
  expand = 3
  formula = G4_TISSUE-METHANE
  name = G4_TISSUE-METHANE
  specific = 4
FEATURE [App::DocumentObjectGroupPython] H_element103  label="H_element : 0.103"  # scripted group (container) (typed FeaturePython)
  n = 0.102672
FEATURE [App::DocumentObjectGroupPython] C_element113  label="C_element : 0.569"  # scripted group (container) (typed FeaturePython)
  n = 0.56894
FEATURE [App::DocumentObjectGroupPython] N_element045  label="N_element : 0.762"  # scripted group (container) (typed FeaturePython)
  n = 0.035022
FEATURE [App::DocumentObjectGroupPython] O_element097  label="O_element : 0.293"  # scripted group (container) (typed FeaturePython)
  n = 0.293366
FEATURE [App::DocumentObjectGroupPython] G4_TISSUE_PROPANE  label="G4_TISSUE-PROPANE"  # scripted group (container) (typed FeaturePython)
  Dunit = g/cm3
  Dvalue = 0.00182628
  Group = -> [H_element103,C_element113,N_element045,O_element097]
  conduct = 2
  density = 1
  expand = 3
  formula = G4_TISSUE-PROPANE
  name = G4_TISSUE-PROPANE
  specific = 4
FEATURE [App::DocumentObjectGroupPython] Ti_element003  label="Ti_element : 1"  # scripted group (container) (typed FeaturePython)
  n = 1
  ref = Ti_element
FEATURE [App::DocumentObjectGroupPython] O_element098  label="O_element : 052"  # scripted group (container) (typed FeaturePython)
  n = 2
  ref = O_element
FEATURE [App::DocumentObjectGroupPython] G4_TITANIUM_DIOXIDE  # scripted group (container) (typed FeaturePython)
  Dunit = g/cm3
  Dvalue = 4.26
  Group = -> [Ti_element003,O_element098]
  conduct = 2
  density = 1
  expand = 3
  formula = G4_TITANIUM_DIOXIDE
  name = G4_TITANIUM_DIOXIDE
  specific = 4
FEATURE [App::DocumentObjectGroupPython] C_element114  label="C_element : 061"  # scripted group (container) (typed FeaturePython)
  n = 7
  ref = C_element
FEATURE [App::DocumentObjectGroupPython] H_element104  label="H_element : 055"  # scripted group (container) (typed FeaturePython)
  n = 8
  ref = H_element
FEATURE [App::DocumentObjectGroupPython] G4_TOLUENE  # scripted group (container) (typed FeaturePython)
  Dunit = g/cm3
  Dvalue = 0.8669
  Group = -> [C_element114,H_element104]
  conduct = 2
  density = 1
  expand = 3
  formula = G4_TOLUENE
  name = G4_TOLUENE
  specific = 4
FEATURE [App::DocumentObjectGroupPython] C_element115  label="C_element : 062"  # scripted group (container) (typed FeaturePython)
  n = 2
  ref = C_element
FEATURE [App::DocumentObjectGroupPython] H_element105  label="H_element : 056"  # scripted group (container) (typed FeaturePython)
  n = 1
  ref = H_element
FEATURE [App::DocumentObjectGroupPython] Cl_element028  label="Cl_element : 014"  # scripted group (container) (typed FeaturePython)
  n = 3
  ref = Cl_element
FEATURE [App::DocumentObjectGroupPython] G4_TRICHLOROETHYLENE  # scripted group (container) (typed FeaturePython)
  Dunit = g/cm3
  Dvalue = 1.46
  Group = -> [C_element115,H_element105,Cl_element028]
  conduct = 2
  density = 1
  expand = 3
  formula = G4_TRICHLOROETHYLENE
  name = G4_TRICHLOROETHYLENE
  specific = 4
FEATURE [App::DocumentObjectGroupPython] C_element116  label="C_element : 063"  # scripted group (container) (typed FeaturePython)
  n = 6
  ref = C_element
FEATURE [App::DocumentObjectGroupPython] H_element106  label="H_element : 15"  # scripted group (container) (typed FeaturePython)
  n = 15
  ref = H_element
FEATURE [App::DocumentObjectGroupPython] O_element099  label="O_element : 053"  # scripted group (container) (typed FeaturePython)
  n = 4
  ref = O_element
FEATURE [App::DocumentObjectGroupPython] P_element012  label="P_element : 1"  # scripted group (container) (typed FeaturePython)
  n = 1
  ref = P_element
FEATURE [App::DocumentObjectGroupPython] G4_TRIETHYL_PHOSPHATE  # scripted group (container) (typed FeaturePython)
  Dunit = g/cm3
  Dvalue = 1.07
  Group = -> [C_element116,H_element106,O_element099,P_element012]
  conduct = 2
  density = 1
  expand = 3
  formula = G4_TRIETHYL_PHOSPHATE
  name = G4_TRIETHYL_PHOSPHATE
  specific = 4
FEATURE [App::DocumentObjectGroupPython] W_element003  label="W_element : 003"  # scripted group (container) (typed FeaturePython)
  n = 1
  ref = W_element
FEATURE [App::DocumentObjectGroupPython] F_element017  label="F_element : 6"  # scripted group (container) (typed FeaturePython)
  n = 6
  ref = F_element
FEATURE [App::DocumentObjectGroupPython] G4_TUNGSTEN_HEXAFLUORIDE  # scripted group (container) (typed FeaturePython)
  Dunit = g/cm3
  Dvalue = 2.4
  Group = -> [W_element003,F_element017]
  conduct = 2
  density = 1
  expand = 3
  formula = G4_TUNGSTEN_HEXAFLUORIDE
  name = G4_TUNGSTEN_HEXAFLUORIDE
  specific = 4
FEATURE [App::DocumentObjectGroupPython] U_element001  label="U_element : 1"  # scripted group (container) (typed FeaturePython)
  n = 1
  ref = U_element
FEATURE [App::DocumentObjectGroupPython] C_element117  label="C_element : 064"  # scripted group (container) (typed FeaturePython)
  n = 2
  ref = C_element
FEATURE [App::DocumentObjectGroupPython] G4_URANIUM_DICARBIDE  # scripted group (container) (typed FeaturePython)
  Dunit = g/cm3
  Dvalue = 11.28
  Group = -> [U_element001,C_element117]
  conduct = 2
  density = 1
  expand = 3
  formula = G4_URANIUM_DICARBIDE
  name = G4_URANIUM_DICARBIDE
  specific = 4
FEATURE [App::DocumentObjectGroupPython] U_element002  label="U_element : 002"  # scripted group (container) (typed FeaturePython)
  n = 1
  ref = U_element
FEATURE [App::DocumentObjectGroupPython] C_element118  label="C_element : 065"  # scripted group (container) (typed FeaturePython)
  n = 1
  ref = C_element
FEATURE [App::DocumentObjectGroupPython] G4_URANIUM_MONOCARBIDE  # scripted group (container) (typed FeaturePython)
  Dunit = g/cm3
  Dvalue = 13.63
  Group = -> [U_element002,C_element118]
  conduct = 2
  density = 1
  expand = 3
  formula = G4_URANIUM_MONOCARBIDE
  name = G4_URANIUM_MONOCARBIDE
  specific = 4
FEATURE [App::DocumentObjectGroupPython] U_element003  label="U_element : 003"  # scripted group (container) (typed FeaturePython)
  n = 1
  ref = U_element
FEATURE [App::DocumentObjectGroupPython] O_element100  label="O_element : 054"  # scripted group (container) (typed FeaturePython)
  n = 2
  ref = O_element
FEATURE [App::DocumentObjectGroupPython] G4_URANIUM_OXIDE  # scripted group (container) (typed FeaturePython)
  Dunit = g/cm3
  Dvalue = 10.96
  Group = -> [U_element003,O_element100]
  conduct = 2
  density = 1
  expand = 3
  formula = G4_URANIUM_OXIDE
  name = G4_URANIUM_OXIDE
  specific = 4
FEATURE [App::DocumentObjectGroupPython] C_element119  label="C_element : 066"  # scripted group (container) (typed FeaturePython)
  n = 1
  ref = C_element
FEATURE [App::DocumentObjectGroupPython] H_element107  label="H_element : 057"  # scripted group (container) (typed FeaturePython)
  n = 4
  ref = H_element
FEATURE [App::DocumentObjectGroupPython] N_element046  label="N_element : 019"  # scripted group (container) (typed FeaturePython)
  n = 2
  ref = N_element
FEATURE [App::DocumentObjectGroupPython] O_element101  label="O_element : 055"  # scripted group (container) (typed FeaturePython)
  n = 1
  ref = O_element
FEATURE [App::DocumentObjectGroupPython] G4_UREA  # scripted group (container) (typed FeaturePython)
  Dunit = g/cm3
  Dvalue = 1.323
  Group = -> [C_element119,H_element107,N_element046,O_element101]
  conduct = 2
  density = 1
  expand = 3
  formula = G4_UREA
  name = G4_UREA
  specific = 4
FEATURE [App::DocumentObjectGroupPython] C_element120  label="C_element : 067"  # scripted group (container) (typed FeaturePython)
  n = 5
  ref = C_element
FEATURE [App::DocumentObjectGroupPython] H_element108  label="H_element : 058"  # scripted group (container) (typed FeaturePython)
  n = 11
  ref = H_element
FEATURE [App::DocumentObjectGroupPython] N_element047  label="N_element : 020"  # scripted group (container) (typed FeaturePython)
  n = 1
  ref = N_element
FEATURE [App::DocumentObjectGroupPython] O_element102  label="O_element : 056"  # scripted group (container) (typed FeaturePython)
  n = 2
  ref = O_element
FEATURE [App::DocumentObjectGroupPython] G4_VALINE  # scripted group (container) (typed FeaturePython)
  Dunit = g/cm3
  Dvalue = 1.23
  Group = -> [C_element120,H_element108,N_element047,O_element102]
  conduct = 2
  density = 1
  expand = 3
  formula = G4_VALINE
  name = G4_VALINE
  specific = 4
FEATURE [App::DocumentObjectGroupPython] H_element109  label="H_element : 0.009"  # scripted group (container) (typed FeaturePython)
  n = 0.009417
FEATURE [App::DocumentObjectGroupPython] C_element121  label="C_element : 0.281"  # scripted group (container) (typed FeaturePython)
  n = 0.280555
FEATURE [App::DocumentObjectGroupPython] F_element018  label="F_element : 0.710"  # scripted group (container) (typed FeaturePython)
  n = 0.710028
FEATURE [App::DocumentObjectGroupPython] G4_VITON  # scripted group (container) (typed FeaturePython)
  Dunit = g/cm3
  Dvalue = 1.8
  Group = -> [H_element109,C_element121,F_element018]
  conduct = 2
  density = 1
  expand = 3
  formula = G4_VITON
  name = G4_VITON
  specific = 4
FEATURE [App::DocumentObjectGroupPython] H_element110  label="H_element : 059"  # scripted group (container) (typed FeaturePython)
  n = 2
  ref = H_element
FEATURE [App::DocumentObjectGroupPython] O_element103  label="O_element : 057"  # scripted group (container) (typed FeaturePython)
  n = 1
  ref = O_element
FEATURE [App::DocumentObjectGroupPython] G4_WATER  # scripted group (container) (typed FeaturePython)
  Dunit = g/cm3
  Dvalue = 1
  Group = -> [H_element110,O_element103]
  conduct = 2
  density = 1
  expand = 3
  formula = G4_WATER
  name = G4_WATER
  specific = 4
FEATURE [App::DocumentObjectGroupPython] H_element111  label="H_element : 060"  # scripted group (container) (typed FeaturePython)
  n = 2
  ref = H_element
FEATURE [App::DocumentObjectGroupPython] O_element104  label="O_element : 058"  # scripted group (container) (typed FeaturePython)
  n = 1
  ref = O_element
FEATURE [App::DocumentObjectGroupPython] G4_WATER_VAPOR  # scripted group (container) (typed FeaturePython)
  Dunit = g/cm3
  Dvalue = 0.000756182
  Group = -> [H_element111,O_element104]
  conduct = 2
  density = 1
  expand = 3
  formula = G4_WATER_VAPOR
  name = G4_WATER_VAPOR
  specific = 4
FEATURE [App::DocumentObjectGroupPython] C_element122  label="C_element : 068"  # scripted group (container) (typed FeaturePython)
  n = 8
  ref = C_element
FEATURE [App::DocumentObjectGroupPython] H_element112  label="H_element : 061"  # scripted group (container) (typed FeaturePython)
  n = 10
  ref = H_element
FEATURE [App::DocumentObjectGroupPython] G4_XYLENE  # scripted group (container) (typed FeaturePython)
  Dunit = g/cm3
  Dvalue = 0.87
  Group = -> [C_element122,H_element112]
  conduct = 2
  density = 1
  expand = 3
  formula = G4_XYLENE
  name = G4_XYLENE
  specific = 4
FEATURE [App::DocumentObjectGroupPython] C_element123  label="C_element : 069"  # scripted group (container) (typed FeaturePython)
  n = 1
  ref = C_element
FEATURE [App::DocumentObjectGroupPython] G4_GRAPHITE  # scripted group (container) (typed FeaturePython)
  Dunit = g/cm3
  Dvalue = 2.21
  Group = -> [C_element123]
  conduct = 2
  density = 1
  expand = 3
  formula = G4_GRAPHITE
  name = G4_GRAPHITE
  specific = 4
FEATURE [App::DocumentObjectGroupPython] NIST  # scripted group (container) (typed FeaturePython)
  Group = -> [G4_A_150_TISSUE,G4_ACETONE,G4_ACETYLENE,G4_ADENINE,G4_ADIPOSE_TISSUE_ICRP,G4_AIR,G4_ALANINE,G4_ALUMINUM_OXIDE,G4_AMBER,G4_AMMONIA,G4_ANILINE,G4_ANTHRACENE,G4_B_100_BONE,G4_BAKELITE,G4_BARIUM_FLUORIDE,G4_BARIUM_SULFATE,G4_BENZENE,G4_BERYLLIUM_OXIDE,G4_BGO,G4_BLOOD_ICRP,G4_BONE_COMPACT_ICRU,G4_BONE_CORTICAL_ICRP,G4_BORON_CARBIDE,G4_BORON_OXIDE,G4_BRAIN_ICRP,G4_BUTANE,G4_N_BUTYL_ALCOHOL,G4_C_552,+152 more]
FEATURE [App::DocumentObjectGroupPython] H_element113  label="H_element : 062"  # scripted group (container) (typed FeaturePython)
  n = 1
  ref = H_element
FEATURE [App::DocumentObjectGroupPython] G4_H  # scripted group (container) (typed FeaturePython)
  Dunit = g/cm3
  Dvalue = 8.3748e-05
  Group = -> [H_element113]
  conduct = 2
  density = 1
  expand = 3
  formula = H
  name = G4_H
  specific = 4
FEATURE [App::DocumentObjectGroupPython] He_element001  label="He_element : 1"  # scripted group (container) (typed FeaturePython)
  n = 1
  ref = He_element
FEATURE [App::DocumentObjectGroupPython] G4_He  # scripted group (container) (typed FeaturePython)
  Dunit = g/cm3
  Dvalue = 0.000166322
  Group = -> [He_element001]
  conduct = 2
  density = 1
  expand = 3
  formula = He
  name = G4_He
  specific = 4
FEATURE [App::DocumentObjectGroupPython] Li_element008  label="Li_element : 008"  # scripted group (container) (typed FeaturePython)
  n = 1
  ref = Li_element
FEATURE [App::DocumentObjectGroupPython] G4_Li  # scripted group (container) (typed FeaturePython)
  Dunit = g/cm3
  Dvalue = 0.534
  Group = -> [Li_element008]
  conduct = 2
  density = 1
  expand = 3
  formula = Li
  name = G4_Li
  specific = 4
FEATURE [App::DocumentObjectGroupPython] Be_element002  label="Be_element : 002"  # scripted group (container) (typed FeaturePython)
  n = 1
  ref = Be_element
FEATURE [App::DocumentObjectGroupPython] G4_Be  # scripted group (container) (typed FeaturePython)
  Dunit = g/cm3
  Dvalue = 1.848
  Group = -> [Be_element002]
  conduct = 2
  density = 1
  expand = 3
  formula = Be
  name = G4_Be
  specific = 4
FEATURE [App::DocumentObjectGroupPython] B_element007  label="B_element : 007"  # scripted group (container) (typed FeaturePython)
  n = 1
  ref = B_element
FEATURE [App::DocumentObjectGroupPython] G4_B  # scripted group (container) (typed FeaturePython)
  Dunit = g/cm3
  Dvalue = 2.37
  Group = -> [B_element007]
  conduct = 2
  density = 1
  expand = 3
  formula = B
  name = G4_B
  specific = 4
FEATURE [App::DocumentObjectGroupPython] C_element124  label="C_element : 070"  # scripted group (container) (typed FeaturePython)
  n = 1
  ref = C_element
FEATURE [App::DocumentObjectGroupPython] G4_C  # scripted group (container) (typed FeaturePython)
  Dunit = g/cm3
  Dvalue = 2
  Group = -> [C_element124]
  conduct = 2
  density = 1
  expand = 3
  formula = C
  name = G4_C
  specific = 4
FEATURE [App::DocumentObjectGroupPython] N_element048  label="N_element : 021"  # scripted group (container) (typed FeaturePython)
  n = 1
  ref = N_element
FEATURE [App::DocumentObjectGroupPython] G4_N  # scripted group (container) (typed FeaturePython)
  Dunit = g/cm3
  Dvalue = 0.0011652
  Group = -> [N_element048]
  conduct = 2
  density = 1
  expand = 3
  formula = N
  name = G4_N
  specific = 4
FEATURE [App::DocumentObjectGroupPython] O_element105  label="O_element : 059"  # scripted group (container) (typed FeaturePython)
  n = 1
  ref = O_element
FEATURE [App::DocumentObjectGroupPython] G4_O  # scripted group (container) (typed FeaturePython)
  Dunit = g/cm3
  Dvalue = 0.00133151
  Group = -> [O_element105]
  conduct = 2
  density = 1
  expand = 3
  formula = O
  name = G4_O
  specific = 4
FEATURE [App::DocumentObjectGroupPython] F_element019  label="F_element : 008"  # scripted group (container) (typed FeaturePython)
  n = 1
  ref = F_element
FEATURE [App::DocumentObjectGroupPython] G4_F  # scripted group (container) (typed FeaturePython)
  Dunit = g/cm3
  Dvalue = 0.00158029
  Group = -> [F_element019]
  conduct = 2
  density = 1
  expand = 3
  formula = F
  name = G4_F
  specific = 4
FEATURE [App::DocumentObjectGroupPython] Ne_element001  label="Ne_element : 1"  # scripted group (container) (typed FeaturePython)
  n = 1
  ref = Ne_element
FEATURE [App::DocumentObjectGroupPython] G4_Ne  # scripted group (container) (typed FeaturePython)
  Dunit = g/cm3
  Dvalue = 0.000838505
  Group = -> [Ne_element001]
  conduct = 2
  density = 1
  expand = 3
  formula = Ne
  name = G4_Ne
  specific = 4
FEATURE [App::DocumentObjectGroupPython] Na_element020  label="Na_element : 005"  # scripted group (container) (typed FeaturePython)
  n = 1
  ref = Na_element
FEATURE [App::DocumentObjectGroupPython] G4_Na  # scripted group (container) (typed FeaturePython)
  Dunit = g/cm3
  Dvalue = 0.971
  Group = -> [Na_element020]
  conduct = 2
  density = 1
  expand = 3
  formula = Na
  name = G4_Na
  specific = 4
FEATURE [App::DocumentObjectGroupPython] Mg_element011  label="Mg_element : 005"  # scripted group (container) (typed FeaturePython)
  n = 1
  ref = Mg_element
FEATURE [App::DocumentObjectGroupPython] G4_Mg  # scripted group (container) (typed FeaturePython)
  Dunit = g/cm3
  Dvalue = 1.74
  Group = -> [Mg_element011]
  conduct = 2
  density = 1
  expand = 3
  formula = Mg
  name = G4_Mg
  specific = 4
FEATURE [App::DocumentObjectGroupPython] Al_element004  label="Al_element : 1"  # scripted group (container) (typed FeaturePython)
  n = 1
  ref = Al_element
FEATURE [App::DocumentObjectGroupPython] G4_Al  # scripted group (container) (typed FeaturePython)
  Dunit = g/cm3
  Dvalue = 2.699
  Group = -> [Al_element004]
  conduct = 2
  density = 1
  expand = 3
  formula = Al
  name = G4_Al
  specific = 4
FEATURE [App::DocumentObjectGroupPython] Si_element007  label="Si_element : 002"  # scripted group (container) (typed FeaturePython)
  n = 1
  ref = Si_element
FEATURE [App::DocumentObjectGroupPython] G4_Si  # scripted group (container) (typed FeaturePython)
  Dunit = g/cm3
  Dvalue = 2.33
  Group = -> [Si_element007]
  conduct = 2
  density = 1
  expand = 3
  formula = Si
  name = G4_Si
  specific = 4
FEATURE [App::DocumentObjectGroupPython] P_element013  label="P_element : 002"  # scripted group (container) (typed FeaturePython)
  n = 1
  ref = P_element
FEATURE [App::DocumentObjectGroupPython] G4_P  # scripted group (container) (typed FeaturePython)
  Dunit = g/cm3
  Dvalue = 2.2
  Group = -> [P_element013]
  conduct = 2
  density = 1
  expand = 3
  formula = P
  name = G4_P
  specific = 4
FEATURE [App::DocumentObjectGroupPython] S_element023  label="S_element : 007"  # scripted group (container) (typed FeaturePython)
  n = 1
  ref = S_element
FEATURE [App::DocumentObjectGroupPython] G4_S  # scripted group (container) (typed FeaturePython)
  Dunit = g/cm3
  Dvalue = 2
  Group = -> [S_element023]
  conduct = 2
  density = 1
  expand = 3
  formula = S
  name = G4_S
  specific = 4
FEATURE [App::DocumentObjectGroupPython] Cl_element029  label="Cl_element : 015"  # scripted group (container) (typed FeaturePython)
  n = 1
  ref = Cl_element
FEATURE [App::DocumentObjectGroupPython] G4_Cl  # scripted group (container) (typed FeaturePython)
  Dunit = g/cm3
  Dvalue = 0.00299473
  Group = -> [Cl_element029]
  conduct = 2
  density = 1
  expand = 3
  formula = Cl
  name = G4_Cl
  specific = 4
FEATURE [App::DocumentObjectGroupPython] Ar_element002  label="Ar_element : 1"  # scripted group (container) (typed FeaturePython)
  n = 1
  ref = Ar_element
FEATURE [App::DocumentObjectGroupPython] G4_Ar  # scripted group (container) (typed FeaturePython)
  Dunit = g/cm3
  Dvalue = 0.00166201
  Group = -> [Ar_element002]
  conduct = 2
  density = 1
  expand = 3
  formula = Ar
  name = G4_Ar
  specific = 4
FEATURE [App::DocumentObjectGroupPython] K_element013  label="K_element : 003"  # scripted group (container) (typed FeaturePython)
  n = 1
  ref = K_element
FEATURE [App::DocumentObjectGroupPython] G4_K  # scripted group (container) (typed FeaturePython)
  Dunit = g/cm3
  Dvalue = 0.862
  Group = -> [K_element013]
  conduct = 2
  density = 1
  expand = 3
  formula = K
  name = G4_K
  specific = 4
FEATURE [App::DocumentObjectGroupPython] Ca_element014  label="Ca_element : 007"  # scripted group (container) (typed FeaturePython)
  n = 1
  ref = Ca_element
FEATURE [App::DocumentObjectGroupPython] G4_Ca  # scripted group (container) (typed FeaturePython)
  Dunit = g/cm3
  Dvalue = 1.55
  Group = -> [Ca_element014]
  conduct = 2
  density = 1
  expand = 3
  formula = Ca
  name = G4_Ca
  specific = 4
FEATURE [App::DocumentObjectGroupPython] Sc_element001  label="Sc_element : 1"  # scripted group (container) (typed FeaturePython)
  n = 1
  ref = Sc_element
FEATURE [App::DocumentObjectGroupPython] G4_Sc  # scripted group (container) (typed FeaturePython)
  Dunit = g/cm3
  Dvalue = 2.989
  Group = -> [Sc_element001]
  conduct = 2
  density = 1
  expand = 3
  formula = Sc
  name = G4_Sc
  specific = 4
FEATURE [App::DocumentObjectGroupPython] Ti_element004  label="Ti_element : 002"  # scripted group (container) (typed FeaturePython)
  n = 1
  ref = Ti_element
FEATURE [App::DocumentObjectGroupPython] G4_Ti  # scripted group (container) (typed FeaturePython)
  Dunit = g/cm3
  Dvalue = 4.54
  Group = -> [Ti_element004]
  conduct = 2
  density = 1
  expand = 3
  formula = Ti
  name = G4_Ti
  specific = 4
FEATURE [App::DocumentObjectGroupPython] V_element001  label="V_element : 1"  # scripted group (container) (typed FeaturePython)
  n = 1
  ref = V_element
FEATURE [App::DocumentObjectGroupPython] G4_V  # scripted group (container) (typed FeaturePython)
  Dunit = g/cm3
  Dvalue = 6.11
  Group = -> [V_element001]
  conduct = 2
  density = 1
  expand = 3
  formula = V
  name = G4_V
  specific = 4
FEATURE [App::DocumentObjectGroupPython] Cr_element001  label="Cr_element : 1"  # scripted group (container) (typed FeaturePython)
  n = 1
  ref = Cr_element
FEATURE [App::DocumentObjectGroupPython] G4_Cr  # scripted group (container) (typed FeaturePython)
  Dunit = g/cm3
  Dvalue = 7.18
  Group = -> [Cr_element001]
  conduct = 2
  density = 1
  expand = 3
  formula = Cr
  name = G4_Cr
  specific = 4
FEATURE [App::DocumentObjectGroupPython] Mn_element001  label="Mn_element : 1"  # scripted group (container) (typed FeaturePython)
  n = 1
  ref = Mn_element
FEATURE [App::DocumentObjectGroupPython] G4_Mn  # scripted group (container) (typed FeaturePython)
  Dunit = g/cm3
  Dvalue = 7.44
  Group = -> [Mn_element001]
  conduct = 2
  density = 1
  expand = 3
  formula = Mn
  name = G4_Mn
  specific = 4
FEATURE [App::DocumentObjectGroupPython] Fe_element007  label="Fe_element : 004"  # scripted group (container) (typed FeaturePython)
  n = 1
  ref = Fe_element
FEATURE [App::DocumentObjectGroupPython] G4_Fe  # scripted group (container) (typed FeaturePython)
  Dunit = g/cm3
  Dvalue = 7.874
  Group = -> [Fe_element007]
  conduct = 2
  density = 1
  expand = 3
  formula = Fe
  name = G4_Fe
  specific = 4
FEATURE [App::DocumentObjectGroupPython] Co_element001  label="Co_element : 1"  # scripted group (container) (typed FeaturePython)
  n = 1
  ref = Co_element
FEATURE [App::DocumentObjectGroupPython] G4_Co  # scripted group (container) (typed FeaturePython)
  Dunit = g/cm3
  Dvalue = 8.9
  Group = -> [Co_element001]
  conduct = 2
  density = 1
  expand = 3
  formula = Co
  name = G4_Co
  specific = 4
FEATURE [App::DocumentObjectGroupPython] Ni_element001  label="Ni_element : 1"  # scripted group (container) (typed FeaturePython)
  n = 1
  ref = Ni_element
FEATURE [App::DocumentObjectGroupPython] G4_Ni  # scripted group (container) (typed FeaturePython)
  Dunit = g/cm3
  Dvalue = 8.902
  Group = -> [Ni_element001]
  conduct = 2
  density = 1
  expand = 3
  formula = Ni
  name = G4_Ni
  specific = 4
FEATURE [App::DocumentObjectGroupPython] Cu_element001  label="Cu_element : 1"  # scripted group (container) (typed FeaturePython)
  n = 1
  ref = Cu_element
FEATURE [App::DocumentObjectGroupPython] G4_Cu  # scripted group (container) (typed FeaturePython)
  Dunit = g/cm3
  Dvalue = 8.96
  Group = -> [Cu_element001]
  conduct = 2
  density = 1
  expand = 3
  formula = Cu
  name = G4_Cu
  specific = 4
FEATURE [App::DocumentObjectGroupPython] Zn_element001  label="Zn_element : 1"  # scripted group (container) (typed FeaturePython)
  n = 1
  ref = Zn_element
FEATURE [App::DocumentObjectGroupPython] G4_Zn  # scripted group (container) (typed FeaturePython)
  Dunit = g/cm3
  Dvalue = 7.133
  Group = -> [Zn_element001]
  conduct = 2
  density = 1
  expand = 3
  formula = Zn
  name = G4_Zn
  specific = 4
FEATURE [App::DocumentObjectGroupPython] Ga_element002  label="Ga_element : 002"  # scripted group (container) (typed FeaturePython)
  n = 1
  ref = Ga_element
FEATURE [App::DocumentObjectGroupPython] G4_Ga  # scripted group (container) (typed FeaturePython)
  Dunit = g/cm3
  Dvalue = 5.904
  Group = -> [Ga_element002]
  conduct = 2
  density = 1
  expand = 3
  formula = Ga
  name = G4_Ga
  specific = 4
FEATURE [App::DocumentObjectGroupPython] Ge_element002  label="Ge_element : 1"  # scripted group (container) (typed FeaturePython)
  n = 1
  ref = Ge_element
FEATURE [App::DocumentObjectGroupPython] G4_Ge  # scripted group (container) (typed FeaturePython)
  Dunit = g/cm3
  Dvalue = 5.323
  Group = -> [Ge_element002]
  conduct = 2
  density = 1
  expand = 3
  formula = Ge
  name = G4_Ge
  specific = 4
FEATURE [App::DocumentObjectGroupPython] As_element003  label="As_element : 002"  # scripted group (container) (typed FeaturePython)
  n = 1
  ref = As_element
FEATURE [App::DocumentObjectGroupPython] G4_As  # scripted group (container) (typed FeaturePython)
  Dunit = g/cm3
  Dvalue = 5.73
  Group = -> [As_element003]
  conduct = 2
  density = 1
  expand = 3
  formula = As
  name = G4_As
  specific = 4
FEATURE [App::DocumentObjectGroupPython] Se_element001  label="Se_element : 1"  # scripted group (container) (typed FeaturePython)
  n = 1
  ref = Se_element
FEATURE [App::DocumentObjectGroupPython] G4_Se  # scripted group (container) (typed FeaturePython)
  Dunit = g/cm3
  Dvalue = 4.5
  Group = -> [Se_element001]
  conduct = 2
  density = 1
  expand = 3
  formula = Se
  name = G4_Se
  specific = 4
FEATURE [App::DocumentObjectGroupPython] Br_element007  label="Br_element : 004"  # scripted group (container) (typed FeaturePython)
  n = 1
  ref = Br_element
FEATURE [App::DocumentObjectGroupPython] G4_Br  # scripted group (container) (typed FeaturePython)
  Dunit = g/cm3
  Dvalue = 0.0070721
  Group = -> [Br_element007]
  conduct = 2
  density = 1
  expand = 3
  formula = Br
  name = G4_Br
  specific = 4
FEATURE [App::DocumentObjectGroupPython] Kr_element001  label="Kr_element : 1"  # scripted group (container) (typed FeaturePython)
  n = 1
  ref = Kr_element
FEATURE [App::DocumentObjectGroupPython] G4_Kr  # scripted group (container) (typed FeaturePython)
  Dunit = g/cm3
  Dvalue = 0.00347832
  Group = -> [Kr_element001]
  conduct = 2
  density = 1
  expand = 3
  formula = Kr
  name = G4_Kr
  specific = 4
FEATURE [App::DocumentObjectGroupPython] Rb_element001  label="Rb_element : 1"  # scripted group (container) (typed FeaturePython)
  n = 1
  ref = Rb_element
FEATURE [App::DocumentObjectGroupPython] G4_Rb  # scripted group (container) (typed FeaturePython)
  Dunit = g/cm3
  Dvalue = 1.532
  Group = -> [Rb_element001]
  conduct = 2
  density = 1
  expand = 3
  formula = Rb
  name = G4_Rb
  specific = 4
FEATURE [App::DocumentObjectGroupPython] Sr_element001  label="Sr_element : 1"  # scripted group (container) (typed FeaturePython)
  n = 1
  ref = Sr_element
FEATURE [App::DocumentObjectGroupPython] G4_Sr  # scripted group (container) (typed FeaturePython)
  Dunit = g/cm3
  Dvalue = 2.54
  Group = -> [Sr_element001]
  conduct = 2
  density = 1
  expand = 3
  formula = Sr
  name = G4_Sr
  specific = 4
FEATURE [App::DocumentObjectGroupPython] Y_element001  label="Y_element : 1"  # scripted group (container) (typed FeaturePython)
  n = 1
  ref = Y_element
FEATURE [App::DocumentObjectGroupPython] G4_Y  # scripted group (container) (typed FeaturePython)
  Dunit = g/cm3
  Dvalue = 4.469
  Group = -> [Y_element001]
  conduct = 2
  density = 1
  expand = 3
  formula = Y
  name = G4_Y
  specific = 4
FEATURE [App::DocumentObjectGroupPython] Zr_element001  label="Zr_element : 1"  # scripted group (container) (typed FeaturePython)
  n = 1
  ref = Zr_element
FEATURE [App::DocumentObjectGroupPython] G4_Zr  # scripted group (container) (typed FeaturePython)
  Dunit = g/cm3
  Dvalue = 6.506
  Group = -> [Zr_element001]
  conduct = 2
  density = 1
  expand = 3
  formula = Zr
  name = G4_Zr
  specific = 4
FEATURE [App::DocumentObjectGroupPython] Nb_element001  label="Nb_element : 1"  # scripted group (container) (typed FeaturePython)
  n = 1
  ref = Nb_element
FEATURE [App::DocumentObjectGroupPython] G4_Nb  # scripted group (container) (typed FeaturePython)
  Dunit = g/cm3
  Dvalue = 8.57
  Group = -> [Nb_element001]
  conduct = 2
  density = 1
  expand = 3
  formula = Nb
  name = G4_Nb
  specific = 4
FEATURE [App::DocumentObjectGroupPython] Mo_element001  label="Mo_element : 1"  # scripted group (container) (typed FeaturePython)
  n = 1
  ref = Mo_element
FEATURE [App::DocumentObjectGroupPython] G4_Mo  # scripted group (container) (typed FeaturePython)
  Dunit = g/cm3
  Dvalue = 10.22
  Group = -> [Mo_element001]
  conduct = 2
  density = 1
  expand = 3
  formula = Mo
  name = G4_Mo
  specific = 4
FEATURE [App::DocumentObjectGroupPython] Tc_element001  label="Tc_element : 1"  # scripted group (container) (typed FeaturePython)
  n = 1
  ref = Tc_element
FEATURE [App::DocumentObjectGroupPython] G4_Tc  # scripted group (container) (typed FeaturePython)
  Dunit = g/cm3
  Dvalue = 11.5
  Group = -> [Tc_element001]
  conduct = 2
  density = 1
  expand = 3
  formula = Tc
  name = G4_Tc
  specific = 4
FEATURE [App::DocumentObjectGroupPython] Ru_element001  label="Ru_element : 1"  # scripted group (container) (typed FeaturePython)
  n = 1
  ref = Ru_element
FEATURE [App::DocumentObjectGroupPython] G4_Ru  # scripted group (container) (typed FeaturePython)
  Dunit = g/cm3
  Dvalue = 12.41
  Group = -> [Ru_element001]
  conduct = 2
  density = 1
  expand = 3
  formula = Ru
  name = G4_Ru
  specific = 4
FEATURE [App::DocumentObjectGroupPython] Rh_element001  label="Rh_element : 1"  # scripted group (container) (typed FeaturePython)
  n = 1
  ref = Rh_element
FEATURE [App::DocumentObjectGroupPython] G4_Rh  # scripted group (container) (typed FeaturePython)
  Dunit = g/cm3
  Dvalue = 12.41
  Group = -> [Rh_element001]
  conduct = 2
  density = 1
  expand = 3
  formula = Rh
  name = G4_Rh
  specific = 4
FEATURE [App::DocumentObjectGroupPython] Pd_element001  label="Pd_element : 1"  # scripted group (container) (typed FeaturePython)
  n = 1
  ref = Pd_element
FEATURE [App::DocumentObjectGroupPython] G4_Pd  # scripted group (container) (typed FeaturePython)
  Dunit = g/cm3
  Dvalue = 12.02
  Group = -> [Pd_element001]
  conduct = 2
  density = 1
  expand = 3
  formula = Pd
  name = G4_Pd
  specific = 4
FEATURE [App::DocumentObjectGroupPython] Ag_element006  label="Ag_element : 004"  # scripted group (container) (typed FeaturePython)
  n = 1
  ref = Ag_element
FEATURE [App::DocumentObjectGroupPython] G4_Ag  # scripted group (container) (typed FeaturePython)
  Dunit = g/cm3
  Dvalue = 10.5
  Group = -> [Ag_element006]
  conduct = 2
  density = 1
  expand = 3
  formula = Ag
  name = G4_Ag
  specific = 4
FEATURE [App::DocumentObjectGroupPython] Cd_element003  label="Cd_element : 003"  # scripted group (container) (typed FeaturePython)
  n = 1
  ref = Cd_element
FEATURE [App::DocumentObjectGroupPython] G4_Cd  # scripted group (container) (typed FeaturePython)
  Dunit = g/cm3
  Dvalue = 8.65
  Group = -> [Cd_element003]
  conduct = 2
  density = 1
  expand = 3
  formula = Cd
  name = G4_Cd
  specific = 4
FEATURE [App::DocumentObjectGroupPython] In_element001  label="In_element : 1"  # scripted group (container) (typed FeaturePython)
  n = 1
  ref = In_element
FEATURE [App::DocumentObjectGroupPython] G4_In  # scripted group (container) (typed FeaturePython)
  Dunit = g/cm3
  Dvalue = 7.31
  Group = -> [In_element001]
  conduct = 2
  density = 1
  expand = 3
  formula = In
  name = G4_In
  specific = 4
FEATURE [App::DocumentObjectGroupPython] Sn_element001  label="Sn_element : 1"  # scripted group (container) (typed FeaturePython)
  n = 1
  ref = Sn_element
FEATURE [App::DocumentObjectGroupPython] G4_Sn  # scripted group (container) (typed FeaturePython)
  Dunit = g/cm3
  Dvalue = 7.31
  Group = -> [Sn_element001]
  conduct = 2
  density = 1
  expand = 3
  formula = Sn
  name = G4_Sn
  specific = 4
FEATURE [App::DocumentObjectGroupPython] Sb_element001  label="Sb_element : 1"  # scripted group (container) (typed FeaturePython)
  n = 1
  ref = Sb_element
FEATURE [App::DocumentObjectGroupPython] G4_Sb  # scripted group (container) (typed FeaturePython)
  Dunit = g/cm3
  Dvalue = 6.691
  Group = -> [Sb_element001]
  conduct = 2
  density = 1
  expand = 3
  formula = Sb
  name = G4_Sb
  specific = 4
FEATURE [App::DocumentObjectGroupPython] Te_element002  label="Te_element : 002"  # scripted group (container) (typed FeaturePython)
  n = 1
  ref = Te_element
FEATURE [App::DocumentObjectGroupPython] G4_Te  # scripted group (container) (typed FeaturePython)
  Dunit = g/cm3
  Dvalue = 6.24
  Group = -> [Te_element002]
  conduct = 2
  density = 1
  expand = 3
  formula = Te
  name = G4_Te
  specific = 4
FEATURE [App::DocumentObjectGroupPython] I_element010  label="I_element : 006"  # scripted group (container) (typed FeaturePython)
  n = 1
  ref = I_element
FEATURE [App::DocumentObjectGroupPython] G4_I  # scripted group (container) (typed FeaturePython)
  Dunit = g/cm3
  Dvalue = 4.93
  Group = -> [I_element010]
  conduct = 2
  density = 1
  expand = 3
  formula = I
  name = G4_I
  specific = 4
FEATURE [App::DocumentObjectGroupPython] Xe_element001  label="Xe_element : 1"  # scripted group (container) (typed FeaturePython)
  n = 1
  ref = Xe_element
FEATURE [App::DocumentObjectGroupPython] G4_Xe  # scripted group (container) (typed FeaturePython)
  Dunit = g/cm3
  Dvalue = 0.00548536
  Group = -> [Xe_element001]
  conduct = 2
  density = 1
  expand = 3
  formula = Xe
  name = G4_Xe
  specific = 4
FEATURE [App::DocumentObjectGroupPython] Cs_element003  label="Cs_element : 003"  # scripted group (container) (typed FeaturePython)
  n = 1
  ref = Cs_element
FEATURE [App::DocumentObjectGroupPython] G4_Cs  # scripted group (container) (typed FeaturePython)
  Dunit = g/cm3
  Dvalue = 1.873
  Group = -> [Cs_element003]
  conduct = 2
  density = 1
  expand = 3
  formula = Cs
  name = G4_Cs
  specific = 4
FEATURE [App::DocumentObjectGroupPython] Ba_element003  label="Ba_element : 003"  # scripted group (container) (typed FeaturePython)
  n = 1
  ref = Ba_element
FEATURE [App::DocumentObjectGroupPython] G4_Ba  # scripted group (container) (typed FeaturePython)
  Dunit = g/cm3
  Dvalue = 3.5
  Group = -> [Ba_element003]
  conduct = 2
  density = 1
  expand = 3
  formula = Ba
  name = G4_Ba
  specific = 4
FEATURE [App::DocumentObjectGroupPython] La_element003  label="La_element : 003"  # scripted group (container) (typed FeaturePython)
  n = 1
  ref = La_element
FEATURE [App::DocumentObjectGroupPython] G4_La  # scripted group (container) (typed FeaturePython)
  Dunit = g/cm3
  Dvalue = 6.154
  Group = -> [La_element003]
  conduct = 2
  density = 1
  expand = 3
  formula = La
  name = G4_La
  specific = 4
FEATURE [App::DocumentObjectGroupPython] Ce_element002  label="Ce_element : 1"  # scripted group (container) (typed FeaturePython)
  n = 1
  ref = Ce_element
FEATURE [App::DocumentObjectGroupPython] G4_Ce  # scripted group (container) (typed FeaturePython)
  Dunit = g/cm3
  Dvalue = 6.657
  Group = -> [Ce_element002]
  conduct = 2
  density = 1
  expand = 3
  formula = Ce
  name = G4_Ce
  specific = 4
FEATURE [App::DocumentObjectGroupPython] Pr_element001  label="Pr_element : 1"  # scripted group (container) (typed FeaturePython)
  n = 1
  ref = Pr_element
FEATURE [App::DocumentObjectGroupPython] G4_Pr  # scripted group (container) (typed FeaturePython)
  Dunit = g/cm3
  Dvalue = 6.71
  Group = -> [Pr_element001]
  conduct = 2
  density = 1
  expand = 3
  formula = Pr
  name = G4_Pr
  specific = 4
FEATURE [App::DocumentObjectGroupPython] Nd_element001  label="Nd_element : 1"  # scripted group (container) (typed FeaturePython)
  n = 1
  ref = Nd_element
FEATURE [App::DocumentObjectGroupPython] G4_Nd  # scripted group (container) (typed FeaturePython)
  Dunit = g/cm3
  Dvalue = 6.9
  Group = -> [Nd_element001]
  conduct = 2
  density = 1
  expand = 3
  formula = Nd
  name = G4_Nd
  specific = 4
FEATURE [App::DocumentObjectGroupPython] Pm_element001  label="Pm_element : 1"  # scripted group (container) (typed FeaturePython)
  n = 1
  ref = Pm_element
FEATURE [App::DocumentObjectGroupPython] G4_Pm  # scripted group (container) (typed FeaturePython)
  Dunit = g/cm3
  Dvalue = 7.22
  Group = -> [Pm_element001]
  conduct = 2
  density = 1
  expand = 3
  formula = Pm
  name = G4_Pm
  specific = 4
FEATURE [App::DocumentObjectGroupPython] Sm_element001  label="Sm_element : 1"  # scripted group (container) (typed FeaturePython)
  n = 1
  ref = Sm_element
FEATURE [App::DocumentObjectGroupPython] G4_Sm  # scripted group (container) (typed FeaturePython)
  Dunit = g/cm3
  Dvalue = 7.46
  Group = -> [Sm_element001]
  conduct = 2
  density = 1
  expand = 3
  formula = Sm
  name = G4_Sm
  specific = 4
FEATURE [App::DocumentObjectGroupPython] Eu_element001  label="Eu_element : 1"  # scripted group (container) (typed FeaturePython)
  n = 1
  ref = Eu_element
FEATURE [App::DocumentObjectGroupPython] G4_Eu  # scripted group (container) (typed FeaturePython)
  Dunit = g/cm3
  Dvalue = 5.243
  Group = -> [Eu_element001]
  conduct = 2
  density = 1
  expand = 3
  formula = Eu
  name = G4_Eu
  specific = 4
FEATURE [App::DocumentObjectGroupPython] Gd_element002  label="Gd_element : 1"  # scripted group (container) (typed FeaturePython)
  n = 1
  ref = Gd_element
FEATURE [App::DocumentObjectGroupPython] G4_Gd  # scripted group (container) (typed FeaturePython)
  Dunit = g/cm3
  Dvalue = 7.9004
  Group = -> [Gd_element002]
  conduct = 2
  density = 1
  expand = 3
  formula = Gd
  name = G4_Gd
  specific = 4
FEATURE [App::DocumentObjectGroupPython] Tb_element001  label="Tb_element : 1"  # scripted group (container) (typed FeaturePython)
  n = 1
  ref = Tb_element
FEATURE [App::DocumentObjectGroupPython] G4_Tb  # scripted group (container) (typed FeaturePython)
  Dunit = g/cm3
  Dvalue = 8.229
  Group = -> [Tb_element001]
  conduct = 2
  density = 1
  expand = 3
  formula = Tb
  name = G4_Tb
  specific = 4
FEATURE [App::DocumentObjectGroupPython] Dy_element001  label="Dy_element : 1"  # scripted group (container) (typed FeaturePython)
  n = 1
  ref = Dy_element
FEATURE [App::DocumentObjectGroupPython] G4_Dy  # scripted group (container) (typed FeaturePython)
  Dunit = g/cm3
  Dvalue = 8.55
  Group = -> [Dy_element001]
  conduct = 2
  density = 1
  expand = 3
  formula = Dy
  name = G4_Dy
  specific = 4
FEATURE [App::DocumentObjectGroupPython] Ho_element001  label="Ho_element : 1"  # scripted group (container) (typed FeaturePython)
  n = 1
  ref = Ho_element
FEATURE [App::DocumentObjectGroupPython] G4_Ho  # scripted group (container) (typed FeaturePython)
  Dunit = g/cm3
  Dvalue = 8.795
  Group = -> [Ho_element001]
  conduct = 2
  density = 1
  expand = 3
  formula = Ho
  name = G4_Ho
  specific = 4
FEATURE [App::DocumentObjectGroupPython] Er_element001  label="Er_element : 1"  # scripted group (container) (typed FeaturePython)
  n = 1
  ref = Er_element
FEATURE [App::DocumentObjectGroupPython] G4_Er  # scripted group (container) (typed FeaturePython)
  Dunit = g/cm3
  Dvalue = 9.066
  Group = -> [Er_element001]
  conduct = 2
  density = 1
  expand = 3
  formula = Er
  name = G4_Er
  specific = 4
FEATURE [App::DocumentObjectGroupPython] Tm_element001  label="Tm_element : 1"  # scripted group (container) (typed FeaturePython)
  n = 1
  ref = Tm_element
FEATURE [App::DocumentObjectGroupPython] G4_Tm  # scripted group (container) (typed FeaturePython)
  Dunit = g/cm3
  Dvalue = 9.321
  Group = -> [Tm_element001]
  conduct = 2
  density = 1
  expand = 3
  formula = Tm
  name = G4_Tm
  specific = 4
FEATURE [App::DocumentObjectGroupPython] Yb_element001  label="Yb_element : 1"  # scripted group (container) (typed FeaturePython)
  n = 1
  ref = Yb_element
FEATURE [App::DocumentObjectGroupPython] G4_Yb  # scripted group (container) (typed FeaturePython)
  Dunit = g/cm3
  Dvalue = 6.73
  Group = -> [Yb_element001]
  conduct = 2
  density = 1
  expand = 3
  formula = Yb
  name = G4_Yb
  specific = 4
FEATURE [App::DocumentObjectGroupPython] Lu_element001  label="Lu_element : 1"  # scripted group (container) (typed FeaturePython)
  n = 1
  ref = Lu_element
FEATURE [App::DocumentObjectGroupPython] G4_Lu  # scripted group (container) (typed FeaturePython)
  Dunit = g/cm3
  Dvalue = 9.84
  Group = -> [Lu_element001]
  conduct = 2
  density = 1
  expand = 3
  formula = Lu
  name = G4_Lu
  specific = 4
FEATURE [App::DocumentObjectGroupPython] Hf_element001  label="Hf_element : 1"  # scripted group (container) (typed FeaturePython)
  n = 1
  ref = Hf_element
FEATURE [App::DocumentObjectGroupPython] G4_Hf  # scripted group (container) (typed FeaturePython)
  Dunit = g/cm3
  Dvalue = 13.31
  Group = -> [Hf_element001]
  conduct = 2
  density = 1
  expand = 3
  formula = Hf
  name = G4_Hf
  specific = 4
FEATURE [App::DocumentObjectGroupPython] Ta_element001  label="Ta_element : 1"  # scripted group (container) (typed FeaturePython)
  n = 1
  ref = Ta_element
FEATURE [App::DocumentObjectGroupPython] G4_Ta  # scripted group (container) (typed FeaturePython)
  Dunit = g/cm3
  Dvalue = 16.654
  Group = -> [Ta_element001]
  conduct = 2
  density = 1
  expand = 3
  formula = Ta
  name = G4_Ta
  specific = 4
FEATURE [App::DocumentObjectGroupPython] W_element004  label="W_element : 004"  # scripted group (container) (typed FeaturePython)
  n = 1
  ref = W_element
FEATURE [App::DocumentObjectGroupPython] G4_W  # scripted group (container) (typed FeaturePython)
  Dunit = g/cm3
  Dvalue = 19.3
  Group = -> [W_element004]
  conduct = 2
  density = 1
  expand = 3
  formula = W
  name = G4_W
  specific = 4
FEATURE [App::DocumentObjectGroupPython] Re_element001  label="Re_element : 1"  # scripted group (container) (typed FeaturePython)
  n = 1
  ref = Re_element
FEATURE [App::DocumentObjectGroupPython] G4_Re  # scripted group (container) (typed FeaturePython)
  Dunit = g/cm3
  Dvalue = 21.02
  Group = -> [Re_element001]
  conduct = 2
  density = 1
  expand = 3
  formula = Re
  name = G4_Re
  specific = 4
FEATURE [App::DocumentObjectGroupPython] Os_element001  label="Os_element : 1"  # scripted group (container) (typed FeaturePython)
  n = 1
  ref = Os_element
FEATURE [App::DocumentObjectGroupPython] G4_Os  # scripted group (container) (typed FeaturePython)
  Dunit = g/cm3
  Dvalue = 22.57
  Group = -> [Os_element001]
  conduct = 2
  density = 1
  expand = 3
  formula = Os
  name = G4_Os
  specific = 4
FEATURE [App::DocumentObjectGroupPython] Ir_element001  label="Ir_element : 1"  # scripted group (container) (typed FeaturePython)
  n = 1
  ref = Ir_element
FEATURE [App::DocumentObjectGroupPython] G4_Ir  # scripted group (container) (typed FeaturePython)
  Dunit = g/cm3
  Dvalue = 22.42
  Group = -> [Ir_element001]
  conduct = 2
  density = 1
  expand = 3
  formula = Ir
  name = G4_Ir
  specific = 4
FEATURE [App::DocumentObjectGroupPython] Pt_element001  label="Pt_element : 1"  # scripted group (container) (typed FeaturePython)
  n = 1
  ref = Pt_element
FEATURE [App::DocumentObjectGroupPython] G4_Pt  # scripted group (container) (typed FeaturePython)
  Dunit = g/cm3
  Dvalue = 21.45
  Group = -> [Pt_element001]
  conduct = 2
  density = 1
  expand = 3
  formula = Pt
  name = G4_Pt
  specific = 4
FEATURE [App::DocumentObjectGroupPython] Au_element001  label="Au_element : 1"  # scripted group (container) (typed FeaturePython)
  n = 1
  ref = Au_element
FEATURE [App::DocumentObjectGroupPython] G4_Au  # scripted group (container) (typed FeaturePython)
  Dunit = g/cm3
  Dvalue = 19.32
  Group = -> [Au_element001]
  conduct = 2
  density = 1
  expand = 3
  formula = Au
  name = G4_Au
  specific = 4
FEATURE [App::DocumentObjectGroupPython] Hg_element002  label="Hg_element : 002"  # scripted group (container) (typed FeaturePython)
  n = 1
  ref = Hg_element
FEATURE [App::DocumentObjectGroupPython] G4_Hg  # scripted group (container) (typed FeaturePython)
  Dunit = g/cm3
  Dvalue = 13.546
  Group = -> [Hg_element002]
  conduct = 2
  density = 1
  expand = 3
  formula = Hg
  name = G4_Hg
  specific = 4
FEATURE [App::DocumentObjectGroupPython] Tl_element002  label="Tl_element : 002"  # scripted group (container) (typed FeaturePython)
  n = 1
  ref = Tl_element
FEATURE [App::DocumentObjectGroupPython] G4_Tl  # scripted group (container) (typed FeaturePython)
  Dunit = g/cm3
  Dvalue = 11.72
  Group = -> [Tl_element002]
  conduct = 2
  density = 1
  expand = 3
  formula = Tl
  name = G4_Tl
  specific = 4
FEATURE [App::DocumentObjectGroupPython] Pb_element003  label="Pb_element : 1"  # scripted group (container) (typed FeaturePython)
  n = 1
  ref = Pb_element
FEATURE [App::DocumentObjectGroupPython] G4_Pb  # scripted group (container) (typed FeaturePython)
  Dunit = g/cm3
  Dvalue = 11.35
  Group = -> [Pb_element003]
  conduct = 2
  density = 1
  expand = 3
  formula = Pb
  name = G4_Pb
  specific = 4
FEATURE [App::DocumentObjectGroupPython] Bi_element002  label="Bi_element : 1"  # scripted group (container) (typed FeaturePython)
  n = 1
  ref = Bi_element
FEATURE [App::DocumentObjectGroupPython] G4_Bi  # scripted group (container) (typed FeaturePython)
  Dunit = g/cm3
  Dvalue = 9.747
  Group = -> [Bi_element002]
  conduct = 2
  density = 1
  expand = 3
  formula = Bi
  name = G4_Bi
  specific = 4
FEATURE [App::DocumentObjectGroupPython] Po_element001  label="Po_element : 1"  # scripted group (container) (typed FeaturePython)
  n = 1
  ref = Po_element
FEATURE [App::DocumentObjectGroupPython] G4_Po  # scripted group (container) (typed FeaturePython)
  Dunit = g/cm3
  Dvalue = 9.32
  Group = -> [Po_element001]
  conduct = 2
  density = 1
  expand = 3
  formula = Po
  name = G4_Po
  specific = 4
FEATURE [App::DocumentObjectGroupPython] At_element001  label="At_element : 1"  # scripted group (container) (typed FeaturePython)
  n = 1
  ref = At_element
FEATURE [App::DocumentObjectGroupPython] G4_At  # scripted group (container) (typed FeaturePython)
  Dunit = g/cm3
  Dvalue = 9.32
  Group = -> [At_element001]
  conduct = 2
  density = 1
  expand = 3
  formula = At
  name = G4_At
  specific = 4
FEATURE [App::DocumentObjectGroupPython] Rn_element001  label="Rn_element : 1"  # scripted group (container) (typed FeaturePython)
  n = 1
  ref = Rn_element
FEATURE [App::DocumentObjectGroupPython] G4_Rn  # scripted group (container) (typed FeaturePython)
  Dunit = g/cm3
  Dvalue = 0.00900662
  Group = -> [Rn_element001]
  conduct = 2
  density = 1
  expand = 3
  formula = Rn
  name = G4_Rn
  specific = 4
FEATURE [App::DocumentObjectGroupPython] Fr_element001  label="Fr_element : 1"  # scripted group (container) (typed FeaturePython)
  n = 1
  ref = Fr_element
FEATURE [App::DocumentObjectGroupPython] G4_Fr  # scripted group (container) (typed FeaturePython)
  Dunit = g/cm3
  Dvalue = 1
  Group = -> [Fr_element001]
  conduct = 2
  density = 1
  expand = 3
  formula = Fr
  name = G4_Fr
  specific = 4
FEATURE [App::DocumentObjectGroupPython] Ra_element001  label="Ra_element : 1"  # scripted group (container) (typed FeaturePython)
  n = 1
  ref = Ra_element
FEATURE [App::DocumentObjectGroupPython] G4_Ra  # scripted group (container) (typed FeaturePython)
  Dunit = g/cm3
  Dvalue = 5
  Group = -> [Ra_element001]
  conduct = 2
  density = 1
  expand = 3
  formula = Ra
  name = G4_Ra
  specific = 4
FEATURE [App::DocumentObjectGroupPython] Ac_element001  label="Ac_element : 1"  # scripted group (container) (typed FeaturePython)
  n = 1
  ref = Ac_element
FEATURE [App::DocumentObjectGroupPython] G4_Ac  # scripted group (container) (typed FeaturePython)
  Dunit = g/cm3
  Dvalue = 10.07
  Group = -> [Ac_element001]
  conduct = 2
  density = 1
  expand = 3
  formula = Ac
  name = G4_Ac
  specific = 4
FEATURE [App::DocumentObjectGroupPython] Th_element001  label="Th_element : 1"  # scripted group (container) (typed FeaturePython)
  n = 1
  ref = Th_element
FEATURE [App::DocumentObjectGroupPython] G4_Th  # scripted group (container) (typed FeaturePython)
  Dunit = g/cm3
  Dvalue = 11.72
  Group = -> [Th_element001]
  conduct = 2
  density = 1
  expand = 3
  formula = Th
  name = G4_Th
  specific = 4
FEATURE [App::DocumentObjectGroupPython] Pa_element001  label="Pa_element : 1"  # scripted group (container) (typed FeaturePython)
  n = 1
  ref = Pa_element
FEATURE [App::DocumentObjectGroupPython] G4_Pa  # scripted group (container) (typed FeaturePython)
  Dunit = g/cm3
  Dvalue = 15.37
  Group = -> [Pa_element001]
  conduct = 2
  density = 1
  expand = 3
  formula = Pa
  name = G4_Pa
  specific = 4
FEATURE [App::DocumentObjectGroupPython] U_element004  label="U_element : 004"  # scripted group (container) (typed FeaturePython)
  n = 1
  ref = U_element
FEATURE [App::DocumentObjectGroupPython] G4_U  # scripted group (container) (typed FeaturePython)
  Dunit = g/cm3
  Dvalue = 18.95
  Group = -> [U_element004]
  conduct = 2
  density = 1
  expand = 3
  formula = U
  name = G4_U
  specific = 4
FEATURE [App::DocumentObjectGroupPython] Np_element001  label="Np_element : 1"  # scripted group (container) (typed FeaturePython)
  n = 1
  ref = Np_element
FEATURE [App::DocumentObjectGroupPython] G4_Np  # scripted group (container) (typed FeaturePython)
  Dunit = g/cm3
  Dvalue = 20.25
  Group = -> [Np_element001]
  conduct = 2
  density = 1
  expand = 3
  formula = Np
  name = G4_Np
  specific = 4
FEATURE [App::DocumentObjectGroupPython] Pu_element002  label="Pu_element : 002"  # scripted group (container) (typed FeaturePython)
  n = 1
  ref = Pu_element
FEATURE [App::DocumentObjectGroupPython] G4_Pu  # scripted group (container) (typed FeaturePython)
  Dunit = g/cm3
  Dvalue = 19.84
  Group = -> [Pu_element002]
  conduct = 2
  density = 1
  expand = 3
  formula = Pu
  name = G4_Pu
  specific = 4
FEATURE [App::DocumentObjectGroupPython] Am_element001  label="Am_element : 1"  # scripted group (container) (typed FeaturePython)
  n = 1
  ref = Am_element
FEATURE [App::DocumentObjectGroupPython] G4_Am  # scripted group (container) (typed FeaturePython)
  Dunit = g/cm3
  Dvalue = 13.67
  Group = -> [Am_element001]
  conduct = 2
  density = 1
  expand = 3
  formula = Am
  name = G4_Am
  specific = 4
FEATURE [App::DocumentObjectGroupPython] Cm_element001  label="Cm_element : 1"  # scripted group (container) (typed FeaturePython)
  n = 1
  ref = Cm_element
FEATURE [App::DocumentObjectGroupPython] G4_Cm  # scripted group (container) (typed FeaturePython)
  Dunit = g/cm3
  Dvalue = 13.51
  Group = -> [Cm_element001]
  conduct = 2
  density = 1
  expand = 3
  formula = Cm
  name = G4_Cm
  specific = 4
FEATURE [App::DocumentObjectGroupPython] Bk_element001  label="Bk_element : 1"  # scripted group (container) (typed FeaturePython)
  n = 1
  ref = Bk_element
FEATURE [App::DocumentObjectGroupPython] G4_Bk  # scripted group (container) (typed FeaturePython)
  Dunit = g/cm3
  Dvalue = 14
  Group = -> [Bk_element001]
  conduct = 2
  density = 1
  expand = 3
  formula = Bk
  name = G4_Bk
  specific = 4
FEATURE [App::DocumentObjectGroupPython] Cf_element001  label="Cf_element : 1"  # scripted group (container) (typed FeaturePython)
  n = 1
  ref = Cf_element
FEATURE [App::DocumentObjectGroupPython] G4_Cf  # scripted group (container) (typed FeaturePython)
  Dunit = g/cm3
  Dvalue = 10
  Group = -> [Cf_element001]
  conduct = 2
  density = 1
  expand = 3
  formula = Cf
  name = G4_Cf
  specific = 4
FEATURE [App::DocumentObjectGroupPython] Element  # scripted group (container) (typed FeaturePython)
  Group = -> [G4_H,G4_He,G4_Li,G4_Be,G4_B,G4_C,G4_N,G4_O,G4_F,G4_Ne,G4_Na,G4_Mg,G4_Al,G4_Si,G4_P,G4_S,G4_Cl,G4_Ar,G4_K,G4_Ca,G4_Sc,G4_Ti,G4_V,G4_Cr,G4_Mn,G4_Fe,G4_Co,G4_Ni,G4_Cu,G4_Zn,G4_Ga,G4_Ge,G4_As,G4_Se,G4_Br,G4_Kr,G4_Rb,G4_Sr,G4_Y,G4_Zr,G4_Nb,G4_Mo,G4_Tc,G4_Ru,G4_Rh,G4_Pd,G4_Ag,G4_Cd,G4_In,G4_Sn,G4_Sb,G4_Te,G4_I,G4_Xe,G4_Cs,G4_Ba,G4_La,G4_Ce,G4_Pr,G4_Nd,G4_Pm,G4_Sm,G4_Eu,G4_Gd,G4_Tb,G4_Dy,G4_Ho,G4_Er,+30 more]
FEATURE [App::DocumentObjectGroupPython] H_element114  label="H_element : 063"  # scripted group (container) (typed FeaturePython)
  n = 2
  ref = H_element
FEATURE [App::DocumentObjectGroupPython] G4_lH2  # scripted group (container) (typed FeaturePython)
  Dunit = g/cm3
  Dvalue = 0.0708
  Group = -> [H_element114]
  conduct = 2
  density = 1
  expand = 3
  formula = G4_lH2
  name = G4_lH2
  specific = 4
FEATURE [App::DocumentObjectGroupPython] N_element049  label="N_element : 022"  # scripted group (container) (typed FeaturePython)
  n = 2
  ref = N_element
FEATURE [App::DocumentObjectGroupPython] G4_lN2  # scripted group (container) (typed FeaturePython)
  Dunit = g/cm3
  Dvalue = 0.807
  Group = -> [N_element049]
  conduct = 2
  density = 1
  expand = 3
  formula = G4_lN2
  name = G4_lN2
  specific = 4
FEATURE [App::DocumentObjectGroupPython] O_element106  label="O_element : 060"  # scripted group (container) (typed FeaturePython)
  n = 2
  ref = O_element
FEATURE [App::DocumentObjectGroupPython] G4_lO2  # scripted group (container) (typed FeaturePython)
  Dunit = g/cm3
  Dvalue = 1.141
  Group = -> [O_element106]
  conduct = 2
  density = 1
  expand = 3
  formula = G4_lO2
  name = G4_lO2
  specific = 4
FEATURE [App::DocumentObjectGroupPython] Ar  label="Ar : 1"  # scripted group (container) (typed FeaturePython)
  n = 1
  ref = Ar
FEATURE [App::DocumentObjectGroupPython] G4_lAr  # scripted group (container) (typed FeaturePython)
  Dunit = g/cm3
  Dvalue = 1.396
  Group = -> [Ar]
  conduct = 2
  density = 1
  expand = 3
  formula = G4_lAr
  name = G4_lAr
  specific = 4
FEATURE [App::DocumentObjectGroupPython] Br  label="Br : 1"  # scripted group (container) (typed FeaturePython)
  n = 1
  ref = Br
FEATURE [App::DocumentObjectGroupPython] G4_lBr  # scripted group (container) (typed FeaturePython)
  Dunit = g/cm3
  Dvalue = 3.1028
  Group = -> [Br]
  conduct = 2
  density = 1
  expand = 3
  formula = G4_lBr
  name = G4_lBr
  specific = 4
FEATURE [App::DocumentObjectGroupPython] Kr  label="Kr : 1"  # scripted group (container) (typed FeaturePython)
  n = 1
  ref = Kr
FEATURE [App::DocumentObjectGroupPython] G4_lKr  # scripted group (container) (typed FeaturePython)
  Dunit = g/cm3
  Dvalue = 2.418
  Group = -> [Kr]
  conduct = 2
  density = 1
  expand = 3
  formula = G4_lKr
  name = G4_lKr
  specific = 4
FEATURE [App::DocumentObjectGroupPython] Xe  label="Xe : 1"  # scripted group (container) (typed FeaturePython)
  n = 1
  ref = Xe
FEATURE [App::DocumentObjectGroupPython] G4_lXe  # scripted group (container) (typed FeaturePython)
  Dunit = g/cm3
  Dvalue = 2.953
  Group = -> [Xe]
  conduct = 2
  density = 1
  expand = 3
  formula = G4_lXe
  name = G4_lXe
  specific = 4
FEATURE [App::DocumentObjectGroupPython] O_element107  label="O_element : 061"  # scripted group (container) (typed FeaturePython)
  n = 4
  ref = O_element
FEATURE [App::DocumentObjectGroupPython] Pb_element004  label="Pb_element : 002"  # scripted group (container) (typed FeaturePython)
  n = 1
  ref = Pb_element
FEATURE [App::DocumentObjectGroupPython] W_element005  label="W_element : 005"  # scripted group (container) (typed FeaturePython)
  n = 1
  ref = W_element
FEATURE [App::DocumentObjectGroupPython] G4_PbWO4  # scripted group (container) (typed FeaturePython)
  Dunit = g/cm3
  Dvalue = 8.28
  Group = -> [O_element107,Pb_element004,W_element005]
  conduct = 2
  density = 1
  expand = 3
  formula = G4_PbWO4
  name = G4_PbWO4
  specific = 4
FEATURE [App::DocumentObjectGroupPython] alactic  label="alactic : 1"  # scripted group (container) (typed FeaturePython)
  n = 1
  ref = alactic
FEATURE [App::DocumentObjectGroupPython] G4_Galactic  # scripted group (container) (typed FeaturePython)
  Dunit = g/cm3
  Dvalue = 0
  Group = -> [alactic]
  conduct = 2
  density = 1
  expand = 3
  formula = G4_Galactic
  name = G4_Galactic
  specific = 4
FEATURE [App::DocumentObjectGroupPython] RAPHITE_POROUS  label="RAPHITE_POROUS : 1"  # scripted group (container) (typed FeaturePython)
  n = 1
  ref = RAPHITE_POROUS
FEATURE [App::DocumentObjectGroupPython] G4_GRAPHITE_POROUS  # scripted group (container) (typed FeaturePython)
  Dunit = g/cm3
  Dvalue = 1.7
  Group = -> [RAPHITE_POROUS]
  conduct = 2
  density = 1
  expand = 3
  formula = G4_GRAPHITE_POROUS
  name = G4_GRAPHITE_POROUS
  specific = 4
FEATURE [App::DocumentObjectGroupPython] H_element115  label="H_element : 0.150"  # scripted group (container) (typed FeaturePython)
  n = 0.080538
FEATURE [App::DocumentObjectGroupPython] C_element125  label="C_element : 0.600"  # scripted group (container) (typed FeaturePython)
  n = 0.599848
FEATURE [App::DocumentObjectGroupPython] O_element108  label="O_element : 0.320"  # scripted group (container) (typed FeaturePython)
  n = 0.319614
FEATURE [App::DocumentObjectGroupPython] G4_LUCITE  # scripted group (container) (typed FeaturePython)
  Dunit = g/cm3
  Dvalue = 1.19
  Group = -> [H_element115,C_element125,O_element108]
  conduct = 2
  density = 1
  expand = 3
  formula = G4_LUCITE
  name = G4_LUCITE
  specific = 4
FEATURE [App::DocumentObjectGroupPython] Cu_element002  label="Cu_element : 62"  # scripted group (container) (typed FeaturePython)
  n = 62
  ref = Cu_element
FEATURE [App::DocumentObjectGroupPython] Zn_element002  label="Zn_element : 35"  # scripted group (container) (typed FeaturePython)
  n = 35
  ref = Zn_element
FEATURE [App::DocumentObjectGroupPython] Pb_element005  label="Pb_element : 3"  # scripted group (container) (typed FeaturePython)
  n = 3
  ref = Pb_element
FEATURE [App::DocumentObjectGroupPython] G4_BRASS  # scripted group (container) (typed FeaturePython)
  Dunit = g/cm3
  Dvalue = 8.52
  Group = -> [Cu_element002,Zn_element002,Pb_element005]
  conduct = 2
  density = 1
  expand = 3
  formula = G4_BRASS
  name = G4_BRASS
  specific = 4
FEATURE [App::DocumentObjectGroupPython] Cu_element003  label="Cu_element : 89"  # scripted group (container) (typed FeaturePython)
  n = 89
  ref = Cu_element
FEATURE [App::DocumentObjectGroupPython] Zn_element003  label="Zn_element : 9"  # scripted group (container) (typed FeaturePython)
  n = 9
  ref = Zn_element
FEATURE [App::DocumentObjectGroupPython] Pb_element006  label="Pb_element : 2"  # scripted group (container) (typed FeaturePython)
  n = 2
  ref = Pb_element
FEATURE [App::DocumentObjectGroupPython] G4_BRONZE  # scripted group (container) (typed FeaturePython)
  Dunit = g/cm3
  Dvalue = 8.82
  Group = -> [Cu_element003,Zn_element003,Pb_element006]
  conduct = 2
  density = 1
  expand = 3
  formula = G4_BRONZE
  name = G4_BRONZE
  specific = 4
FEATURE [App::DocumentObjectGroupPython] Fe_element008  label="Fe_element : 74"  # scripted group (container) (typed FeaturePython)
  n = 74
  ref = Fe_element
FEATURE [App::DocumentObjectGroupPython] Cr_element002  label="Cr_element : 18"  # scripted group (container) (typed FeaturePython)
  n = 18
  ref = Cr_element
FEATURE [App::DocumentObjectGroupPython] Ni_element002  label="Ni_element : 8"  # scripted group (container) (typed FeaturePython)
  n = 8
  ref = Ni_element
FEATURE [App::DocumentObjectGroupPython] G4_STAINLESS_STEEL  label="G4_STAINLESS-STEEL"  # scripted group (container) (typed FeaturePython)
  Dunit = g/cm3
  Dvalue = 8
  Group = -> [Fe_element008,Cr_element002,Ni_element002]
  conduct = 2
  density = 1
  expand = 3
  formula = G4_STAINLESS-STEEL
  name = G4_STAINLESS-STEEL
  specific = 4
FEATURE [App::DocumentObjectGroupPython] H_element116  label="H_element : 064"  # scripted group (container) (typed FeaturePython)
  n = 18
  ref = H_element
FEATURE [App::DocumentObjectGroupPython] C_element126  label="C_element : 071"  # scripted group (container) (typed FeaturePython)
  n = 12
  ref = C_element
FEATURE [App::DocumentObjectGroupPython] O_element109  label="O_element : 062"  # scripted group (container) (typed FeaturePython)
  n = 7
  ref = O_element
FEATURE [App::DocumentObjectGroupPython] G4_CR39  # scripted group (container) (typed FeaturePython)
  Dunit = g/cm3
  Dvalue = 1.32
  Group = -> [H_element116,C_element126,O_element109]
  conduct = 2
  density = 1
  expand = 3
  formula = G4_CR39
  name = G4_CR39
  specific = 4
FEATURE [App::DocumentObjectGroupPython] H_element117  label="H_element : 38"  # scripted group (container) (typed FeaturePython)
  n = 38
  ref = H_element
FEATURE [App::DocumentObjectGroupPython] C_element127  label="C_element : 072"  # scripted group (container) (typed FeaturePython)
  n = 18
  ref = C_element
FEATURE [App::DocumentObjectGroupPython] O_element110  label="O_element : 063"  # scripted group (container) (typed FeaturePython)
  n = 1
  ref = O_element
FEATURE [App::DocumentObjectGroupPython] G4_OCTADECANOL  # scripted group (container) (typed FeaturePython)
  Dunit = g/cm3
  Dvalue = 0.812
  Group = -> [H_element117,C_element127,O_element110]
  conduct = 2
  density = 1
  expand = 3
  formula = G4_OCTADECANOL
  name = G4_OCTADECANOL
  specific = 4
FEATURE [App::DocumentObjectGroupPython] HEP  # scripted group (container) (typed FeaturePython)
  Group = -> [G4_lH2,G4_lN2,G4_lO2,G4_lAr,G4_lBr,G4_lKr,G4_lXe,G4_PbWO4,G4_Galactic,G4_GRAPHITE_POROUS,G4_LUCITE,G4_BRASS,G4_BRONZE,G4_STAINLESS_STEEL,G4_CR39,G4_OCTADECANOL]
FEATURE [App::DocumentObjectGroupPython] C_element128  label="C_element : 073"  # scripted group (container) (typed FeaturePython)
  n = 14
  ref = C_element
FEATURE [App::DocumentObjectGroupPython] H_element118  label="H_element : 065"  # scripted group (container) (typed FeaturePython)
  n = 10
  ref = H_element
FEATURE [App::DocumentObjectGroupPython] O_element111  label="O_element : 064"  # scripted group (container) (typed FeaturePython)
  n = 2
  ref = O_element
FEATURE [App::DocumentObjectGroupPython] N_element050  label="N_element : 023"  # scripted group (container) (typed FeaturePython)
  n = 2
  ref = N_element
FEATURE [App::DocumentObjectGroupPython] G4_KEVLAR  # scripted group (container) (typed FeaturePython)
  Dunit = g/cm3
  Dvalue = 1.44
  Group = -> [C_element128,H_element118,O_element111,N_element050]
  conduct = 2
  density = 1
  expand = 3
  formula = G4_KEVLAR
  name = G4_KEVLAR
  specific = 4
FEATURE [App::DocumentObjectGroupPython] C_element129  label="C_element : 074"  # scripted group (container) (typed FeaturePython)
  n = 10
  ref = C_element
FEATURE [App::DocumentObjectGroupPython] H_element119  label="H_element : 066"  # scripted group (container) (typed FeaturePython)
  n = 8
  ref = H_element
FEATURE [App::DocumentObjectGroupPython] O_element112  label="O_element : 065"  # scripted group (container) (typed FeaturePython)
  n = 4
  ref = O_element
FEATURE [App::DocumentObjectGroupPython] G4_DACRON  # scripted group (container) (typed FeaturePython)
  Dunit = g/cm3
  Dvalue = 1.4
  Group = -> [C_element129,H_element119,O_element112]
  conduct = 2
  density = 1
  expand = 3
  formula = G4_DACRON
  name = G4_DACRON
  specific = 4
FEATURE [App::DocumentObjectGroupPython] C_element130  label="C_element : 075"  # scripted group (container) (typed FeaturePython)
  n = 4
  ref = C_element
FEATURE [App::DocumentObjectGroupPython] H_element120  label="H_element : 067"  # scripted group (container) (typed FeaturePython)
  n = 5
  ref = H_element
FEATURE [App::DocumentObjectGroupPython] Cl_element030  label="Cl_element : 016"  # scripted group (container) (typed FeaturePython)
  n = 1
  ref = Cl_element
FEATURE [App::DocumentObjectGroupPython] G4_NEOPRENE  # scripted group (container) (typed FeaturePython)
  Dunit = g/cm3
  Dvalue = 1.23
  Group = -> [C_element130,H_element120,Cl_element030]
  conduct = 2
  density = 1
  expand = 3
  formula = G4_NEOPRENE
  name = G4_NEOPRENE
  specific = 4
FEATURE [App::DocumentObjectGroupPython] Space  # scripted group (container) (typed FeaturePython)
  Group = -> [G4_KEVLAR,G4_DACRON,G4_NEOPRENE]
FEATURE [App::DocumentObjectGroupPython] H_element121  label="H_element : 068"  # scripted group (container) (typed FeaturePython)
  n = 5
  ref = H_element
FEATURE [App::DocumentObjectGroupPython] C_element131  label="C_element : 076"  # scripted group (container) (typed FeaturePython)
  n = 4
  ref = C_element
FEATURE [App::DocumentObjectGroupPython] N_element051  label="N_element : 3"  # scripted group (container) (typed FeaturePython)
  n = 3
  ref = N_element
FEATURE [App::DocumentObjectGroupPython] O_element113  label="O_element : 066"  # scripted group (container) (typed FeaturePython)
  n = 1
  ref = O_element
FEATURE [App::DocumentObjectGroupPython] G4_CYTOSINE  # scripted group (container) (typed FeaturePython)
  Dunit = g/cm3
  Dvalue = 1.55
  Group = -> [H_element121,C_element131,N_element051,O_element113]
  conduct = 2
  density = 1
  expand = 3
  formula = G4_CYTOSINE
  name = G4_CYTOSINE
  specific = 4
FEATURE [App::DocumentObjectGroupPython] H_element122  label="H_element : 069"  # scripted group (container) (typed FeaturePython)
  n = 6
  ref = H_element
FEATURE [App::DocumentObjectGroupPython] C_element132  label="C_element : 077"  # scripted group (container) (typed FeaturePython)
  n = 5
  ref = C_element
FEATURE [App::DocumentObjectGroupPython] N_element052  label="N_element : 024"  # scripted group (container) (typed FeaturePython)
  n = 2
  ref = N_element
FEATURE [App::DocumentObjectGroupPython] O_element114  label="O_element : 067"  # scripted group (container) (typed FeaturePython)
  n = 2
  ref = O_element
FEATURE [App::DocumentObjectGroupPython] G4_THYMINE  # scripted group (container) (typed FeaturePython)
  Dunit = g/cm3
  Dvalue = 1.23
  Group = -> [H_element122,C_element132,N_element052,O_element114]
  conduct = 2
  density = 1
  expand = 3
  formula = G4_THYMINE
  name = G4_THYMINE
  specific = 4
FEATURE [App::DocumentObjectGroupPython] H_element123  label="H_element : 070"  # scripted group (container) (typed FeaturePython)
  n = 4
  ref = H_element
FEATURE [App::DocumentObjectGroupPython] C_element133  label="C_element : 078"  # scripted group (container) (typed FeaturePython)
  n = 4
  ref = C_element
FEATURE [App::DocumentObjectGroupPython] N_element053  label="N_element : 025"  # scripted group (container) (typed FeaturePython)
  n = 2
  ref = N_element
FEATURE [App::DocumentObjectGroupPython] O_element115  label="O_element : 068"  # scripted group (container) (typed FeaturePython)
  n = 2
  ref = O_element
FEATURE [App::DocumentObjectGroupPython] G4_URACIL  # scripted group (container) (typed FeaturePython)
  Dunit = g/cm3
  Dvalue = 1.32
  Group = -> [H_element123,C_element133,N_element053,O_element115]
  conduct = 2
  density = 1
  expand = 3
  formula = G4_URACIL
  name = G4_URACIL
  specific = 4
FEATURE [App::DocumentObjectGroupPython] H_element124  label="H_element : 071"  # scripted group (container) (typed FeaturePython)
  n = 4
  ref = H_element
FEATURE [App::DocumentObjectGroupPython] C_element134  label="C_element : 079"  # scripted group (container) (typed FeaturePython)
  n = 5
  ref = C_element
FEATURE [App::DocumentObjectGroupPython] N_element054  label="N_element : 026"  # scripted group (container) (typed FeaturePython)
  n = 5
  ref = N_element
FEATURE [App::DocumentObjectGroupPython] G4_DNA_ADENINE  # scripted group (container) (typed FeaturePython)
  Dunit = g/cm3
  Dvalue = 1
  Group = -> [H_element124,C_element134,N_element054]
  conduct = 2
  density = 1
  expand = 3
  formula = G4_DNA_ADENINE
  name = G4_DNA_ADENINE
  specific = 4
FEATURE [App::DocumentObjectGroupPython] H_element125  label="H_element : 072"  # scripted group (container) (typed FeaturePython)
  n = 4
  ref = H_element
FEATURE [App::DocumentObjectGroupPython] C_element135  label="C_element : 080"  # scripted group (container) (typed FeaturePython)
  n = 5
  ref = C_element
FEATURE [App::DocumentObjectGroupPython] N_element055  label="N_element : 027"  # scripted group (container) (typed FeaturePython)
  n = 5
  ref = N_element
FEATURE [App::DocumentObjectGroupPython] O_element116  label="O_element : 069"  # scripted group (container) (typed FeaturePython)
  n = 1
  ref = O_element
FEATURE [App::DocumentObjectGroupPython] G4_DNA_GUANINE  # scripted group (container) (typed FeaturePython)
  Dunit = g/cm3
  Dvalue = 1
  Group = -> [H_element125,C_element135,N_element055,O_element116]
  conduct = 2
  density = 1
  expand = 3
  formula = G4_DNA_GUANINE
  name = G4_DNA_GUANINE
  specific = 4
FEATURE [App::DocumentObjectGroupPython] H_element126  label="H_element : 073"  # scripted group (container) (typed FeaturePython)
  n = 4
  ref = H_element
FEATURE [App::DocumentObjectGroupPython] C_element136  label="C_element : 081"  # scripted group (container) (typed FeaturePython)
  n = 4
  ref = C_element
FEATURE [App::DocumentObjectGroupPython] N_element056  label="N_element : 028"  # scripted group (container) (typed FeaturePython)
  n = 3
  ref = N_element
FEATURE [App::DocumentObjectGroupPython] O_element117  label="O_element : 070"  # scripted group (container) (typed FeaturePython)
  n = 1
  ref = O_element
FEATURE [App::DocumentObjectGroupPython] G4_DNA_CYTOSINE  # scripted group (container) (typed FeaturePython)
  Dunit = g/cm3
  Dvalue = 1
  Group = -> [H_element126,C_element136,N_element056,O_element117]
  conduct = 2
  density = 1
  expand = 3
  formula = G4_DNA_CYTOSINE
  name = G4_DNA_CYTOSINE
  specific = 4
FEATURE [App::DocumentObjectGroupPython] H_element127  label="H_element : 074"  # scripted group (container) (typed FeaturePython)
  n = 5
  ref = H_element
FEATURE [App::DocumentObjectGroupPython] C_element137  label="C_element : 082"  # scripted group (container) (typed FeaturePython)
  n = 5
  ref = C_element
FEATURE [App::DocumentObjectGroupPython] N_element057  label="N_element : 029"  # scripted group (container) (typed FeaturePython)
  n = 2
  ref = N_element
FEATURE [App::DocumentObjectGroupPython] O_element118  label="O_element : 071"  # scripted group (container) (typed FeaturePython)
  n = 2
  ref = O_element
FEATURE [App::DocumentObjectGroupPython] G4_DNA_THYMINE  # scripted group (container) (typed FeaturePython)
  Dunit = g/cm3
  Dvalue = 1
  Group = -> [H_element127,C_element137,N_element057,O_element118]
  conduct = 2
  density = 1
  expand = 3
  formula = G4_DNA_THYMINE
  name = G4_DNA_THYMINE
  specific = 4
FEATURE [App::DocumentObjectGroupPython] H_element128  label="H_element : 075"  # scripted group (container) (typed FeaturePython)
  n = 3
  ref = H_element
FEATURE [App::DocumentObjectGroupPython] C_element138  label="C_element : 083"  # scripted group (container) (typed FeaturePython)
  n = 4
  ref = C_element
FEATURE [App::DocumentObjectGroupPython] N_element058  label="N_element : 030"  # scripted group (container) (typed FeaturePython)
  n = 2
  ref = N_element
FEATURE [App::DocumentObjectGroupPython] O_element119  label="O_element : 072"  # scripted group (container) (typed FeaturePython)
  n = 2
  ref = O_element
FEATURE [App::DocumentObjectGroupPython] G4_DNA_URACIL  # scripted group (container) (typed FeaturePython)
  Dunit = g/cm3
  Dvalue = 1
  Group = -> [H_element128,C_element138,N_element058,O_element119]
  conduct = 2
  density = 1
  expand = 3
  formula = G4_DNA_URACIL
  name = G4_DNA_URACIL
  specific = 4
FEATURE [App::DocumentObjectGroupPython] H_element129  label="H_element : 076"  # scripted group (container) (typed FeaturePython)
  n = 10
  ref = H_element
FEATURE [App::DocumentObjectGroupPython] C_element139  label="C_element : 084"  # scripted group (container) (typed FeaturePython)
  n = 10
  ref = C_element
FEATURE [App::DocumentObjectGroupPython] N_element059  label="N_element : 031"  # scripted group (container) (typed FeaturePython)
  n = 5
  ref = N_element
FEATURE [App::DocumentObjectGroupPython] O_element120  label="O_element : 073"  # scripted group (container) (typed FeaturePython)
  n = 4
  ref = O_element
FEATURE [App::DocumentObjectGroupPython] G4_DNA_ADENOSINE  # scripted group (container) (typed FeaturePython)
  Dunit = g/cm3
  Dvalue = 1
  Group = -> [H_element129,C_element139,N_element059,O_element120]
  conduct = 2
  density = 1
  expand = 3
  formula = G4_DNA_ADENOSINE
  name = G4_DNA_ADENOSINE
  specific = 4
FEATURE [App::DocumentObjectGroupPython] H_element130  label="H_element : 077"  # scripted group (container) (typed FeaturePython)
  n = 10
  ref = H_element
FEATURE [App::DocumentObjectGroupPython] C_element140  label="C_element : 085"  # scripted group (container) (typed FeaturePython)
  n = 10
  ref = C_element
FEATURE [App::DocumentObjectGroupPython] N_element060  label="N_element : 032"  # scripted group (container) (typed FeaturePython)
  n = 5
  ref = N_element
FEATURE [App::DocumentObjectGroupPython] O_element121  label="O_element : 074"  # scripted group (container) (typed FeaturePython)
  n = 5
  ref = O_element
FEATURE [App::DocumentObjectGroupPython] G4_DNA_GUANOSINE  # scripted group (container) (typed FeaturePython)
  Dunit = g/cm3
  Dvalue = 1
  Group = -> [H_element130,C_element140,N_element060,O_element121]
  conduct = 2
  density = 1
  expand = 3
  formula = G4_DNA_GUANOSINE
  name = G4_DNA_GUANOSINE
  specific = 4
FEATURE [App::DocumentObjectGroupPython] H_element131  label="H_element : 078"  # scripted group (container) (typed FeaturePython)
  n = 10
  ref = H_element
FEATURE [App::DocumentObjectGroupPython] C_element141  label="C_element : 086"  # scripted group (container) (typed FeaturePython)
  n = 9
  ref = C_element
FEATURE [App::DocumentObjectGroupPython] N_element061  label="N_element : 033"  # scripted group (container) (typed FeaturePython)
  n = 3
  ref = N_element
FEATURE [App::DocumentObjectGroupPython] O_element122  label="O_element : 075"  # scripted group (container) (typed FeaturePython)
  n = 5
  ref = O_element
FEATURE [App::DocumentObjectGroupPython] G4_DNA_CYTIDINE  # scripted group (container) (typed FeaturePython)
  Dunit = g/cm3
  Dvalue = 1
  Group = -> [H_element131,C_element141,N_element061,O_element122]
  conduct = 2
  density = 1
  expand = 3
  formula = G4_DNA_CYTIDINE
  name = G4_DNA_CYTIDINE
  specific = 4
FEATURE [App::DocumentObjectGroupPython] H_element132  label="H_element : 079"  # scripted group (container) (typed FeaturePython)
  n = 9
  ref = H_element
FEATURE [App::DocumentObjectGroupPython] C_element142  label="C_element : 087"  # scripted group (container) (typed FeaturePython)
  n = 9
  ref = C_element
FEATURE [App::DocumentObjectGroupPython] N_element062  label="N_element : 034"  # scripted group (container) (typed FeaturePython)
  n = 2
  ref = N_element
FEATURE [App::DocumentObjectGroupPython] O_element123  label="O_element : 076"  # scripted group (container) (typed FeaturePython)
  n = 6
  ref = O_element
FEATURE [App::DocumentObjectGroupPython] G4_DNA_URIDINE  # scripted group (container) (typed FeaturePython)
  Dunit = g/cm3
  Dvalue = 1
  Group = -> [H_element132,C_element142,N_element062,O_element123]
  conduct = 2
  density = 1
  expand = 3
  formula = G4_DNA_URIDINE
  name = G4_DNA_URIDINE
  specific = 4
FEATURE [App::DocumentObjectGroupPython] H_element133  label="H_element : 080"  # scripted group (container) (typed FeaturePython)
  n = 11
  ref = H_element
FEATURE [App::DocumentObjectGroupPython] C_element143  label="C_element : 088"  # scripted group (container) (typed FeaturePython)
  n = 10
  ref = C_element
FEATURE [App::DocumentObjectGroupPython] N_element063  label="N_element : 035"  # scripted group (container) (typed FeaturePython)
  n = 2
  ref = N_element
FEATURE [App::DocumentObjectGroupPython] O_element124  label="O_element : 077"  # scripted group (container) (typed FeaturePython)
  n = 6
  ref = O_element
FEATURE [App::DocumentObjectGroupPython] G4_DNA_METHYLURIDINE  # scripted group (container) (typed FeaturePython)
  Dunit = g/cm3
  Dvalue = 1
  Group = -> [H_element133,C_element143,N_element063,O_element124]
  conduct = 2
  density = 1
  expand = 3
  formula = G4_DNA_METHYLURIDINE
  name = G4_DNA_METHYLURIDINE
  specific = 4
FEATURE [App::DocumentObjectGroupPython] P_element014  label="P_element : 003"  # scripted group (container) (typed FeaturePython)
  n = 1
  ref = P_element
FEATURE [App::DocumentObjectGroupPython] O_element125  label="O_element : 078"  # scripted group (container) (typed FeaturePython)
  n = 3
  ref = O_element
FEATURE [App::DocumentObjectGroupPython] G4_DNA_MONOPHOSPHATE  # scripted group (container) (typed FeaturePython)
  Dunit = g/cm3
  Dvalue = 1
  Group = -> [P_element014,O_element125]
  conduct = 2
  density = 1
  expand = 3
  formula = G4_DNA_MONOPHOSPHATE
  name = G4_DNA_MONOPHOSPHATE
  specific = 4
FEATURE [App::DocumentObjectGroupPython] H_element134  label="H_element : 081"  # scripted group (container) (typed FeaturePython)
  n = 10
  ref = H_element
FEATURE [App::DocumentObjectGroupPython] C_element144  label="C_element : 089"  # scripted group (container) (typed FeaturePython)
  n = 10
  ref = C_element
FEATURE [App::DocumentObjectGroupPython] N_element064  label="N_element : 036"  # scripted group (container) (typed FeaturePython)
  n = 5
  ref = N_element
FEATURE [App::DocumentObjectGroupPython] O_element126  label="O_element : 079"  # scripted group (container) (typed FeaturePython)
  n = 7
  ref = O_element
FEATURE [App::DocumentObjectGroupPython] P_element015  label="P_element : 004"  # scripted group (container) (typed FeaturePython)
  n = 1
  ref = P_element
FEATURE [App::DocumentObjectGroupPython] G4_DNA_A  # scripted group (container) (typed FeaturePython)
  Dunit = g/cm3
  Dvalue = 1
  Group = -> [H_element134,C_element144,N_element064,O_element126,P_element015]
  conduct = 2
  density = 1
  expand = 3
  formula = G4_DNA_A
  name = G4_DNA_A
  specific = 4
FEATURE [App::DocumentObjectGroupPython] H_element135  label="H_element : 082"  # scripted group (container) (typed FeaturePython)
  n = 10
  ref = H_element
FEATURE [App::DocumentObjectGroupPython] C_element145  label="C_element : 090"  # scripted group (container) (typed FeaturePython)
  n = 10
  ref = C_element
FEATURE [App::DocumentObjectGroupPython] N_element065  label="N_element : 037"  # scripted group (container) (typed FeaturePython)
  n = 5
  ref = N_element
FEATURE [App::DocumentObjectGroupPython] O_element127  label="O_element : 8"  # scripted group (container) (typed FeaturePython)
  n = 8
  ref = O_element
FEATURE [App::DocumentObjectGroupPython] P_element016  label="P_element : 005"  # scripted group (container) (typed FeaturePython)
  n = 1
  ref = P_element
FEATURE [App::DocumentObjectGroupPython] G4_DNA_G  # scripted group (container) (typed FeaturePython)
  Dunit = g/cm3
  Dvalue = 1
  Group = -> [H_element135,C_element145,N_element065,O_element127,P_element016]
  conduct = 2
  density = 1
  expand = 3
  formula = G4_DNA_G
  name = G4_DNA_G
  specific = 4
FEATURE [App::DocumentObjectGroupPython] H_element136  label="H_element : 083"  # scripted group (container) (typed FeaturePython)
  n = 10
  ref = H_element
FEATURE [App::DocumentObjectGroupPython] C_element146  label="C_element : 091"  # scripted group (container) (typed FeaturePython)
  n = 9
  ref = C_element
FEATURE [App::DocumentObjectGroupPython] N_element066  label="N_element : 038"  # scripted group (container) (typed FeaturePython)
  n = 3
  ref = N_element
FEATURE [App::DocumentObjectGroupPython] O_element128  label="O_element : 080"  # scripted group (container) (typed FeaturePython)
  n = 8
  ref = O_element
FEATURE [App::DocumentObjectGroupPython] P_element017  label="P_element : 006"  # scripted group (container) (typed FeaturePython)
  n = 1
  ref = P_element
FEATURE [App::DocumentObjectGroupPython] G4_DNA_C  # scripted group (container) (typed FeaturePython)
  Dunit = g/cm3
  Dvalue = 1
  Group = -> [H_element136,C_element146,N_element066,O_element128,P_element017]
  conduct = 2
  density = 1
  expand = 3
  formula = G4_DNA_C
  name = G4_DNA_C
  specific = 4
FEATURE [App::DocumentObjectGroupPython] H_element137  label="H_element : 084"  # scripted group (container) (typed FeaturePython)
  n = 9
  ref = H_element
FEATURE [App::DocumentObjectGroupPython] C_element147  label="C_element : 092"  # scripted group (container) (typed FeaturePython)
  n = 9
  ref = C_element
FEATURE [App::DocumentObjectGroupPython] N_element067  label="N_element : 039"  # scripted group (container) (typed FeaturePython)
  n = 2
  ref = N_element
FEATURE [App::DocumentObjectGroupPython] O_element129  label="O_element : 9"  # scripted group (container) (typed FeaturePython)
  n = 9
  ref = O_element
FEATURE [App::DocumentObjectGroupPython] P_element018  label="P_element : 007"  # scripted group (container) (typed FeaturePython)
  n = 1
  ref = P_element
FEATURE [App::DocumentObjectGroupPython] G4_DNA_U  # scripted group (container) (typed FeaturePython)
  Dunit = g/cm3
  Dvalue = 1
  Group = -> [H_element137,C_element147,N_element067,O_element129,P_element018]
  conduct = 2
  density = 1
  expand = 3
  formula = G4_DNA_U
  name = G4_DNA_U
  specific = 4
FEATURE [App::DocumentObjectGroupPython] H_element138  label="H_element : 085"  # scripted group (container) (typed FeaturePython)
  n = 11
  ref = H_element
FEATURE [App::DocumentObjectGroupPython] C_element148  label="C_element : 093"  # scripted group (container) (typed FeaturePython)
  n = 10
  ref = C_element
FEATURE [App::DocumentObjectGroupPython] N_element068  label="N_element : 040"  # scripted group (container) (typed FeaturePython)
  n = 2
  ref = N_element
FEATURE [App::DocumentObjectGroupPython] O_element130  label="O_element : 081"  # scripted group (container) (typed FeaturePython)
  n = 9
  ref = O_element
FEATURE [App::DocumentObjectGroupPython] P_element019  label="P_element : 008"  # scripted group (container) (typed FeaturePython)
  n = 1
  ref = P_element
FEATURE [App::DocumentObjectGroupPython] G4_DNA_MU  # scripted group (container) (typed FeaturePython)
  Dunit = g/cm3
  Dvalue = 1
  Group = -> [H_element138,C_element148,N_element068,O_element130,P_element019]
  conduct = 2
  density = 1
  expand = 3
  formula = G4_DNA_MU
  name = G4_DNA_MU
  specific = 4
FEATURE [App::DocumentObjectGroupPython] BioChemical  # scripted group (container) (typed FeaturePython)
  Group = -> [G4_CYTOSINE,G4_THYMINE,G4_URACIL,G4_DNA_ADENINE,G4_DNA_GUANINE,G4_DNA_CYTOSINE,G4_DNA_THYMINE,G4_DNA_URACIL,G4_DNA_ADENOSINE,G4_DNA_GUANOSINE,G4_DNA_CYTIDINE,G4_DNA_URIDINE,G4_DNA_METHYLURIDINE,G4_DNA_MONOPHOSPHATE,G4_DNA_A,G4_DNA_G,G4_DNA_C,G4_DNA_U,G4_DNA_MU]
FEATURE [App::DocumentObjectGroupPython] G4Materials  # scripted group (container) (typed FeaturePython)
  Group = -> [NIST,Element,HEP,Space,BioChemical]
  version = 1
FEATURE [App::DocumentObjectGroupPython] Geant4  # scripted group (container) (typed FeaturePython)
  Group = -> [G4Isotopes,G4Elements,G4Materials]
FEATURE [App::DocumentObjectGroupPython] Materials  # scripted group (container) (typed FeaturePython)
  Group = -> [Geant4]
FEATURE [Part::FeaturePython] GDMLBox_WorldBox  # WARN: FeaturePython — macro-defined, semantics opaque (R4)
  lunit = 2
  material = 5
  x = 100
  y = 100
  z = 100
FEATURE [Sketcher::SketchObject] Sketch
  ArcFitTolerance = 0
  FullyConstrained = false
  MakeInternals = false
  sketch-geometry (15):
    g0-g5: Circle [constr] x6 (B-spline internal-alignment scaffolding for g6; pole/knot coordinates omitted)
    g6: BSplineCurve PolesCount=7 KnotsCount=5 Degree=3 IsPeriodic=0
    g7-g10: GeomPoint [constr] x4 (B-spline internal-alignment scaffolding for g6; pole/knot coordinates omitted)
    g11: LineSegment StartX=-4.39557 StartY=8.39124 StartZ=0 EndX=-5.2662 EndY=10.5884 EndZ=0
    g12: LineSegment StartX=-5.2662 StartY=10.5884 StartZ=0 EndX=-7.82152 EndY=9.89481 EndZ=0
    g13: LineSegment StartX=-7.82152 StartY=9.89481 StartZ=0 EndX=-9.50073 EndY=7.63152 EndZ=0
    g14: ArcOfCircle CenterX=-7.8377 CenterY=5.34547 CenterZ=0 NormalX=0 NormalY=0 NormalZ=1 AngleXU=0 Radius=2.82696 StartAngle=4.84147 EndAngle=8.48291
  constraints (9):
    c: Weight(g0) = 1
    c: Equal(g0, g1-g5) x5
    c: InternalAlignment(g0-g5 -> g6) x6
    c: InternalAlignment(g7-g10 -> g6) x4
    c: Coincident(g11,g6)
    c: Coincident(g11,g12)
    c: Coincident(g12,g13)
    c: Coincident(g14,g13)
    c: Coincident(g14,g6)
FEATURE [Part::Extrusion] Extrude
  Base = -> Sketch
  Dir = (0,0,1)
  DirMode = 2
  FaceMakerClass = Part::FaceMakerBullseye
  FaceMakerMode = 3
  LengthFwd = 10
  LengthRev = 0
  Placement = pos=(13,9,0) rot=(0,0,1;0rad)
  Solid = true
  Symmetric = false
  material = 1
FEATURE [Part::Mirroring] Part__Mirroring  label="Extrude_mirror"
  Base = (0,0,0)
  Normal = (0,1,0)
  Source = -> Extrude
  material = 261
FEATURE [App::Part] Part
  Group = -> [Sketch,Extrude,Part__Mirroring]
  Origin = -> Origin001
FEATURE [App::Part] worldVOL
  Group = -> [GDMLBox_WorldBox,Part]
  Origin = -> Origin
